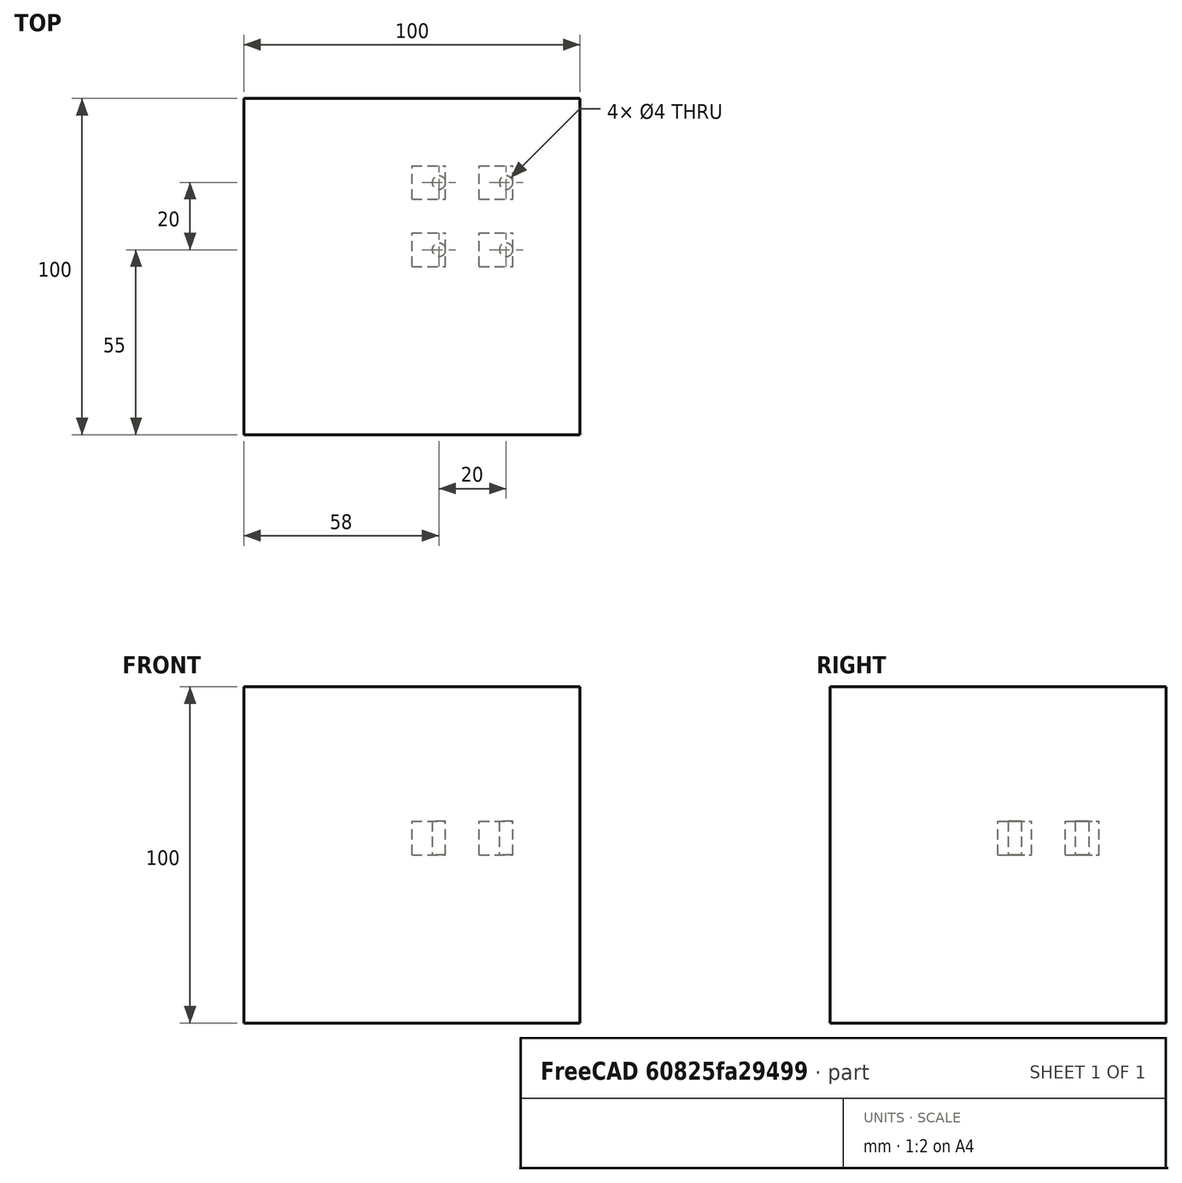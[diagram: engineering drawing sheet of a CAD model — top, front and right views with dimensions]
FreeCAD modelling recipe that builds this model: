
FCSTD DOCUMENT  (FreeCAD 1.0R39109 (Git))
Label: orthoArray_of_Cut
License: All rights reserved
objects: App::DocumentObjectGroupPython×1251, Part::FeaturePython×2, App::Part×2, Part::Box×1, Part::Cylinder×1, Part::Cut×1
note: 5 computed .brp shape members not serialized (recipe doc carries the construction recipe); baked Part::Feature solids carry a one-line shape summary decoded from their .brp

FEATURE [App::DocumentObjectGroupPython] HALFPI  # scripted group (container) (typed FeaturePython)
  name = HALFPI
  value = pi/2.
FEATURE [App::DocumentObjectGroupPython] PI  # scripted group (container) (typed FeaturePython)
  name = PI
  value = 1.*pi
FEATURE [App::DocumentObjectGroupPython] TWOPI  # scripted group (container) (typed FeaturePython)
  name = TWOPI
  value = 2.*pi
FEATURE [App::DocumentObjectGroupPython] Constants  # scripted group (container) (typed FeaturePython)
  Group = -> [HALFPI,PI,TWOPI]
FEATURE [App::DocumentObjectGroupPython] Variables  # scripted group (container) (typed FeaturePython)
FEATURE [App::DocumentObjectGroupPython] Quantities  # scripted group (container) (typed FeaturePython)
FEATURE [App::DocumentObjectGroupPython] Isotopes  # scripted group (container) (typed FeaturePython)
FEATURE [App::DocumentObjectGroupPython] Elements  # scripted group (container) (typed FeaturePython)
FEATURE [App::DocumentObjectGroupPython] Matrix  # scripted group (container) (typed FeaturePython)
FEATURE [App::DocumentObjectGroupPython] Surfaces  # scripted group (container) (typed FeaturePython)
FEATURE [App::DocumentObjectGroupPython] Opticals  # scripted group (container) (typed FeaturePython)
  Group = -> [Matrix,Surfaces]
FEATURE [App::DocumentObjectGroupPython] G4Isotopes  # scripted group (container) (typed FeaturePython)
FEATURE [App::DocumentObjectGroupPython] H_element  # scripted group (container) (typed FeaturePython)
  Z = 1
  atom_value = 1.008
  formula = H
  name = H_element
FEATURE [App::DocumentObjectGroupPython] He_element  # scripted group (container) (typed FeaturePython)
  Z = 2
  atom_value = 4.0026
  formula = He
  name = He_element
FEATURE [App::DocumentObjectGroupPython] Li_element  # scripted group (container) (typed FeaturePython)
  Z = 3
  atom_value = 6.94
  formula = Li
  name = Li_element
FEATURE [App::DocumentObjectGroupPython] Be_element  # scripted group (container) (typed FeaturePython)
  Z = 4
  atom_value = 9.01218
  formula = Be
  name = Be_element
FEATURE [App::DocumentObjectGroupPython] B_element  # scripted group (container) (typed FeaturePython)
  Z = 5
  atom_value = 10.81
  formula = B
  name = B_element
FEATURE [App::DocumentObjectGroupPython] C_element  # scripted group (container) (typed FeaturePython)
  Z = 6
  atom_value = 12.011
  formula = C
  name = C_element
FEATURE [App::DocumentObjectGroupPython] N_element  # scripted group (container) (typed FeaturePython)
  Z = 7
  atom_value = 14.007
  formula = N
  name = N_element
FEATURE [App::DocumentObjectGroupPython] O_element  # scripted group (container) (typed FeaturePython)
  Z = 8
  atom_value = 15.999
  formula = O
  name = O_element
FEATURE [App::DocumentObjectGroupPython] F_element  # scripted group (container) (typed FeaturePython)
  Z = 9
  atom_value = 18.9984
  formula = F
  name = F_element
FEATURE [App::DocumentObjectGroupPython] Ne_element  # scripted group (container) (typed FeaturePython)
  Z = 10
  atom_value = 20.1797
  formula = Ne
  name = Ne_element
FEATURE [App::DocumentObjectGroupPython] Na_element  # scripted group (container) (typed FeaturePython)
  Z = 11
  atom_value = 22.9898
  formula = Na
  name = Na_element
FEATURE [App::DocumentObjectGroupPython] Mg_element  # scripted group (container) (typed FeaturePython)
  Z = 12
  atom_value = 24.305
  formula = Mg
  name = Mg_element
FEATURE [App::DocumentObjectGroupPython] Al_element  # scripted group (container) (typed FeaturePython)
  Z = 13
  atom_value = 26.9815
  formula = Al
  name = Al_element
FEATURE [App::DocumentObjectGroupPython] Si_element  # scripted group (container) (typed FeaturePython)
  Z = 14
  atom_value = 28.085
  formula = Si
  name = Si_element
FEATURE [App::DocumentObjectGroupPython] P_element  # scripted group (container) (typed FeaturePython)
  Z = 15
  atom_value = 30.9738
  formula = P
  name = P_element
FEATURE [App::DocumentObjectGroupPython] S_element  # scripted group (container) (typed FeaturePython)
  Z = 16
  atom_value = 32.06
  formula = S
  name = S_element
FEATURE [App::DocumentObjectGroupPython] Cl_element  # scripted group (container) (typed FeaturePython)
  Z = 17
  atom_value = 35.45
  formula = Cl
  name = Cl_element
FEATURE [App::DocumentObjectGroupPython] Ar_element  # scripted group (container) (typed FeaturePython)
  Z = 18
  atom_value = 39.95
  formula = Ar
  name = Ar_element
FEATURE [App::DocumentObjectGroupPython] K_element  # scripted group (container) (typed FeaturePython)
  Z = 19
  atom_value = 39.0983
  formula = K
  name = K_element
FEATURE [App::DocumentObjectGroupPython] Ca_element  # scripted group (container) (typed FeaturePython)
  Z = 20
  atom_value = 40.078
  formula = Ca
  name = Ca_element
FEATURE [App::DocumentObjectGroupPython] Sc_element  # scripted group (container) (typed FeaturePython)
  Z = 21
  atom_value = 44.9559
  formula = Sc
  name = Sc_element
FEATURE [App::DocumentObjectGroupPython] Ti_element  # scripted group (container) (typed FeaturePython)
  Z = 22
  atom_value = 47.867
  formula = Ti
  name = Ti_element
FEATURE [App::DocumentObjectGroupPython] V_element  # scripted group (container) (typed FeaturePython)
  Z = 23
  atom_value = 50.9415
  formula = V
  name = V_element
FEATURE [App::DocumentObjectGroupPython] Cr_element  # scripted group (container) (typed FeaturePython)
  Z = 24
  atom_value = 51.9961
  formula = Cr
  name = Cr_element
FEATURE [App::DocumentObjectGroupPython] Mn_element  # scripted group (container) (typed FeaturePython)
  Z = 25
  atom_value = 54.938
  formula = Mn
  name = Mn_element
FEATURE [App::DocumentObjectGroupPython] Fe_element  # scripted group (container) (typed FeaturePython)
  Z = 26
  atom_value = 55.845
  formula = Fe
  name = Fe_element
FEATURE [App::DocumentObjectGroupPython] Co_element  # scripted group (container) (typed FeaturePython)
  Z = 27
  atom_value = 58.9332
  formula = Co
  name = Co_element
FEATURE [App::DocumentObjectGroupPython] Ni_element  # scripted group (container) (typed FeaturePython)
  Z = 28
  atom_value = 58.6934
  formula = Ni
  name = Ni_element
FEATURE [App::DocumentObjectGroupPython] Cu_element  # scripted group (container) (typed FeaturePython)
  Z = 29
  atom_value = 63.546
  formula = Cu
  name = Cu_element
FEATURE [App::DocumentObjectGroupPython] Zn_element  # scripted group (container) (typed FeaturePython)
  Z = 30
  atom_value = 65.38
  formula = Zn
  name = Zn_element
FEATURE [App::DocumentObjectGroupPython] Ga_element  # scripted group (container) (typed FeaturePython)
  Z = 31
  atom_value = 69.723
  formula = Ga
  name = Ga_element
FEATURE [App::DocumentObjectGroupPython] Ge_element  # scripted group (container) (typed FeaturePython)
  Z = 32
  atom_value = 72.63
  formula = Ge
  name = Ge_element
FEATURE [App::DocumentObjectGroupPython] As_element  # scripted group (container) (typed FeaturePython)
  Z = 33
  atom_value = 74.9216
  formula = As
  name = As_element
FEATURE [App::DocumentObjectGroupPython] Se_element  # scripted group (container) (typed FeaturePython)
  Z = 34
  atom_value = 78.971
  formula = Se
  name = Se_element
FEATURE [App::DocumentObjectGroupPython] Br_element  # scripted group (container) (typed FeaturePython)
  Z = 35
  atom_value = 79.904
  formula = Br
  name = Br_element
FEATURE [App::DocumentObjectGroupPython] Kr_element  # scripted group (container) (typed FeaturePython)
  Z = 36
  atom_value = 83.798
  formula = Kr
  name = Kr_element
FEATURE [App::DocumentObjectGroupPython] Rb_element  # scripted group (container) (typed FeaturePython)
  Z = 37
  atom_value = 85.4678
  formula = Rb
  name = Rb_element
FEATURE [App::DocumentObjectGroupPython] Sr_element  # scripted group (container) (typed FeaturePython)
  Z = 38
  atom_value = 87.62
  formula = Sr
  name = Sr_element
FEATURE [App::DocumentObjectGroupPython] Y_element  # scripted group (container) (typed FeaturePython)
  Z = 39
  atom_value = 88.9058
  formula = Y
  name = Y_element
FEATURE [App::DocumentObjectGroupPython] Zr_element  # scripted group (container) (typed FeaturePython)
  Z = 40
  atom_value = 91.224
  formula = Zr
  name = Zr_element
FEATURE [App::DocumentObjectGroupPython] Nb_element  # scripted group (container) (typed FeaturePython)
  Z = 41
  atom_value = 92.9064
  formula = Nb
  name = Nb_element
FEATURE [App::DocumentObjectGroupPython] Mo_element  # scripted group (container) (typed FeaturePython)
  Z = 42
  atom_value = 95.95
  formula = Mo
  name = Mo_element
FEATURE [App::DocumentObjectGroupPython] Tc_element  # scripted group (container) (typed FeaturePython)
  Z = 43
  atom_value = 97
  formula = Tc
  name = Tc_element
FEATURE [App::DocumentObjectGroupPython] Ru_element  # scripted group (container) (typed FeaturePython)
  Z = 44
  atom_value = 101.07
  formula = Ru
  name = Ru_element
FEATURE [App::DocumentObjectGroupPython] Rh_element  # scripted group (container) (typed FeaturePython)
  Z = 45
  atom_value = 102.905
  formula = Rh
  name = Rh_element
FEATURE [App::DocumentObjectGroupPython] Pd_element  # scripted group (container) (typed FeaturePython)
  Z = 46
  atom_value = 106.42
  formula = Pd
  name = Pd_element
FEATURE [App::DocumentObjectGroupPython] Ag_element  # scripted group (container) (typed FeaturePython)
  Z = 47
  atom_value = 107.868
  formula = Ag
  name = Ag_element
FEATURE [App::DocumentObjectGroupPython] Cd_element  # scripted group (container) (typed FeaturePython)
  Z = 48
  atom_value = 112.414
  formula = Cd
  name = Cd_element
FEATURE [App::DocumentObjectGroupPython] In_element  # scripted group (container) (typed FeaturePython)
  Z = 49
  atom_value = 114.818
  formula = In
  name = In_element
FEATURE [App::DocumentObjectGroupPython] Sn_element  # scripted group (container) (typed FeaturePython)
  Z = 50
  atom_value = 118.71
  formula = Sn
  name = Sn_element
FEATURE [App::DocumentObjectGroupPython] Sb_element  # scripted group (container) (typed FeaturePython)
  Z = 51
  atom_value = 121.76
  formula = Sb
  name = Sb_element
FEATURE [App::DocumentObjectGroupPython] Te_element  # scripted group (container) (typed FeaturePython)
  Z = 52
  atom_value = 127.6
  formula = Te
  name = Te_element
FEATURE [App::DocumentObjectGroupPython] I_element  # scripted group (container) (typed FeaturePython)
  Z = 53
  atom_value = 126.904
  formula = I
  name = I_element
FEATURE [App::DocumentObjectGroupPython] Xe_element  # scripted group (container) (typed FeaturePython)
  Z = 54
  atom_value = 131.293
  formula = Xe
  name = Xe_element
FEATURE [App::DocumentObjectGroupPython] Cs_element  # scripted group (container) (typed FeaturePython)
  Z = 55
  atom_value = 132.905
  formula = Cs
  name = Cs_element
FEATURE [App::DocumentObjectGroupPython] Ba_element  # scripted group (container) (typed FeaturePython)
  Z = 56
  atom_value = 137.327
  formula = Ba
  name = Ba_element
FEATURE [App::DocumentObjectGroupPython] La_element  # scripted group (container) (typed FeaturePython)
  Z = 57
  atom_value = 138.905
  formula = La
  name = La_element
FEATURE [App::DocumentObjectGroupPython] Ce_element  # scripted group (container) (typed FeaturePython)
  Z = 58
  atom_value = 140.116
  formula = Ce
  name = Ce_element
FEATURE [App::DocumentObjectGroupPython] Pr_element  # scripted group (container) (typed FeaturePython)
  Z = 59
  atom_value = 140.908
  formula = Pr
  name = Pr_element
FEATURE [App::DocumentObjectGroupPython] Nd_element  # scripted group (container) (typed FeaturePython)
  Z = 60
  atom_value = 144.242
  formula = Nd
  name = Nd_element
FEATURE [App::DocumentObjectGroupPython] Pm_element  # scripted group (container) (typed FeaturePython)
  Z = 61
  atom_value = 145
  formula = Pm
  name = Pm_element
FEATURE [App::DocumentObjectGroupPython] Sm_element  # scripted group (container) (typed FeaturePython)
  Z = 62
  atom_value = 150.36
  formula = Sm
  name = Sm_element
FEATURE [App::DocumentObjectGroupPython] Eu_element  # scripted group (container) (typed FeaturePython)
  Z = 63
  atom_value = 151.964
  formula = Eu
  name = Eu_element
FEATURE [App::DocumentObjectGroupPython] Gd_element  # scripted group (container) (typed FeaturePython)
  Z = 64
  atom_value = 157.25
  formula = Gd
  name = Gd_element
FEATURE [App::DocumentObjectGroupPython] Tb_element  # scripted group (container) (typed FeaturePython)
  Z = 65
  atom_value = 158.925
  formula = Tb
  name = Tb_element
FEATURE [App::DocumentObjectGroupPython] Dy_element  # scripted group (container) (typed FeaturePython)
  Z = 66
  atom_value = 162.5
  formula = Dy
  name = Dy_element
FEATURE [App::DocumentObjectGroupPython] Ho_element  # scripted group (container) (typed FeaturePython)
  Z = 67
  atom_value = 164.93
  formula = Ho
  name = Ho_element
FEATURE [App::DocumentObjectGroupPython] Er_element  # scripted group (container) (typed FeaturePython)
  Z = 68
  atom_value = 167.259
  formula = Er
  name = Er_element
FEATURE [App::DocumentObjectGroupPython] Tm_element  # scripted group (container) (typed FeaturePython)
  Z = 69
  atom_value = 168.934
  formula = Tm
  name = Tm_element
FEATURE [App::DocumentObjectGroupPython] Yb_element  # scripted group (container) (typed FeaturePython)
  Z = 70
  atom_value = 173.045
  formula = Yb
  name = Yb_element
FEATURE [App::DocumentObjectGroupPython] Lu_element  # scripted group (container) (typed FeaturePython)
  Z = 71
  atom_value = 174.967
  formula = Lu
  name = Lu_element
FEATURE [App::DocumentObjectGroupPython] Hf_element  # scripted group (container) (typed FeaturePython)
  Z = 72
  atom_value = 178.49
  formula = Hf
  name = Hf_element
FEATURE [App::DocumentObjectGroupPython] Ta_element  # scripted group (container) (typed FeaturePython)
  Z = 73
  atom_value = 180.948
  formula = Ta
  name = Ta_element
FEATURE [App::DocumentObjectGroupPython] W_element  # scripted group (container) (typed FeaturePython)
  Z = 74
  atom_value = 183.84
  formula = W
  name = W_element
FEATURE [App::DocumentObjectGroupPython] Re_element  # scripted group (container) (typed FeaturePython)
  Z = 75
  atom_value = 186.207
  formula = Re
  name = Re_element
FEATURE [App::DocumentObjectGroupPython] Os_element  # scripted group (container) (typed FeaturePython)
  Z = 76
  atom_value = 190.23
  formula = Os
  name = Os_element
FEATURE [App::DocumentObjectGroupPython] Ir_element  # scripted group (container) (typed FeaturePython)
  Z = 77
  atom_value = 192.217
  formula = Ir
  name = Ir_element
FEATURE [App::DocumentObjectGroupPython] Pt_element  # scripted group (container) (typed FeaturePython)
  Z = 78
  atom_value = 195.084
  formula = Pt
  name = Pt_element
FEATURE [App::DocumentObjectGroupPython] Au_element  # scripted group (container) (typed FeaturePython)
  Z = 79
  atom_value = 196.967
  formula = Au
  name = Au_element
FEATURE [App::DocumentObjectGroupPython] Hg_element  # scripted group (container) (typed FeaturePython)
  Z = 80
  atom_value = 200.592
  formula = Hg
  name = Hg_element
FEATURE [App::DocumentObjectGroupPython] Tl_element  # scripted group (container) (typed FeaturePython)
  Z = 81
  atom_value = 204.38
  formula = Tl
  name = Tl_element
FEATURE [App::DocumentObjectGroupPython] Pb_element  # scripted group (container) (typed FeaturePython)
  Z = 82
  atom_value = 207.2
  formula = Pb
  name = Pb_element
FEATURE [App::DocumentObjectGroupPython] Bi_element  # scripted group (container) (typed FeaturePython)
  Z = 83
  atom_value = 208.98
  formula = Bi
  name = Bi_element
FEATURE [App::DocumentObjectGroupPython] Po_element  # scripted group (container) (typed FeaturePython)
  Z = 84
  atom_value = 209
  formula = Po
  name = Po_element
FEATURE [App::DocumentObjectGroupPython] At_element  # scripted group (container) (typed FeaturePython)
  Z = 85
  atom_value = 210
  formula = At
  name = At_element
FEATURE [App::DocumentObjectGroupPython] Rn_element  # scripted group (container) (typed FeaturePython)
  Z = 86
  atom_value = 222
  formula = Rn
  name = Rn_element
FEATURE [App::DocumentObjectGroupPython] Fr_element  # scripted group (container) (typed FeaturePython)
  Z = 87
  atom_value = 223
  formula = Fr
  name = Fr_element
FEATURE [App::DocumentObjectGroupPython] Ra_element  # scripted group (container) (typed FeaturePython)
  Z = 88
  atom_value = 226
  formula = Ra
  name = Ra_element
FEATURE [App::DocumentObjectGroupPython] Ac_element  # scripted group (container) (typed FeaturePython)
  Z = 89
  atom_value = 227
  formula = Ac
  name = Ac_element
FEATURE [App::DocumentObjectGroupPython] Th_element  # scripted group (container) (typed FeaturePython)
  Z = 90
  atom_value = 232.038
  formula = Th
  name = Th_element
FEATURE [App::DocumentObjectGroupPython] Pa_element  # scripted group (container) (typed FeaturePython)
  Z = 91
  atom_value = 231.036
  formula = Pa
  name = Pa_element
FEATURE [App::DocumentObjectGroupPython] U_element  # scripted group (container) (typed FeaturePython)
  Z = 92
  atom_value = 238.029
  formula = U
  name = U_element
FEATURE [App::DocumentObjectGroupPython] Np_element  # scripted group (container) (typed FeaturePython)
  Z = 93
  atom_value = 237
  formula = Np
  name = Np_element
FEATURE [App::DocumentObjectGroupPython] Pu_element  # scripted group (container) (typed FeaturePython)
  Z = 94
  atom_value = 244
  formula = Pu
  name = Pu_element
FEATURE [App::DocumentObjectGroupPython] Am_element  # scripted group (container) (typed FeaturePython)
  Z = 95
  atom_value = 243
  formula = Am
  name = Am_element
FEATURE [App::DocumentObjectGroupPython] Cm_element  # scripted group (container) (typed FeaturePython)
  Z = 96
  atom_value = 247
  formula = Cm
  name = Cm_element
FEATURE [App::DocumentObjectGroupPython] Bk_element  # scripted group (container) (typed FeaturePython)
  Z = 97
  atom_value = 247
  formula = Bk
  name = Bk_element
FEATURE [App::DocumentObjectGroupPython] Cf_element  # scripted group (container) (typed FeaturePython)
  Z = 98
  atom_value = 251
  formula = Cf
  name = Cf_element
FEATURE [App::DocumentObjectGroupPython] G4Elements  # scripted group (container) (typed FeaturePython)
  Group = -> [H_element,He_element,Li_element,Be_element,B_element,C_element,N_element,O_element,F_element,Ne_element,Na_element,Mg_element,Al_element,Si_element,P_element,S_element,Cl_element,Ar_element,K_element,Ca_element,Sc_element,Ti_element,V_element,Cr_element,Mn_element,Fe_element,Co_element,Ni_element,Cu_element,Zn_element,Ga_element,Ge_element,As_element,Se_element,Br_element,Kr_element,Rb_element,+61 more]
FEATURE [App::DocumentObjectGroupPython] H_element001  label="H_element : 0.101"  # scripted group (container) (typed FeaturePython)
  n = 0.101327
FEATURE [App::DocumentObjectGroupPython] C_element001  label="C_element : 0.775"  # scripted group (container) (typed FeaturePython)
  n = 0.7755
FEATURE [App::DocumentObjectGroupPython] N_element001  label="N_element : 0.035"  # scripted group (container) (typed FeaturePython)
  n = 0.035057
FEATURE [App::DocumentObjectGroupPython] O_element001  label="O_element : 0.052"  # scripted group (container) (typed FeaturePython)
  n = 0.0523159
FEATURE [App::DocumentObjectGroupPython] F_element001  label="F_element : 0.017"  # scripted group (container) (typed FeaturePython)
  n = 0.017422
FEATURE [App::DocumentObjectGroupPython] Ca_element001  label="Ca_element : 0.018"  # scripted group (container) (typed FeaturePython)
  n = 0.018378
FEATURE [App::DocumentObjectGroupPython] G4_A_150_TISSUE  label="G4_A-150_TISSUE"  # scripted group (container) (typed FeaturePython)
  Dunit = g/cm3
  Dvalue = 1.127
  Group = -> [H_element001,C_element001,N_element001,O_element001,F_element001,Ca_element001]
  conduct = 2
  density = 1
  expand = 3
  formula = G4_A-150_TISSUE
  name = G4_A-150_TISSUE
  specific = 4
FEATURE [App::DocumentObjectGroupPython] C_element002  label="C_element : 3"  # scripted group (container) (typed FeaturePython)
  n = 3
  ref = C_element
FEATURE [App::DocumentObjectGroupPython] H_element002  label="H_element : 6"  # scripted group (container) (typed FeaturePython)
  n = 6
  ref = H_element
FEATURE [App::DocumentObjectGroupPython] O_element002  label="O_element : 1"  # scripted group (container) (typed FeaturePython)
  n = 1
  ref = O_element
FEATURE [App::DocumentObjectGroupPython] G4_ACETONE  # scripted group (container) (typed FeaturePython)
  Dunit = g/cm3
  Dvalue = 0.7899
  Group = -> [C_element002,H_element002,O_element002]
  conduct = 2
  density = 1
  expand = 3
  formula = G4_ACETONE
  name = G4_ACETONE
  specific = 4
FEATURE [App::DocumentObjectGroupPython] C_element003  label="C_element : 2"  # scripted group (container) (typed FeaturePython)
  n = 2
  ref = C_element
FEATURE [App::DocumentObjectGroupPython] H_element003  label="H_element : 2"  # scripted group (container) (typed FeaturePython)
  n = 2
  ref = H_element
FEATURE [App::DocumentObjectGroupPython] G4_ACETYLENE  # scripted group (container) (typed FeaturePython)
  Dunit = g/cm3
  Dvalue = 0.0010967
  Group = -> [C_element003,H_element003]
  conduct = 2
  density = 1
  expand = 3
  formula = G4_ACETYLENE
  name = G4_ACETYLENE
  specific = 4
FEATURE [App::DocumentObjectGroupPython] C_element004  label="C_element : 5"  # scripted group (container) (typed FeaturePython)
  n = 5
  ref = C_element
FEATURE [App::DocumentObjectGroupPython] H_element004  label="H_element : 5"  # scripted group (container) (typed FeaturePython)
  n = 5
  ref = H_element
FEATURE [App::DocumentObjectGroupPython] N_element002  label="N_element : 5"  # scripted group (container) (typed FeaturePython)
  n = 5
  ref = N_element
FEATURE [App::DocumentObjectGroupPython] G4_ADENINE  # scripted group (container) (typed FeaturePython)
  Dunit = g/cm3
  Dvalue = 1.6
  Group = -> [C_element004,H_element004,N_element002]
  conduct = 2
  density = 1
  expand = 3
  formula = G4_ADENINE
  name = G4_ADENINE
  specific = 4
FEATURE [App::DocumentObjectGroupPython] H_element005  label="H_element : 0.114"  # scripted group (container) (typed FeaturePython)
  n = 0.114
FEATURE [App::DocumentObjectGroupPython] C_element005  label="C_element : 0.598"  # scripted group (container) (typed FeaturePython)
  n = 0.598
FEATURE [App::DocumentObjectGroupPython] N_element003  label="N_element : 0.007"  # scripted group (container) (typed FeaturePython)
  n = 0.007
FEATURE [App::DocumentObjectGroupPython] O_element003  label="O_element : 0.278"  # scripted group (container) (typed FeaturePython)
  n = 0.278
FEATURE [App::DocumentObjectGroupPython] Na_element001  label="Na_element : 0.001"  # scripted group (container) (typed FeaturePython)
  n = 0.001
FEATURE [App::DocumentObjectGroupPython] S_element001  label="S_element : 0.001"  # scripted group (container) (typed FeaturePython)
  n = 0.001
FEATURE [App::DocumentObjectGroupPython] Cl_element001  label="Cl_element : 0.001"  # scripted group (container) (typed FeaturePython)
  n = 0.001
FEATURE [App::DocumentObjectGroupPython] G4_ADIPOSE_TISSUE_ICRP  # scripted group (container) (typed FeaturePython)
  Dunit = g/cm3
  Dvalue = 0.95
  Group = -> [H_element005,C_element005,N_element003,O_element003,Na_element001,S_element001,Cl_element001]
  conduct = 2
  density = 1
  expand = 3
  formula = G4_ADIPOSE_TISSUE_ICRP
  name = G4_ADIPOSE_TISSUE_ICRP
  specific = 4
FEATURE [App::DocumentObjectGroupPython] C_element006  label="C_element : 0.000"  # scripted group (container) (typed FeaturePython)
  n = 0.000124
FEATURE [App::DocumentObjectGroupPython] N_element004  label="N_element : 0.755"  # scripted group (container) (typed FeaturePython)
  n = 0.755268
FEATURE [App::DocumentObjectGroupPython] O_element004  label="O_element : 0.232"  # scripted group (container) (typed FeaturePython)
  n = 0.231781
FEATURE [App::DocumentObjectGroupPython] Ar_element001  label="Ar_element : 0.013"  # scripted group (container) (typed FeaturePython)
  n = 0.012827
FEATURE [App::DocumentObjectGroupPython] G4_AIR  # scripted group (container) (typed FeaturePython)
  Dunit = g/cm3
  Dvalue = 0.00120479
  Group = -> [C_element006,N_element004,O_element004,Ar_element001]
  conduct = 2
  density = 1
  expand = 3
  formula = G4_AIR
  name = G4_AIR
  specific = 4
FEATURE [App::DocumentObjectGroupPython] C_element007  label="C_element : 006"  # scripted group (container) (typed FeaturePython)
  n = 3
  ref = C_element
FEATURE [App::DocumentObjectGroupPython] H_element006  label="H_element : 7"  # scripted group (container) (typed FeaturePython)
  n = 7
  ref = H_element
FEATURE [App::DocumentObjectGroupPython] N_element005  label="N_element : 1"  # scripted group (container) (typed FeaturePython)
  n = 1
  ref = N_element
FEATURE [App::DocumentObjectGroupPython] O_element005  label="O_element : 2"  # scripted group (container) (typed FeaturePython)
  n = 2
  ref = O_element
FEATURE [App::DocumentObjectGroupPython] G4_ALANINE  # scripted group (container) (typed FeaturePython)
  Dunit = g/cm3
  Dvalue = 1.42
  Group = -> [C_element007,H_element006,N_element005,O_element005]
  conduct = 2
  density = 1
  expand = 3
  formula = G4_ALANINE
  name = G4_ALANINE
  specific = 4
FEATURE [App::DocumentObjectGroupPython] Al_element001  label="Al_element : 2"  # scripted group (container) (typed FeaturePython)
  n = 2
  ref = Al_element
FEATURE [App::DocumentObjectGroupPython] O_element006  label="O_element : 3"  # scripted group (container) (typed FeaturePython)
  n = 3
  ref = O_element
FEATURE [App::DocumentObjectGroupPython] G4_ALUMINUM_OXIDE  # scripted group (container) (typed FeaturePython)
  Dunit = g/cm3
  Dvalue = 3.97
  Group = -> [Al_element001,O_element006]
  conduct = 2
  density = 1
  expand = 3
  formula = G4_ALUMINUM_OXIDE
  name = G4_ALUMINUM_OXIDE
  specific = 4
FEATURE [App::DocumentObjectGroupPython] H_element007  label="H_element : 0.106"  # scripted group (container) (typed FeaturePython)
  n = 0.10593
FEATURE [App::DocumentObjectGroupPython] C_element008  label="C_element : 0.789"  # scripted group (container) (typed FeaturePython)
  n = 0.788974
FEATURE [App::DocumentObjectGroupPython] O_element007  label="O_element : 0.105"  # scripted group (container) (typed FeaturePython)
  n = 0.105096
FEATURE [App::DocumentObjectGroupPython] G4_AMBER  # scripted group (container) (typed FeaturePython)
  Dunit = g/cm3
  Dvalue = 1.1
  Group = -> [H_element007,C_element008,O_element007]
  conduct = 2
  density = 1
  expand = 3
  formula = G4_AMBER
  name = G4_AMBER
  specific = 4
FEATURE [App::DocumentObjectGroupPython] N_element006  label="N_element : 006"  # scripted group (container) (typed FeaturePython)
  n = 1
  ref = N_element
FEATURE [App::DocumentObjectGroupPython] H_element008  label="H_element : 3"  # scripted group (container) (typed FeaturePython)
  n = 3
  ref = H_element
FEATURE [App::DocumentObjectGroupPython] G4_AMMONIA  # scripted group (container) (typed FeaturePython)
  Dunit = g/cm3
  Dvalue = 0.000826019
  Group = -> [N_element006,H_element008]
  conduct = 2
  density = 1
  expand = 3
  formula = G4_AMMONIA
  name = G4_AMMONIA
  specific = 4
FEATURE [App::DocumentObjectGroupPython] C_element009  label="C_element : 6"  # scripted group (container) (typed FeaturePython)
  n = 6
  ref = C_element
FEATURE [App::DocumentObjectGroupPython] H_element009  label="H_element : 008"  # scripted group (container) (typed FeaturePython)
  n = 7
  ref = H_element
FEATURE [App::DocumentObjectGroupPython] N_element007  label="N_element : 007"  # scripted group (container) (typed FeaturePython)
  n = 1
  ref = N_element
FEATURE [App::DocumentObjectGroupPython] G4_ANILINE  # scripted group (container) (typed FeaturePython)
  Dunit = g/cm3
  Dvalue = 1.0235
  Group = -> [C_element009,H_element009,N_element007]
  conduct = 2
  density = 1
  expand = 3
  formula = G4_ANILINE
  name = G4_ANILINE
  specific = 4
FEATURE [App::DocumentObjectGroupPython] C_element010  label="C_element : 14"  # scripted group (container) (typed FeaturePython)
  n = 14
  ref = C_element
FEATURE [App::DocumentObjectGroupPython] H_element010  label="H_element : 10"  # scripted group (container) (typed FeaturePython)
  n = 10
  ref = H_element
FEATURE [App::DocumentObjectGroupPython] G4_ANTHRACENE  # scripted group (container) (typed FeaturePython)
  Dunit = g/cm3
  Dvalue = 1.283
  Group = -> [C_element010,H_element010]
  conduct = 2
  density = 1
  expand = 3
  formula = G4_ANTHRACENE
  name = G4_ANTHRACENE
  specific = 4
FEATURE [App::DocumentObjectGroupPython] H_element011  label="H_element : 0.065"  # scripted group (container) (typed FeaturePython)
  n = 0.0654709
FEATURE [App::DocumentObjectGroupPython] C_element011  label="C_element : 0.537"  # scripted group (container) (typed FeaturePython)
  n = 0.536944
FEATURE [App::DocumentObjectGroupPython] N_element008  label="N_element : 0.021"  # scripted group (container) (typed FeaturePython)
  n = 0.0215
FEATURE [App::DocumentObjectGroupPython] O_element008  label="O_element : 0.032"  # scripted group (container) (typed FeaturePython)
  n = 0.032085
FEATURE [App::DocumentObjectGroupPython] F_element002  label="F_element : 0.167"  # scripted group (container) (typed FeaturePython)
  n = 0.167411
FEATURE [App::DocumentObjectGroupPython] Ca_element002  label="Ca_element : 0.177"  # scripted group (container) (typed FeaturePython)
  n = 0.176589
FEATURE [App::DocumentObjectGroupPython] G4_B_100_BONE  label="G4_B-100_BONE"  # scripted group (container) (typed FeaturePython)
  Dunit = g/cm3
  Dvalue = 1.45
  Group = -> [H_element011,C_element011,N_element008,O_element008,F_element002,Ca_element002]
  conduct = 2
  density = 1
  expand = 3
  formula = G4_B-100_BONE
  name = G4_B-100_BONE
  specific = 4
FEATURE [App::DocumentObjectGroupPython] H_element012  label="H_element : 0.057"  # scripted group (container) (typed FeaturePython)
  n = 0.057441
FEATURE [App::DocumentObjectGroupPython] C_element012  label="C_element : 0.790"  # scripted group (container) (typed FeaturePython)
  n = 0.774591
FEATURE [App::DocumentObjectGroupPython] O_element009  label="O_element : 0.168"  # scripted group (container) (typed FeaturePython)
  n = 0.167968
FEATURE [App::DocumentObjectGroupPython] G4_BAKELITE  # scripted group (container) (typed FeaturePython)
  Dunit = g/cm3
  Dvalue = 1.25
  Group = -> [H_element012,C_element012,O_element009]
  conduct = 2
  density = 1
  expand = 3
  formula = G4_BAKELITE
  name = G4_BAKELITE
  specific = 4
FEATURE [App::DocumentObjectGroupPython] Ba_element001  label="Ba_element : 1"  # scripted group (container) (typed FeaturePython)
  n = 1
  ref = Ba_element
FEATURE [App::DocumentObjectGroupPython] F_element003  label="F_element : 2"  # scripted group (container) (typed FeaturePython)
  n = 2
  ref = F_element
FEATURE [App::DocumentObjectGroupPython] G4_BARIUM_FLUORIDE  # scripted group (container) (typed FeaturePython)
  Dunit = g/cm3
  Dvalue = 4.89
  Group = -> [Ba_element001,F_element003]
  conduct = 2
  density = 1
  expand = 3
  formula = G4_BARIUM_FLUORIDE
  name = G4_BARIUM_FLUORIDE
  specific = 4
FEATURE [App::DocumentObjectGroupPython] Ba_element002  label="Ba_element : 002"  # scripted group (container) (typed FeaturePython)
  n = 1
  ref = Ba_element
FEATURE [App::DocumentObjectGroupPython] S_element002  label="S_element : 1"  # scripted group (container) (typed FeaturePython)
  n = 1
  ref = S_element
FEATURE [App::DocumentObjectGroupPython] O_element010  label="O_element : 4"  # scripted group (container) (typed FeaturePython)
  n = 4
  ref = O_element
FEATURE [App::DocumentObjectGroupPython] G4_BARIUM_SULFATE  # scripted group (container) (typed FeaturePython)
  Dunit = g/cm3
  Dvalue = 4.5
  Group = -> [Ba_element002,S_element002,O_element010]
  conduct = 2
  density = 1
  expand = 3
  formula = G4_BARIUM_SULFATE
  name = G4_BARIUM_SULFATE
  specific = 4
FEATURE [App::DocumentObjectGroupPython] C_element013  label="C_element : 007"  # scripted group (container) (typed FeaturePython)
  n = 6
  ref = C_element
FEATURE [App::DocumentObjectGroupPython] H_element013  label="H_element : 009"  # scripted group (container) (typed FeaturePython)
  n = 6
  ref = H_element
FEATURE [App::DocumentObjectGroupPython] G4_BENZENE  # scripted group (container) (typed FeaturePython)
  Dunit = g/cm3
  Dvalue = 0.87865
  Group = -> [C_element013,H_element013]
  conduct = 2
  density = 1
  expand = 3
  formula = G4_BENZENE
  name = G4_BENZENE
  specific = 4
FEATURE [App::DocumentObjectGroupPython] Be_element001  label="Be_element : 1"  # scripted group (container) (typed FeaturePython)
  n = 1
  ref = Be_element
FEATURE [App::DocumentObjectGroupPython] O_element011  label="O_element : 005"  # scripted group (container) (typed FeaturePython)
  n = 1
  ref = O_element
FEATURE [App::DocumentObjectGroupPython] G4_BERYLLIUM_OXIDE  # scripted group (container) (typed FeaturePython)
  Dunit = g/cm3
  Dvalue = 3.01
  Group = -> [Be_element001,O_element011]
  conduct = 2
  density = 1
  expand = 3
  formula = G4_BERYLLIUM_OXIDE
  name = G4_BERYLLIUM_OXIDE
  specific = 4
FEATURE [App::DocumentObjectGroupPython] Bi_element001  label="Bi_element : 4"  # scripted group (container) (typed FeaturePython)
  n = 4
  ref = Bi_element
FEATURE [App::DocumentObjectGroupPython] Ge_element001  label="Ge_element : 3"  # scripted group (container) (typed FeaturePython)
  n = 3
  ref = Ge_element
FEATURE [App::DocumentObjectGroupPython] O_element012  label="O_element : 12"  # scripted group (container) (typed FeaturePython)
  n = 12
  ref = O_element
FEATURE [App::DocumentObjectGroupPython] G4_BGO  # scripted group (container) (typed FeaturePython)
  Dunit = g/cm3
  Dvalue = 7.13
  Group = -> [Bi_element001,Ge_element001,O_element012]
  conduct = 2
  density = 1
  expand = 3
  formula = G4_BGO
  name = G4_BGO
  specific = 4
FEATURE [App::DocumentObjectGroupPython] H_element014  label="H_element : 0.102"  # scripted group (container) (typed FeaturePython)
  n = 0.102
FEATURE [App::DocumentObjectGroupPython] C_element014  label="C_element : 0.110"  # scripted group (container) (typed FeaturePython)
  n = 0.11
FEATURE [App::DocumentObjectGroupPython] N_element009  label="N_element : 0.033"  # scripted group (container) (typed FeaturePython)
  n = 0.033
FEATURE [App::DocumentObjectGroupPython] O_element013  label="O_element : 0.745"  # scripted group (container) (typed FeaturePython)
  n = 0.745
FEATURE [App::DocumentObjectGroupPython] Na_element002  label="Na_element : 0.002"  # scripted group (container) (typed FeaturePython)
  n = 0.001
FEATURE [App::DocumentObjectGroupPython] P_element001  label="P_element : 0.001"  # scripted group (container) (typed FeaturePython)
  n = 0.001
FEATURE [App::DocumentObjectGroupPython] S_element003  label="S_element : 0.002"  # scripted group (container) (typed FeaturePython)
  n = 0.002
FEATURE [App::DocumentObjectGroupPython] Cl_element002  label="Cl_element : 0.003"  # scripted group (container) (typed FeaturePython)
  n = 0.003
FEATURE [App::DocumentObjectGroupPython] K_element001  label="K_element : 0.002"  # scripted group (container) (typed FeaturePython)
  n = 0.002
FEATURE [App::DocumentObjectGroupPython] Fe_element001  label="Fe_element : 0.001"  # scripted group (container) (typed FeaturePython)
  n = 0.001
FEATURE [App::DocumentObjectGroupPython] G4_BLOOD_ICRP  # scripted group (container) (typed FeaturePython)
  Dunit = g/cm3
  Dvalue = 1.06
  Group = -> [H_element014,C_element014,N_element009,O_element013,Na_element002,P_element001,S_element003,Cl_element002,K_element001,Fe_element001]
  conduct = 2
  density = 1
  expand = 3
  formula = G4_BLOOD_ICRP
  name = G4_BLOOD_ICRP
  specific = 4
FEATURE [App::DocumentObjectGroupPython] H_element015  label="H_element : 0.064"  # scripted group (container) (typed FeaturePython)
  n = 0.064
FEATURE [App::DocumentObjectGroupPython] C_element015  label="C_element : 0.278"  # scripted group (container) (typed FeaturePython)
  n = 0.278
FEATURE [App::DocumentObjectGroupPython] N_element010  label="N_element : 0.027"  # scripted group (container) (typed FeaturePython)
  n = 0.027
FEATURE [App::DocumentObjectGroupPython] O_element014  label="O_element : 0.410"  # scripted group (container) (typed FeaturePython)
  n = 0.41
FEATURE [App::DocumentObjectGroupPython] Mg_element001  label="Mg_element : 0.002"  # scripted group (container) (typed FeaturePython)
  n = 0.002
FEATURE [App::DocumentObjectGroupPython] P_element002  label="P_element : 0.070"  # scripted group (container) (typed FeaturePython)
  n = 0.07
FEATURE [App::DocumentObjectGroupPython] S_element004  label="S_element : 0.003"  # scripted group (container) (typed FeaturePython)
  n = 0.002
FEATURE [App::DocumentObjectGroupPython] Ca_element003  label="Ca_element : 0.147"  # scripted group (container) (typed FeaturePython)
  n = 0.147
FEATURE [App::DocumentObjectGroupPython] G4_BONE_COMPACT_ICRU  # scripted group (container) (typed FeaturePython)
  Dunit = g/cm3
  Dvalue = 1.85
  Group = -> [H_element015,C_element015,N_element010,O_element014,Mg_element001,P_element002,S_element004,Ca_element003]
  conduct = 2
  density = 1
  expand = 3
  formula = G4_BONE_COMPACT_ICRU
  name = G4_BONE_COMPACT_ICRU
  specific = 4
FEATURE [App::DocumentObjectGroupPython] H_element016  label="H_element : 0.034"  # scripted group (container) (typed FeaturePython)
  n = 0.034
FEATURE [App::DocumentObjectGroupPython] C_element016  label="C_element : 0.155"  # scripted group (container) (typed FeaturePython)
  n = 0.155
FEATURE [App::DocumentObjectGroupPython] N_element011  label="N_element : 0.042"  # scripted group (container) (typed FeaturePython)
  n = 0.042
FEATURE [App::DocumentObjectGroupPython] O_element015  label="O_element : 0.435"  # scripted group (container) (typed FeaturePython)
  n = 0.435
FEATURE [App::DocumentObjectGroupPython] Na_element003  label="Na_element : 0.003"  # scripted group (container) (typed FeaturePython)
  n = 0.001
FEATURE [App::DocumentObjectGroupPython] Mg_element002  label="Mg_element : 0.003"  # scripted group (container) (typed FeaturePython)
  n = 0.002
FEATURE [App::DocumentObjectGroupPython] P_element003  label="P_element : 0.103"  # scripted group (container) (typed FeaturePython)
  n = 0.103
FEATURE [App::DocumentObjectGroupPython] S_element005  label="S_element : 0.004"  # scripted group (container) (typed FeaturePython)
  n = 0.003
FEATURE [App::DocumentObjectGroupPython] Ca_element004  label="Ca_element : 0.225"  # scripted group (container) (typed FeaturePython)
  n = 0.225
FEATURE [App::DocumentObjectGroupPython] G4_BONE_CORTICAL_ICRP  # scripted group (container) (typed FeaturePython)
  Dunit = g/cm3
  Dvalue = 1.92
  Group = -> [H_element016,C_element016,N_element011,O_element015,Na_element003,Mg_element002,P_element003,S_element005,Ca_element004]
  conduct = 2
  density = 1
  expand = 3
  formula = G4_BONE_CORTICAL_ICRP
  name = G4_BONE_CORTICAL_ICRP
  specific = 4
FEATURE [App::DocumentObjectGroupPython] B_element001  label="B_element : 4"  # scripted group (container) (typed FeaturePython)
  n = 4
  ref = B_element
FEATURE [App::DocumentObjectGroupPython] C_element017  label="C_element : 1"  # scripted group (container) (typed FeaturePython)
  n = 1
  ref = C_element
FEATURE [App::DocumentObjectGroupPython] G4_BORON_CARBIDE  # scripted group (container) (typed FeaturePython)
  Dunit = g/cm3
  Dvalue = 2.52
  Group = -> [B_element001,C_element017]
  conduct = 2
  density = 1
  expand = 3
  formula = G4_BORON_CARBIDE
  name = G4_BORON_CARBIDE
  specific = 4
FEATURE [App::DocumentObjectGroupPython] B_element002  label="B_element : 2"  # scripted group (container) (typed FeaturePython)
  n = 2
  ref = B_element
FEATURE [App::DocumentObjectGroupPython] O_element016  label="O_element : 006"  # scripted group (container) (typed FeaturePython)
  n = 3
  ref = O_element
FEATURE [App::DocumentObjectGroupPython] G4_BORON_OXIDE  # scripted group (container) (typed FeaturePython)
  Dunit = g/cm3
  Dvalue = 1.812
  Group = -> [B_element002,O_element016]
  conduct = 2
  density = 1
  expand = 3
  formula = G4_BORON_OXIDE
  name = G4_BORON_OXIDE
  specific = 4
FEATURE [App::DocumentObjectGroupPython] H_element017  label="H_element : 0.107"  # scripted group (container) (typed FeaturePython)
  n = 0.107
FEATURE [App::DocumentObjectGroupPython] C_element018  label="C_element : 0.145"  # scripted group (container) (typed FeaturePython)
  n = 0.145
FEATURE [App::DocumentObjectGroupPython] N_element012  label="N_element : 0.022"  # scripted group (container) (typed FeaturePython)
  n = 0.022
FEATURE [App::DocumentObjectGroupPython] O_element017  label="O_element : 0.712"  # scripted group (container) (typed FeaturePython)
  n = 0.712
FEATURE [App::DocumentObjectGroupPython] Na_element004  label="Na_element : 0.004"  # scripted group (container) (typed FeaturePython)
  n = 0.002
FEATURE [App::DocumentObjectGroupPython] P_element004  label="P_element : 0.004"  # scripted group (container) (typed FeaturePython)
  n = 0.004
FEATURE [App::DocumentObjectGroupPython] S_element006  label="S_element : 0.005"  # scripted group (container) (typed FeaturePython)
  n = 0.002
FEATURE [App::DocumentObjectGroupPython] Cl_element003  label="Cl_element : 0.004"  # scripted group (container) (typed FeaturePython)
  n = 0.003
FEATURE [App::DocumentObjectGroupPython] K_element002  label="K_element : 0.003"  # scripted group (container) (typed FeaturePython)
  n = 0.003
FEATURE [App::DocumentObjectGroupPython] G4_BRAIN_ICRP  # scripted group (container) (typed FeaturePython)
  Dunit = g/cm3
  Dvalue = 1.04
  Group = -> [H_element017,C_element018,N_element012,O_element017,Na_element004,P_element004,S_element006,Cl_element003,K_element002]
  conduct = 2
  density = 1
  expand = 3
  formula = G4_BRAIN_ICRP
  name = G4_BRAIN_ICRP
  specific = 4
FEATURE [App::DocumentObjectGroupPython] C_element019  label="C_element : 4"  # scripted group (container) (typed FeaturePython)
  n = 4
  ref = C_element
FEATURE [App::DocumentObjectGroupPython] H_element018  label="H_element : 010"  # scripted group (container) (typed FeaturePython)
  n = 10
  ref = H_element
FEATURE [App::DocumentObjectGroupPython] G4_BUTANE  # scripted group (container) (typed FeaturePython)
  Dunit = g/cm3
  Dvalue = 0.00249343
  Group = -> [C_element019,H_element018]
  conduct = 2
  density = 1
  expand = 3
  formula = G4_BUTANE
  name = G4_BUTANE
  specific = 4
FEATURE [App::DocumentObjectGroupPython] C_element020  label="C_element : 008"  # scripted group (container) (typed FeaturePython)
  n = 4
  ref = C_element
FEATURE [App::DocumentObjectGroupPython] H_element019  label="H_element : 011"  # scripted group (container) (typed FeaturePython)
  n = 10
  ref = H_element
FEATURE [App::DocumentObjectGroupPython] O_element018  label="O_element : 007"  # scripted group (container) (typed FeaturePython)
  n = 1
  ref = O_element
FEATURE [App::DocumentObjectGroupPython] G4_N_BUTYL_ALCOHOL  label="G4_N-BUTYL_ALCOHOL"  # scripted group (container) (typed FeaturePython)
  Dunit = g/cm3
  Dvalue = 0.8098
  Group = -> [C_element020,H_element019,O_element018]
  conduct = 2
  density = 1
  expand = 3
  formula = G4_N-BUTYL_ALCOHOL
  name = G4_N-BUTYL_ALCOHOL
  specific = 4
FEATURE [App::DocumentObjectGroupPython] H_element020  label="H_element : 0.025"  # scripted group (container) (typed FeaturePython)
  n = 0.02468
FEATURE [App::DocumentObjectGroupPython] C_element021  label="C_element : 0.502"  # scripted group (container) (typed FeaturePython)
  n = 0.501611
FEATURE [App::DocumentObjectGroupPython] O_element019  label="O_element : 0.005"  # scripted group (container) (typed FeaturePython)
  n = 0.004527
FEATURE [App::DocumentObjectGroupPython] F_element004  label="F_element : 0.465"  # scripted group (container) (typed FeaturePython)
  n = 0.465209
FEATURE [App::DocumentObjectGroupPython] Si_element001  label="Si_element : 0.004"  # scripted group (container) (typed FeaturePython)
  n = 0.003973
FEATURE [App::DocumentObjectGroupPython] G4_C_552  label="G4_C-552"  # scripted group (container) (typed FeaturePython)
  Dunit = g/cm3
  Dvalue = 1.76
  Group = -> [H_element020,C_element021,O_element019,F_element004,Si_element001]
  conduct = 2
  density = 1
  expand = 3
  formula = G4_C-552
  name = G4_C-552
  specific = 4
FEATURE [App::DocumentObjectGroupPython] Cd_element001  label="Cd_element : 1"  # scripted group (container) (typed FeaturePython)
  n = 1
  ref = Cd_element
FEATURE [App::DocumentObjectGroupPython] Te_element001  label="Te_element : 1"  # scripted group (container) (typed FeaturePython)
  n = 1
  ref = Te_element
FEATURE [App::DocumentObjectGroupPython] G4_CADMIUM_TELLURIDE  # scripted group (container) (typed FeaturePython)
  Dunit = g/cm3
  Dvalue = 6.2
  Group = -> [Cd_element001,Te_element001]
  conduct = 2
  density = 1
  expand = 3
  formula = G4_CADMIUM_TELLURIDE
  name = G4_CADMIUM_TELLURIDE
  specific = 4
FEATURE [App::DocumentObjectGroupPython] Cd_element002  label="Cd_element : 002"  # scripted group (container) (typed FeaturePython)
  n = 1
  ref = Cd_element
FEATURE [App::DocumentObjectGroupPython] W_element001  label="W_element : 1"  # scripted group (container) (typed FeaturePython)
  n = 1
  ref = W_element
FEATURE [App::DocumentObjectGroupPython] O_element020  label="O_element : 008"  # scripted group (container) (typed FeaturePython)
  n = 4
  ref = O_element
FEATURE [App::DocumentObjectGroupPython] G4_CADMIUM_TUNGSTATE  # scripted group (container) (typed FeaturePython)
  Dunit = g/cm3
  Dvalue = 7.9
  Group = -> [Cd_element002,W_element001,O_element020]
  conduct = 2
  density = 1
  expand = 3
  formula = G4_CADMIUM_TUNGSTATE
  name = G4_CADMIUM_TUNGSTATE
  specific = 4
FEATURE [App::DocumentObjectGroupPython] Ca_element005  label="Ca_element : 1"  # scripted group (container) (typed FeaturePython)
  n = 1
  ref = Ca_element
FEATURE [App::DocumentObjectGroupPython] C_element022  label="C_element : 009"  # scripted group (container) (typed FeaturePython)
  n = 1
  ref = C_element
FEATURE [App::DocumentObjectGroupPython] O_element021  label="O_element : 009"  # scripted group (container) (typed FeaturePython)
  n = 3
  ref = O_element
FEATURE [App::DocumentObjectGroupPython] G4_CALCIUM_CARBONATE  # scripted group (container) (typed FeaturePython)
  Dunit = g/cm3
  Dvalue = 2.8
  Group = -> [Ca_element005,C_element022,O_element021]
  conduct = 2
  density = 1
  expand = 3
  formula = G4_CALCIUM_CARBONATE
  name = G4_CALCIUM_CARBONATE
  specific = 4
FEATURE [App::DocumentObjectGroupPython] Ca_element006  label="Ca_element : 002"  # scripted group (container) (typed FeaturePython)
  n = 1
  ref = Ca_element
FEATURE [App::DocumentObjectGroupPython] F_element005  label="F_element : 003"  # scripted group (container) (typed FeaturePython)
  n = 2
  ref = F_element
FEATURE [App::DocumentObjectGroupPython] G4_CALCIUM_FLUORIDE  # scripted group (container) (typed FeaturePython)
  Dunit = g/cm3
  Dvalue = 3.18
  Group = -> [Ca_element006,F_element005]
  conduct = 2
  density = 1
  expand = 3
  formula = G4_CALCIUM_FLUORIDE
  name = G4_CALCIUM_FLUORIDE
  specific = 4
FEATURE [App::DocumentObjectGroupPython] Ca_element007  label="Ca_element : 003"  # scripted group (container) (typed FeaturePython)
  n = 1
  ref = Ca_element
FEATURE [App::DocumentObjectGroupPython] O_element022  label="O_element : 010"  # scripted group (container) (typed FeaturePython)
  n = 1
  ref = O_element
FEATURE [App::DocumentObjectGroupPython] G4_CALCIUM_OXIDE  # scripted group (container) (typed FeaturePython)
  Dunit = g/cm3
  Dvalue = 3.3
  Group = -> [Ca_element007,O_element022]
  conduct = 2
  density = 1
  expand = 3
  formula = G4_CALCIUM_OXIDE
  name = G4_CALCIUM_OXIDE
  specific = 4
FEATURE [App::DocumentObjectGroupPython] Ca_element008  label="Ca_element : 004"  # scripted group (container) (typed FeaturePython)
  n = 1
  ref = Ca_element
FEATURE [App::DocumentObjectGroupPython] S_element007  label="S_element : 002"  # scripted group (container) (typed FeaturePython)
  n = 1
  ref = S_element
FEATURE [App::DocumentObjectGroupPython] O_element023  label="O_element : 011"  # scripted group (container) (typed FeaturePython)
  n = 4
  ref = O_element
FEATURE [App::DocumentObjectGroupPython] G4_CALCIUM_SULFATE  # scripted group (container) (typed FeaturePython)
  Dunit = g/cm3
  Dvalue = 2.96
  Group = -> [Ca_element008,S_element007,O_element023]
  conduct = 2
  density = 1
  expand = 3
  formula = G4_CALCIUM_SULFATE
  name = G4_CALCIUM_SULFATE
  specific = 4
FEATURE [App::DocumentObjectGroupPython] Ca_element009  label="Ca_element : 005"  # scripted group (container) (typed FeaturePython)
  n = 1
  ref = Ca_element
FEATURE [App::DocumentObjectGroupPython] W_element002  label="W_element : 002"  # scripted group (container) (typed FeaturePython)
  n = 1
  ref = W_element
FEATURE [App::DocumentObjectGroupPython] O_element024  label="O_element : 012"  # scripted group (container) (typed FeaturePython)
  n = 4
  ref = O_element
FEATURE [App::DocumentObjectGroupPython] G4_CALCIUM_TUNGSTATE  # scripted group (container) (typed FeaturePython)
  Dunit = g/cm3
  Dvalue = 6.062
  Group = -> [Ca_element009,W_element002,O_element024]
  conduct = 2
  density = 1
  expand = 3
  formula = G4_CALCIUM_TUNGSTATE
  name = G4_CALCIUM_TUNGSTATE
  specific = 4
FEATURE [App::DocumentObjectGroupPython] C_element023  label="C_element : 010"  # scripted group (container) (typed FeaturePython)
  n = 1
  ref = C_element
FEATURE [App::DocumentObjectGroupPython] O_element025  label="O_element : 013"  # scripted group (container) (typed FeaturePython)
  n = 2
  ref = O_element
FEATURE [App::DocumentObjectGroupPython] G4_CARBON_DIOXIDE  # scripted group (container) (typed FeaturePython)
  Dunit = g/cm3
  Dvalue = 0.00184212
  Group = -> [C_element023,O_element025]
  conduct = 2
  density = 1
  expand = 3
  formula = G4_CARBON_DIOXIDE
  name = G4_CARBON_DIOXIDE
  specific = 4
FEATURE [App::DocumentObjectGroupPython] C_element024  label="C_element : 011"  # scripted group (container) (typed FeaturePython)
  n = 1
  ref = C_element
FEATURE [App::DocumentObjectGroupPython] Cl_element004  label="Cl_element : 4"  # scripted group (container) (typed FeaturePython)
  n = 4
  ref = Cl_element
FEATURE [App::DocumentObjectGroupPython] G4_CARBON_TETRACHLORIDE  # scripted group (container) (typed FeaturePython)
  Dunit = g/cm3
  Dvalue = 1.594
  Group = -> [C_element024,Cl_element004]
  conduct = 2
  density = 1
  expand = 3
  formula = G4_CARBON_TETRACHLORIDE
  name = G4_CARBON_TETRACHLORIDE
  specific = 4
FEATURE [App::DocumentObjectGroupPython] C_element025  label="C_element : 012"  # scripted group (container) (typed FeaturePython)
  n = 6
  ref = C_element
FEATURE [App::DocumentObjectGroupPython] H_element021  label="H_element : 012"  # scripted group (container) (typed FeaturePython)
  n = 10
  ref = H_element
FEATURE [App::DocumentObjectGroupPython] O_element026  label="O_element : 5"  # scripted group (container) (typed FeaturePython)
  n = 5
  ref = O_element
FEATURE [App::DocumentObjectGroupPython] G4_CELLULOSE_CELLOPHANE  # scripted group (container) (typed FeaturePython)
  Dunit = g/cm3
  Dvalue = 1.42
  Group = -> [C_element025,H_element021,O_element026]
  conduct = 2
  density = 1
  expand = 3
  formula = G4_CELLULOSE_CELLOPHANE
  name = G4_CELLULOSE_CELLOPHANE
  specific = 4
FEATURE [App::DocumentObjectGroupPython] H_element022  label="H_element : 0.067"  # scripted group (container) (typed FeaturePython)
  n = 0.067125
FEATURE [App::DocumentObjectGroupPython] C_element026  label="C_element : 0.545"  # scripted group (container) (typed FeaturePython)
  n = 0.545403
FEATURE [App::DocumentObjectGroupPython] O_element027  label="O_element : 0.387"  # scripted group (container) (typed FeaturePython)
  n = 0.387472
FEATURE [App::DocumentObjectGroupPython] G4_CELLULOSE_BUTYRATE  # scripted group (container) (typed FeaturePython)
  Dunit = g/cm3
  Dvalue = 1.2
  Group = -> [H_element022,C_element026,O_element027]
  conduct = 2
  density = 1
  expand = 3
  formula = G4_CELLULOSE_BUTYRATE
  name = G4_CELLULOSE_BUTYRATE
  specific = 4
FEATURE [App::DocumentObjectGroupPython] H_element023  label="H_element : 0.029"  # scripted group (container) (typed FeaturePython)
  n = 0.029216
FEATURE [App::DocumentObjectGroupPython] C_element027  label="C_element : 0.271"  # scripted group (container) (typed FeaturePython)
  n = 0.271296
FEATURE [App::DocumentObjectGroupPython] N_element013  label="N_element : 0.121"  # scripted group (container) (typed FeaturePython)
  n = 0.121276
FEATURE [App::DocumentObjectGroupPython] O_element028  label="O_element : 0.578"  # scripted group (container) (typed FeaturePython)
  n = 0.578212
FEATURE [App::DocumentObjectGroupPython] G4_CELLULOSE_NITRATE  # scripted group (container) (typed FeaturePython)
  Dunit = g/cm3
  Dvalue = 1.49
  Group = -> [H_element023,C_element027,N_element013,O_element028]
  conduct = 2
  density = 1
  expand = 3
  formula = G4_CELLULOSE_NITRATE
  name = G4_CELLULOSE_NITRATE
  specific = 4
FEATURE [App::DocumentObjectGroupPython] H_element024  label="H_element : 0.108"  # scripted group (container) (typed FeaturePython)
  n = 0.107596
FEATURE [App::DocumentObjectGroupPython] N_element014  label="N_element : 0.001"  # scripted group (container) (typed FeaturePython)
  n = 0.0008
FEATURE [App::DocumentObjectGroupPython] O_element029  label="O_element : 0.875"  # scripted group (container) (typed FeaturePython)
  n = 0.874976
FEATURE [App::DocumentObjectGroupPython] S_element008  label="S_element : 0.015"  # scripted group (container) (typed FeaturePython)
  n = 0.014627
FEATURE [App::DocumentObjectGroupPython] Ce_element001  label="Ce_element : 0.002"  # scripted group (container) (typed FeaturePython)
  n = 0.002001
FEATURE [App::DocumentObjectGroupPython] G4_CERIC_SULFATE  # scripted group (container) (typed FeaturePython)
  Dunit = g/cm3
  Dvalue = 1.03
  Group = -> [H_element024,N_element014,O_element029,S_element008,Ce_element001]
  conduct = 2
  density = 1
  expand = 3
  formula = G4_CERIC_SULFATE
  name = G4_CERIC_SULFATE
  specific = 4
FEATURE [App::DocumentObjectGroupPython] Cs_element001  label="Cs_element : 1"  # scripted group (container) (typed FeaturePython)
  n = 1
  ref = Cs_element
FEATURE [App::DocumentObjectGroupPython] F_element006  label="F_element : 1"  # scripted group (container) (typed FeaturePython)
  n = 1
  ref = F_element
FEATURE [App::DocumentObjectGroupPython] G4_CESIUM_FLUORIDE  # scripted group (container) (typed FeaturePython)
  Dunit = g/cm3
  Dvalue = 4.115
  Group = -> [Cs_element001,F_element006]
  conduct = 2
  density = 1
  expand = 3
  formula = G4_CESIUM_FLUORIDE
  name = G4_CESIUM_FLUORIDE
  specific = 4
FEATURE [App::DocumentObjectGroupPython] Cs_element002  label="Cs_element : 002"  # scripted group (container) (typed FeaturePython)
  n = 1
  ref = Cs_element
FEATURE [App::DocumentObjectGroupPython] I_element001  label="I_element : 1"  # scripted group (container) (typed FeaturePython)
  n = 1
  ref = I_element
FEATURE [App::DocumentObjectGroupPython] G4_CESIUM_IODIDE  # scripted group (container) (typed FeaturePython)
  Dunit = g/cm3
  Dvalue = 4.51
  Group = -> [Cs_element002,I_element001]
  conduct = 2
  density = 1
  expand = 3
  formula = G4_CESIUM_IODIDE
  name = G4_CESIUM_IODIDE
  specific = 4
FEATURE [App::DocumentObjectGroupPython] C_element028  label="C_element : 013"  # scripted group (container) (typed FeaturePython)
  n = 6
  ref = C_element
FEATURE [App::DocumentObjectGroupPython] H_element025  label="H_element : 013"  # scripted group (container) (typed FeaturePython)
  n = 5
  ref = H_element
FEATURE [App::DocumentObjectGroupPython] Cl_element005  label="Cl_element : 1"  # scripted group (container) (typed FeaturePython)
  n = 1
  ref = Cl_element
FEATURE [App::DocumentObjectGroupPython] G4_CHLOROBENZENE  # scripted group (container) (typed FeaturePython)
  Dunit = g/cm3
  Dvalue = 1.1058
  Group = -> [C_element028,H_element025,Cl_element005]
  conduct = 2
  density = 1
  expand = 3
  formula = G4_CHLOROBENZENE
  name = G4_CHLOROBENZENE
  specific = 4
FEATURE [App::DocumentObjectGroupPython] C_element029  label="C_element : 014"  # scripted group (container) (typed FeaturePython)
  n = 1
  ref = C_element
FEATURE [App::DocumentObjectGroupPython] H_element026  label="H_element : 1"  # scripted group (container) (typed FeaturePython)
  n = 1
  ref = H_element
FEATURE [App::DocumentObjectGroupPython] Cl_element006  label="Cl_element : 3"  # scripted group (container) (typed FeaturePython)
  n = 3
  ref = Cl_element
FEATURE [App::DocumentObjectGroupPython] G4_CHLOROFORM  # scripted group (container) (typed FeaturePython)
  Dunit = g/cm3
  Dvalue = 1.4832
  Group = -> [C_element029,H_element026,Cl_element006]
  conduct = 2
  density = 1
  expand = 3
  formula = G4_CHLOROFORM
  name = G4_CHLOROFORM
  specific = 4
FEATURE [App::DocumentObjectGroupPython] H_element027  label="H_element : 0.010"  # scripted group (container) (typed FeaturePython)
  n = 0.01
FEATURE [App::DocumentObjectGroupPython] C_element030  label="C_element : 0.001"  # scripted group (container) (typed FeaturePython)
  n = 0.001
FEATURE [App::DocumentObjectGroupPython] O_element030  label="O_element : 0.529"  # scripted group (container) (typed FeaturePython)
  n = 0.529107
FEATURE [App::DocumentObjectGroupPython] Na_element005  label="Na_element : 0.016"  # scripted group (container) (typed FeaturePython)
  n = 0.016
FEATURE [App::DocumentObjectGroupPython] Mg_element003  label="Mg_element : 0.004"  # scripted group (container) (typed FeaturePython)
  n = 0.002
FEATURE [App::DocumentObjectGroupPython] Al_element002  label="Al_element : 0.034"  # scripted group (container) (typed FeaturePython)
  n = 0.033872
FEATURE [App::DocumentObjectGroupPython] Si_element002  label="Si_element : 0.337"  # scripted group (container) (typed FeaturePython)
  n = 0.337021
FEATURE [App::DocumentObjectGroupPython] K_element003  label="K_element : 0.013"  # scripted group (container) (typed FeaturePython)
  n = 0.013
FEATURE [App::DocumentObjectGroupPython] Ca_element010  label="Ca_element : 0.044"  # scripted group (container) (typed FeaturePython)
  n = 0.044
FEATURE [App::DocumentObjectGroupPython] Fe_element002  label="Fe_element : 0.014"  # scripted group (container) (typed FeaturePython)
  n = 0.014
FEATURE [App::DocumentObjectGroupPython] G4_CONCRETE  # scripted group (container) (typed FeaturePython)
  Dunit = g/cm3
  Dvalue = 2.3
  Group = -> [H_element027,C_element030,O_element030,Na_element005,Mg_element003,Al_element002,Si_element002,K_element003,Ca_element010,Fe_element002]
  conduct = 2
  density = 1
  expand = 3
  formula = G4_CONCRETE
  name = G4_CONCRETE
  specific = 4
FEATURE [App::DocumentObjectGroupPython] C_element031  label="C_element : 015"  # scripted group (container) (typed FeaturePython)
  n = 6
  ref = C_element
FEATURE [App::DocumentObjectGroupPython] H_element028  label="H_element : 12"  # scripted group (container) (typed FeaturePython)
  n = 12
  ref = H_element
FEATURE [App::DocumentObjectGroupPython] G4_CYCLOHEXANE  # scripted group (container) (typed FeaturePython)
  Dunit = g/cm3
  Dvalue = 0.779
  Group = -> [C_element031,H_element028]
  conduct = 2
  density = 1
  expand = 3
  formula = G4_CYCLOHEXANE
  name = G4_CYCLOHEXANE
  specific = 4
FEATURE [App::DocumentObjectGroupPython] C_element032  label="C_element : 016"  # scripted group (container) (typed FeaturePython)
  n = 6
  ref = C_element
FEATURE [App::DocumentObjectGroupPython] H_element029  label="H_element : 4"  # scripted group (container) (typed FeaturePython)
  n = 4
  ref = H_element
FEATURE [App::DocumentObjectGroupPython] Cl_element007  label="Cl_element : 2"  # scripted group (container) (typed FeaturePython)
  n = 2
  ref = Cl_element
FEATURE [App::DocumentObjectGroupPython] G4_1_2_DICHLOROBENZENE  label="G4_1.2-DICHLOROBENZENE"  # scripted group (container) (typed FeaturePython)
  Dunit = g/cm3
  Dvalue = 1.3048
  Group = -> [C_element032,H_element029,Cl_element007]
  conduct = 2
  density = 1
  expand = 3
  formula = G4_1.2-DICHLOROBENZENE
  name = G4_1.2-DICHLOROBENZENE
  specific = 4
FEATURE [App::DocumentObjectGroupPython] C_element033  label="C_element : 017"  # scripted group (container) (typed FeaturePython)
  n = 4
  ref = C_element
FEATURE [App::DocumentObjectGroupPython] H_element030  label="H_element : 8"  # scripted group (container) (typed FeaturePython)
  n = 8
  ref = H_element
FEATURE [App::DocumentObjectGroupPython] O_element031  label="O_element : 014"  # scripted group (container) (typed FeaturePython)
  n = 1
  ref = O_element
FEATURE [App::DocumentObjectGroupPython] Cl_element008  label="Cl_element : 005"  # scripted group (container) (typed FeaturePython)
  n = 2
  ref = Cl_element
FEATURE [App::DocumentObjectGroupPython] G4_DICHLORODIETHYL_ETHER  # scripted group (container) (typed FeaturePython)
  Dunit = g/cm3
  Dvalue = 1.2199
  Group = -> [C_element033,H_element030,O_element031,Cl_element008]
  conduct = 2
  density = 1
  expand = 3
  formula = G4_DICHLORODIETHYL_ETHER
  name = G4_DICHLORODIETHYL_ETHER
  specific = 4
FEATURE [App::DocumentObjectGroupPython] C_element034  label="C_element : 018"  # scripted group (container) (typed FeaturePython)
  n = 2
  ref = C_element
FEATURE [App::DocumentObjectGroupPython] H_element031  label="H_element : 014"  # scripted group (container) (typed FeaturePython)
  n = 4
  ref = H_element
FEATURE [App::DocumentObjectGroupPython] Cl_element009  label="Cl_element : 006"  # scripted group (container) (typed FeaturePython)
  n = 2
  ref = Cl_element
FEATURE [App::DocumentObjectGroupPython] G4_1_2_DICHLOROETHANE  label="G4_1.2-DICHLOROETHANE"  # scripted group (container) (typed FeaturePython)
  Dunit = g/cm3
  Dvalue = 1.2351
  Group = -> [C_element034,H_element031,Cl_element009]
  conduct = 2
  density = 1
  expand = 3
  formula = G4_1.2-DICHLOROETHANE
  name = G4_1.2-DICHLOROETHANE
  specific = 4
FEATURE [App::DocumentObjectGroupPython] C_element035  label="C_element : 019"  # scripted group (container) (typed FeaturePython)
  n = 4
  ref = C_element
FEATURE [App::DocumentObjectGroupPython] H_element032  label="H_element : 015"  # scripted group (container) (typed FeaturePython)
  n = 10
  ref = H_element
FEATURE [App::DocumentObjectGroupPython] O_element032  label="O_element : 015"  # scripted group (container) (typed FeaturePython)
  n = 1
  ref = O_element
FEATURE [App::DocumentObjectGroupPython] G4_DIETHYL_ETHER  # scripted group (container) (typed FeaturePython)
  Dunit = g/cm3
  Dvalue = 0.71378
  Group = -> [C_element035,H_element032,O_element032]
  conduct = 2
  density = 1
  expand = 3
  formula = G4_DIETHYL_ETHER
  name = G4_DIETHYL_ETHER
  specific = 4
FEATURE [App::DocumentObjectGroupPython] C_element036  label="C_element : 020"  # scripted group (container) (typed FeaturePython)
  n = 3
  ref = C_element
FEATURE [App::DocumentObjectGroupPython] H_element033  label="H_element : 016"  # scripted group (container) (typed FeaturePython)
  n = 7
  ref = H_element
FEATURE [App::DocumentObjectGroupPython] N_element015  label="N_element : 008"  # scripted group (container) (typed FeaturePython)
  n = 1
  ref = N_element
FEATURE [App::DocumentObjectGroupPython] O_element033  label="O_element : 016"  # scripted group (container) (typed FeaturePython)
  n = 1
  ref = O_element
FEATURE [App::DocumentObjectGroupPython] G4_N_N_DIMETHYL_FORMAMIDE  label="G4_N.N-DIMETHYL_FORMAMIDE"  # scripted group (container) (typed FeaturePython)
  Dunit = g/cm3
  Dvalue = 0.9487
  Group = -> [C_element036,H_element033,N_element015,O_element033]
  conduct = 2
  density = 1
  expand = 3
  formula = G4_N.N-DIMETHYL_FORMAMIDE
  name = G4_N.N-DIMETHYL_FORMAMIDE
  specific = 4
FEATURE [App::DocumentObjectGroupPython] C_element037  label="C_element : 021"  # scripted group (container) (typed FeaturePython)
  n = 2
  ref = C_element
FEATURE [App::DocumentObjectGroupPython] H_element034  label="H_element : 017"  # scripted group (container) (typed FeaturePython)
  n = 6
  ref = H_element
FEATURE [App::DocumentObjectGroupPython] O_element034  label="O_element : 017"  # scripted group (container) (typed FeaturePython)
  n = 1
  ref = O_element
FEATURE [App::DocumentObjectGroupPython] S_element009  label="S_element : 003"  # scripted group (container) (typed FeaturePython)
  n = 1
  ref = S_element
FEATURE [App::DocumentObjectGroupPython] G4_DIMETHYL_SULFOXIDE  # scripted group (container) (typed FeaturePython)
  Dunit = g/cm3
  Dvalue = 1.1014
  Group = -> [C_element037,H_element034,O_element034,S_element009]
  conduct = 2
  density = 1
  expand = 3
  formula = G4_DIMETHYL_SULFOXIDE
  name = G4_DIMETHYL_SULFOXIDE
  specific = 4
FEATURE [App::DocumentObjectGroupPython] C_element038  label="C_element : 022"  # scripted group (container) (typed FeaturePython)
  n = 2
  ref = C_element
FEATURE [App::DocumentObjectGroupPython] H_element035  label="H_element : 018"  # scripted group (container) (typed FeaturePython)
  n = 6
  ref = H_element
FEATURE [App::DocumentObjectGroupPython] G4_ETHANE  # scripted group (container) (typed FeaturePython)
  Dunit = g/cm3
  Dvalue = 0.00125324
  Group = -> [C_element038,H_element035]
  conduct = 2
  density = 1
  expand = 3
  formula = G4_ETHANE
  name = G4_ETHANE
  specific = 4
FEATURE [App::DocumentObjectGroupPython] C_element039  label="C_element : 023"  # scripted group (container) (typed FeaturePython)
  n = 2
  ref = C_element
FEATURE [App::DocumentObjectGroupPython] H_element036  label="H_element : 019"  # scripted group (container) (typed FeaturePython)
  n = 6
  ref = H_element
FEATURE [App::DocumentObjectGroupPython] O_element035  label="O_element : 018"  # scripted group (container) (typed FeaturePython)
  n = 1
  ref = O_element
FEATURE [App::DocumentObjectGroupPython] G4_ETHYL_ALCOHOL  # scripted group (container) (typed FeaturePython)
  Dunit = g/cm3
  Dvalue = 0.7893
  Group = -> [C_element039,H_element036,O_element035]
  conduct = 2
  density = 1
  expand = 3
  formula = G4_ETHYL_ALCOHOL
  name = G4_ETHYL_ALCOHOL
  specific = 4
FEATURE [App::DocumentObjectGroupPython] H_element037  label="H_element : 0.090"  # scripted group (container) (typed FeaturePython)
  n = 0.090027
FEATURE [App::DocumentObjectGroupPython] C_element040  label="C_element : 0.585"  # scripted group (container) (typed FeaturePython)
  n = 0.585182
FEATURE [App::DocumentObjectGroupPython] O_element036  label="O_element : 0.325"  # scripted group (container) (typed FeaturePython)
  n = 0.324791
FEATURE [App::DocumentObjectGroupPython] G4_ETHYL_CELLULOSE  # scripted group (container) (typed FeaturePython)
  Dunit = g/cm3
  Dvalue = 1.13
  Group = -> [H_element037,C_element040,O_element036]
  conduct = 2
  density = 1
  expand = 3
  formula = G4_ETHYL_CELLULOSE
  name = G4_ETHYL_CELLULOSE
  specific = 4
FEATURE [App::DocumentObjectGroupPython] C_element041  label="C_element : 024"  # scripted group (container) (typed FeaturePython)
  n = 2
  ref = C_element
FEATURE [App::DocumentObjectGroupPython] H_element038  label="H_element : 020"  # scripted group (container) (typed FeaturePython)
  n = 4
  ref = H_element
FEATURE [App::DocumentObjectGroupPython] G4_ETHYLENE  # scripted group (container) (typed FeaturePython)
  Dunit = g/cm3
  Dvalue = 0.00117497
  Group = -> [C_element041,H_element038]
  conduct = 2
  density = 1
  expand = 3
  formula = G4_ETHYLENE
  name = G4_ETHYLENE
  specific = 4
FEATURE [App::DocumentObjectGroupPython] H_element039  label="H_element : 0.096"  # scripted group (container) (typed FeaturePython)
  n = 0.096
FEATURE [App::DocumentObjectGroupPython] C_element042  label="C_element : 0.195"  # scripted group (container) (typed FeaturePython)
  n = 0.195
FEATURE [App::DocumentObjectGroupPython] N_element016  label="N_element : 0.057"  # scripted group (container) (typed FeaturePython)
  n = 0.057
FEATURE [App::DocumentObjectGroupPython] O_element037  label="O_element : 0.646"  # scripted group (container) (typed FeaturePython)
  n = 0.646
FEATURE [App::DocumentObjectGroupPython] Na_element006  label="Na_element : 0.017"  # scripted group (container) (typed FeaturePython)
  n = 0.001
FEATURE [App::DocumentObjectGroupPython] P_element005  label="P_element : 0.104"  # scripted group (container) (typed FeaturePython)
  n = 0.001
FEATURE [App::DocumentObjectGroupPython] S_element010  label="S_element : 0.016"  # scripted group (container) (typed FeaturePython)
  n = 0.003
FEATURE [App::DocumentObjectGroupPython] Cl_element010  label="Cl_element : 0.005"  # scripted group (container) (typed FeaturePython)
  n = 0.001
FEATURE [App::DocumentObjectGroupPython] G4_EYE_LENS_ICRP  # scripted group (container) (typed FeaturePython)
  Dunit = g/cm3
  Dvalue = 1.07
  Group = -> [H_element039,C_element042,N_element016,O_element037,Na_element006,P_element005,S_element010,Cl_element010]
  conduct = 2
  density = 1
  expand = 3
  formula = G4_EYE_LENS_ICRP
  name = G4_EYE_LENS_ICRP
  specific = 4
FEATURE [App::DocumentObjectGroupPython] Fe_element003  label="Fe_element : 2"  # scripted group (container) (typed FeaturePython)
  n = 2
  ref = Fe_element
FEATURE [App::DocumentObjectGroupPython] O_element038  label="O_element : 019"  # scripted group (container) (typed FeaturePython)
  n = 3
  ref = O_element
FEATURE [App::DocumentObjectGroupPython] G4_FERRIC_OXIDE  # scripted group (container) (typed FeaturePython)
  Dunit = g/cm3
  Dvalue = 5.2
  Group = -> [Fe_element003,O_element038]
  conduct = 2
  density = 1
  expand = 3
  formula = G4_FERRIC_OXIDE
  name = G4_FERRIC_OXIDE
  specific = 4
FEATURE [App::DocumentObjectGroupPython] Fe_element004  label="Fe_element : 1"  # scripted group (container) (typed FeaturePython)
  n = 1
  ref = Fe_element
FEATURE [App::DocumentObjectGroupPython] B_element003  label="B_element : 1"  # scripted group (container) (typed FeaturePython)
  n = 1
  ref = B_element
FEATURE [App::DocumentObjectGroupPython] G4_FERROBORIDE  # scripted group (container) (typed FeaturePython)
  Dunit = g/cm3
  Dvalue = 7.15
  Group = -> [Fe_element004,B_element003]
  conduct = 2
  density = 1
  expand = 3
  formula = G4_FERROBORIDE
  name = G4_FERROBORIDE
  specific = 4
FEATURE [App::DocumentObjectGroupPython] Fe_element005  label="Fe_element : 003"  # scripted group (container) (typed FeaturePython)
  n = 1
  ref = Fe_element
FEATURE [App::DocumentObjectGroupPython] O_element039  label="O_element : 020"  # scripted group (container) (typed FeaturePython)
  n = 1
  ref = O_element
FEATURE [App::DocumentObjectGroupPython] G4_FERROUS_OXIDE  # scripted group (container) (typed FeaturePython)
  Dunit = g/cm3
  Dvalue = 5.7
  Group = -> [Fe_element005,O_element039]
  conduct = 2
  density = 1
  expand = 3
  formula = G4_FERROUS_OXIDE
  name = G4_FERROUS_OXIDE
  specific = 4
FEATURE [App::DocumentObjectGroupPython] H_element040  label="H_element : 0.115"  # scripted group (container) (typed FeaturePython)
  n = 0.108259
FEATURE [App::DocumentObjectGroupPython] N_element017  label="N_element : 0.000"  # scripted group (container) (typed FeaturePython)
  n = 2.7e-05
FEATURE [App::DocumentObjectGroupPython] O_element040  label="O_element : 0.879"  # scripted group (container) (typed FeaturePython)
  n = 0.878636
FEATURE [App::DocumentObjectGroupPython] Na_element007  label="Na_element : 0.000"  # scripted group (container) (typed FeaturePython)
  n = 2.2e-05
FEATURE [App::DocumentObjectGroupPython] S_element011  label="S_element : 0.013"  # scripted group (container) (typed FeaturePython)
  n = 0.012968
FEATURE [App::DocumentObjectGroupPython] Cl_element011  label="Cl_element : 0.000"  # scripted group (container) (typed FeaturePython)
  n = 3.4e-05
FEATURE [App::DocumentObjectGroupPython] Fe_element006  label="Fe_element : 0.000"  # scripted group (container) (typed FeaturePython)
  n = 5.4e-05
FEATURE [App::DocumentObjectGroupPython] G4_FERROUS_SULFATE  # scripted group (container) (typed FeaturePython)
  Dunit = g/cm3
  Dvalue = 1.024
  Group = -> [H_element040,N_element017,O_element040,Na_element007,S_element011,Cl_element011,Fe_element006]
  conduct = 2
  density = 1
  expand = 3
  formula = G4_FERROUS_SULFATE
  name = G4_FERROUS_SULFATE
  specific = 4
FEATURE [App::DocumentObjectGroupPython] C_element043  label="C_element : 0.099"  # scripted group (container) (typed FeaturePython)
  n = 0.099335
FEATURE [App::DocumentObjectGroupPython] F_element007  label="F_element : 0.314"  # scripted group (container) (typed FeaturePython)
  n = 0.314247
FEATURE [App::DocumentObjectGroupPython] Cl_element012  label="Cl_element : 0.586"  # scripted group (container) (typed FeaturePython)
  n = 0.586418
FEATURE [App::DocumentObjectGroupPython] G4_FREON_12  label="G4_FREON-12"  # scripted group (container) (typed FeaturePython)
  Dunit = g/cm3
  Dvalue = 1.12
  Group = -> [C_element043,F_element007,Cl_element012]
  conduct = 2
  density = 1
  expand = 3
  formula = G4_FREON-12
  name = G4_FREON-12
  specific = 4
FEATURE [App::DocumentObjectGroupPython] C_element044  label="C_element : 0.057"  # scripted group (container) (typed FeaturePython)
  n = 0.057245
FEATURE [App::DocumentObjectGroupPython] F_element008  label="F_element : 0.181"  # scripted group (container) (typed FeaturePython)
  n = 0.181096
FEATURE [App::DocumentObjectGroupPython] Br_element001  label="Br_element : 0.762"  # scripted group (container) (typed FeaturePython)
  n = 0.761659
FEATURE [App::DocumentObjectGroupPython] G4_FREON_12B2  label="G4_FREON-12B2"  # scripted group (container) (typed FeaturePython)
  Dunit = g/cm3
  Dvalue = 1.8
  Group = -> [C_element044,F_element008,Br_element001]
  conduct = 2
  density = 1
  expand = 3
  formula = G4_FREON-12B2
  name = G4_FREON-12B2
  specific = 4
FEATURE [App::DocumentObjectGroupPython] C_element045  label="C_element : 0.115"  # scripted group (container) (typed FeaturePython)
  n = 0.114983
FEATURE [App::DocumentObjectGroupPython] F_element009  label="F_element : 0.546"  # scripted group (container) (typed FeaturePython)
  n = 0.545621
FEATURE [App::DocumentObjectGroupPython] Cl_element013  label="Cl_element : 0.339"  # scripted group (container) (typed FeaturePython)
  n = 0.339396
FEATURE [App::DocumentObjectGroupPython] G4_FREON_13  label="G4_FREON-13"  # scripted group (container) (typed FeaturePython)
  Dunit = g/cm3
  Dvalue = 0.95
  Group = -> [C_element045,F_element009,Cl_element013]
  conduct = 2
  density = 1
  expand = 3
  formula = G4_FREON-13
  name = G4_FREON-13
  specific = 4
FEATURE [App::DocumentObjectGroupPython] C_element046  label="C_element : 025"  # scripted group (container) (typed FeaturePython)
  n = 1
  ref = C_element
FEATURE [App::DocumentObjectGroupPython] F_element010  label="F_element : 3"  # scripted group (container) (typed FeaturePython)
  n = 3
  ref = F_element
FEATURE [App::DocumentObjectGroupPython] Br_element002  label="Br_element : 1"  # scripted group (container) (typed FeaturePython)
  n = 1
  ref = Br_element
FEATURE [App::DocumentObjectGroupPython] G4_FREON_13B1  label="G4_FREON-13B1"  # scripted group (container) (typed FeaturePython)
  Dunit = g/cm3
  Dvalue = 1.5
  Group = -> [C_element046,F_element010,Br_element002]
  conduct = 2
  density = 1
  expand = 3
  formula = G4_FREON-13B1
  name = G4_FREON-13B1
  specific = 4
FEATURE [App::DocumentObjectGroupPython] C_element047  label="C_element : 0.061"  # scripted group (container) (typed FeaturePython)
  n = 0.061309
FEATURE [App::DocumentObjectGroupPython] F_element011  label="F_element : 0.291"  # scripted group (container) (typed FeaturePython)
  n = 0.290924
FEATURE [App::DocumentObjectGroupPython] I_element002  label="I_element : 0.648"  # scripted group (container) (typed FeaturePython)
  n = 0.647767
FEATURE [App::DocumentObjectGroupPython] G4_FREON_13I1  label="G4_FREON-13I1"  # scripted group (container) (typed FeaturePython)
  Dunit = g/cm3
  Dvalue = 1.8
  Group = -> [C_element047,F_element011,I_element002]
  conduct = 2
  density = 1
  expand = 3
  formula = G4_FREON-13I1
  name = G4_FREON-13I1
  specific = 4
FEATURE [App::DocumentObjectGroupPython] Gd_element001  label="Gd_element : 2"  # scripted group (container) (typed FeaturePython)
  n = 2
  ref = Gd_element
FEATURE [App::DocumentObjectGroupPython] O_element041  label="O_element : 021"  # scripted group (container) (typed FeaturePython)
  n = 2
  ref = O_element
FEATURE [App::DocumentObjectGroupPython] S_element012  label="S_element : 004"  # scripted group (container) (typed FeaturePython)
  n = 1
  ref = S_element
FEATURE [App::DocumentObjectGroupPython] G4_GADOLINIUM_OXYSULFIDE  # scripted group (container) (typed FeaturePython)
  Dunit = g/cm3
  Dvalue = 7.44
  Group = -> [Gd_element001,O_element041,S_element012]
  conduct = 2
  density = 1
  expand = 3
  formula = G4_GADOLINIUM_OXYSULFIDE
  name = G4_GADOLINIUM_OXYSULFIDE
  specific = 4
FEATURE [App::DocumentObjectGroupPython] Ga_element001  label="Ga_element : 1"  # scripted group (container) (typed FeaturePython)
  n = 1
  ref = Ga_element
FEATURE [App::DocumentObjectGroupPython] As_element001  label="As_element : 1"  # scripted group (container) (typed FeaturePython)
  n = 1
  ref = As_element
FEATURE [App::DocumentObjectGroupPython] G4_GALLIUM_ARSENIDE  # scripted group (container) (typed FeaturePython)
  Dunit = g/cm3
  Dvalue = 5.31
  Group = -> [Ga_element001,As_element001]
  conduct = 2
  density = 1
  expand = 3
  formula = G4_GALLIUM_ARSENIDE
  name = G4_GALLIUM_ARSENIDE
  specific = 4
FEATURE [App::DocumentObjectGroupPython] H_element041  label="H_element : 0.081"  # scripted group (container) (typed FeaturePython)
  n = 0.08118
FEATURE [App::DocumentObjectGroupPython] C_element048  label="C_element : 0.416"  # scripted group (container) (typed FeaturePython)
  n = 0.41606
FEATURE [App::DocumentObjectGroupPython] N_element018  label="N_element : 0.111"  # scripted group (container) (typed FeaturePython)
  n = 0.11124
FEATURE [App::DocumentObjectGroupPython] O_element042  label="O_element : 0.381"  # scripted group (container) (typed FeaturePython)
  n = 0.38064
FEATURE [App::DocumentObjectGroupPython] S_element013  label="S_element : 0.011"  # scripted group (container) (typed FeaturePython)
  n = 0.01088
FEATURE [App::DocumentObjectGroupPython] G4_GEL_PHOTO_EMULSION  # scripted group (container) (typed FeaturePython)
  Dunit = g/cm3
  Dvalue = 1.2914
  Group = -> [H_element041,C_element048,N_element018,O_element042,S_element013]
  conduct = 2
  density = 1
  expand = 3
  formula = G4_GEL_PHOTO_EMULSION
  name = G4_GEL_PHOTO_EMULSION
  specific = 4
FEATURE [App::DocumentObjectGroupPython] B_element004  label="B_element : 0.040"  # scripted group (container) (typed FeaturePython)
  n = 0.0400639
FEATURE [App::DocumentObjectGroupPython] O_element043  label="O_element : 0.540"  # scripted group (container) (typed FeaturePython)
  n = 0.539561
FEATURE [App::DocumentObjectGroupPython] Na_element008  label="Na_element : 0.028"  # scripted group (container) (typed FeaturePython)
  n = 0.0281909
FEATURE [App::DocumentObjectGroupPython] Al_element003  label="Al_element : 0.012"  # scripted group (container) (typed FeaturePython)
  n = 0.011644
FEATURE [App::DocumentObjectGroupPython] Si_element003  label="Si_element : 0.377"  # scripted group (container) (typed FeaturePython)
  n = 0.377219
FEATURE [App::DocumentObjectGroupPython] K_element004  label="K_element : 0.014"  # scripted group (container) (typed FeaturePython)
  n = 0.00332099
FEATURE [App::DocumentObjectGroupPython] G4_Pyrex_Glass  # scripted group (container) (typed FeaturePython)
  Dunit = g/cm3
  Dvalue = 2.23
  Group = -> [B_element004,O_element043,Na_element008,Al_element003,Si_element003,K_element004]
  conduct = 2
  density = 1
  expand = 3
  formula = G4_Pyrex_Glass
  name = G4_Pyrex_Glass
  specific = 4
FEATURE [App::DocumentObjectGroupPython] O_element044  label="O_element : 0.156"  # scripted group (container) (typed FeaturePython)
  n = 0.156453
FEATURE [App::DocumentObjectGroupPython] Si_element004  label="Si_element : 0.081"  # scripted group (container) (typed FeaturePython)
  n = 0.080866
FEATURE [App::DocumentObjectGroupPython] Ti_element001  label="Ti_element : 0.008"  # scripted group (container) (typed FeaturePython)
  n = 0.008092
FEATURE [App::DocumentObjectGroupPython] As_element002  label="As_element : 0.003"  # scripted group (container) (typed FeaturePython)
  n = 0.002651
FEATURE [App::DocumentObjectGroupPython] Pb_element001  label="Pb_element : 0.752"  # scripted group (container) (typed FeaturePython)
  n = 0.751938
FEATURE [App::DocumentObjectGroupPython] G4_GLASS_LEAD  # scripted group (container) (typed FeaturePython)
  Dunit = g/cm3
  Dvalue = 6.22
  Group = -> [O_element044,Si_element004,Ti_element001,As_element002,Pb_element001]
  conduct = 2
  density = 1
  expand = 3
  formula = G4_GLASS_LEAD
  name = G4_GLASS_LEAD
  specific = 4
FEATURE [App::DocumentObjectGroupPython] O_element045  label="O_element : 0.460"  # scripted group (container) (typed FeaturePython)
  n = 0.4598
FEATURE [App::DocumentObjectGroupPython] Na_element009  label="Na_element : 0.096"  # scripted group (container) (typed FeaturePython)
  n = 0.0964411
FEATURE [App::DocumentObjectGroupPython] Si_element005  label="Si_element : 0.378"  # scripted group (container) (typed FeaturePython)
  n = 0.336553
FEATURE [App::DocumentObjectGroupPython] Ca_element011  label="Ca_element : 0.107"  # scripted group (container) (typed FeaturePython)
  n = 0.107205
FEATURE [App::DocumentObjectGroupPython] G4_GLASS_PLATE  # scripted group (container) (typed FeaturePython)
  Dunit = g/cm3
  Dvalue = 2.4
  Group = -> [O_element045,Na_element009,Si_element005,Ca_element011]
  conduct = 2
  density = 1
  expand = 3
  formula = G4_GLASS_PLATE
  name = G4_GLASS_PLATE
  specific = 4
FEATURE [App::DocumentObjectGroupPython] C_element049  label="C_element : 026"  # scripted group (container) (typed FeaturePython)
  n = 5
  ref = C_element
FEATURE [App::DocumentObjectGroupPython] H_element042  label="H_element : 021"  # scripted group (container) (typed FeaturePython)
  n = 10
  ref = H_element
FEATURE [App::DocumentObjectGroupPython] N_element019  label="N_element : 2"  # scripted group (container) (typed FeaturePython)
  n = 2
  ref = N_element
FEATURE [App::DocumentObjectGroupPython] O_element046  label="O_element : 022"  # scripted group (container) (typed FeaturePython)
  n = 3
  ref = O_element
FEATURE [App::DocumentObjectGroupPython] G4_GLUTAMINE  # scripted group (container) (typed FeaturePython)
  Dunit = g/cm3
  Dvalue = 1.46
  Group = -> [C_element049,H_element042,N_element019,O_element046]
  conduct = 2
  density = 1
  expand = 3
  formula = G4_GLUTAMINE
  name = G4_GLUTAMINE
  specific = 4
FEATURE [App::DocumentObjectGroupPython] C_element050  label="C_element : 027"  # scripted group (container) (typed FeaturePython)
  n = 3
  ref = C_element
FEATURE [App::DocumentObjectGroupPython] H_element043  label="H_element : 022"  # scripted group (container) (typed FeaturePython)
  n = 8
  ref = H_element
FEATURE [App::DocumentObjectGroupPython] O_element047  label="O_element : 023"  # scripted group (container) (typed FeaturePython)
  n = 3
  ref = O_element
FEATURE [App::DocumentObjectGroupPython] G4_GLYCEROL  # scripted group (container) (typed FeaturePython)
  Dunit = g/cm3
  Dvalue = 1.2613
  Group = -> [C_element050,H_element043,O_element047]
  conduct = 2
  density = 1
  expand = 3
  formula = G4_GLYCEROL
  name = G4_GLYCEROL
  specific = 4
FEATURE [App::DocumentObjectGroupPython] C_element051  label="C_element : 028"  # scripted group (container) (typed FeaturePython)
  n = 5
  ref = C_element
FEATURE [App::DocumentObjectGroupPython] H_element044  label="H_element : 023"  # scripted group (container) (typed FeaturePython)
  n = 5
  ref = H_element
FEATURE [App::DocumentObjectGroupPython] N_element020  label="N_element : 009"  # scripted group (container) (typed FeaturePython)
  n = 5
  ref = N_element
FEATURE [App::DocumentObjectGroupPython] O_element048  label="O_element : 024"  # scripted group (container) (typed FeaturePython)
  n = 1
  ref = O_element
FEATURE [App::DocumentObjectGroupPython] G4_GUANINE  # scripted group (container) (typed FeaturePython)
  Dunit = g/cm3
  Dvalue = 2.2
  Group = -> [C_element051,H_element044,N_element020,O_element048]
  conduct = 2
  density = 1
  expand = 3
  formula = G4_GUANINE
  name = G4_GUANINE
  specific = 4
FEATURE [App::DocumentObjectGroupPython] Ca_element012  label="Ca_element : 006"  # scripted group (container) (typed FeaturePython)
  n = 1
  ref = Ca_element
FEATURE [App::DocumentObjectGroupPython] S_element014  label="S_element : 005"  # scripted group (container) (typed FeaturePython)
  n = 1
  ref = S_element
FEATURE [App::DocumentObjectGroupPython] O_element049  label="O_element : 6"  # scripted group (container) (typed FeaturePython)
  n = 6
  ref = O_element
FEATURE [App::DocumentObjectGroupPython] H_element045  label="H_element : 024"  # scripted group (container) (typed FeaturePython)
  n = 4
  ref = H_element
FEATURE [App::DocumentObjectGroupPython] G4_GYPSUM  # scripted group (container) (typed FeaturePython)
  Dunit = g/cm3
  Dvalue = 2.32
  Group = -> [Ca_element012,S_element014,O_element049,H_element045]
  conduct = 2
  density = 1
  expand = 3
  formula = G4_GYPSUM
  name = G4_GYPSUM
  specific = 4
FEATURE [App::DocumentObjectGroupPython] C_element052  label="C_element : 7"  # scripted group (container) (typed FeaturePython)
  n = 7
  ref = C_element
FEATURE [App::DocumentObjectGroupPython] H_element046  label="H_element : 16"  # scripted group (container) (typed FeaturePython)
  n = 16
  ref = H_element
FEATURE [App::DocumentObjectGroupPython] G4_N_HEPTANE  label="G4_N-HEPTANE"  # scripted group (container) (typed FeaturePython)
  Dunit = g/cm3
  Dvalue = 0.68376
  Group = -> [C_element052,H_element046]
  conduct = 2
  density = 1
  expand = 3
  formula = G4_N-HEPTANE
  name = G4_N-HEPTANE
  specific = 4
FEATURE [App::DocumentObjectGroupPython] C_element053  label="C_element : 029"  # scripted group (container) (typed FeaturePython)
  n = 6
  ref = C_element
FEATURE [App::DocumentObjectGroupPython] H_element047  label="H_element : 14"  # scripted group (container) (typed FeaturePython)
  n = 14
  ref = H_element
FEATURE [App::DocumentObjectGroupPython] G4_N_HEXANE  label="G4_N-HEXANE"  # scripted group (container) (typed FeaturePython)
  Dunit = g/cm3
  Dvalue = 0.6603
  Group = -> [C_element053,H_element047]
  conduct = 2
  density = 1
  expand = 3
  formula = G4_N-HEXANE
  name = G4_N-HEXANE
  specific = 4
FEATURE [App::DocumentObjectGroupPython] C_element054  label="C_element : 22"  # scripted group (container) (typed FeaturePython)
  n = 22
  ref = C_element
FEATURE [App::DocumentObjectGroupPython] H_element048  label="H_element : 025"  # scripted group (container) (typed FeaturePython)
  n = 10
  ref = H_element
FEATURE [App::DocumentObjectGroupPython] N_element021  label="N_element : 010"  # scripted group (container) (typed FeaturePython)
  n = 2
  ref = N_element
FEATURE [App::DocumentObjectGroupPython] O_element050  label="O_element : 025"  # scripted group (container) (typed FeaturePython)
  n = 5
  ref = O_element
FEATURE [App::DocumentObjectGroupPython] G4_KAPTON  # scripted group (container) (typed FeaturePython)
  Dunit = g/cm3
  Dvalue = 1.42
  Group = -> [C_element054,H_element048,N_element021,O_element050]
  conduct = 2
  density = 1
  expand = 3
  formula = G4_KAPTON
  name = G4_KAPTON
  specific = 4
FEATURE [App::DocumentObjectGroupPython] La_element001  label="La_element : 1"  # scripted group (container) (typed FeaturePython)
  n = 1
  ref = La_element
FEATURE [App::DocumentObjectGroupPython] Br_element003  label="Br_element : 002"  # scripted group (container) (typed FeaturePython)
  n = 1
  ref = Br_element
FEATURE [App::DocumentObjectGroupPython] O_element051  label="O_element : 026"  # scripted group (container) (typed FeaturePython)
  n = 1
  ref = O_element
FEATURE [App::DocumentObjectGroupPython] G4_LANTHANUM_OXYBROMIDE  # scripted group (container) (typed FeaturePython)
  Dunit = g/cm3
  Dvalue = 6.28
  Group = -> [La_element001,Br_element003,O_element051]
  conduct = 2
  density = 1
  expand = 3
  formula = G4_LANTHANUM_OXYBROMIDE
  name = G4_LANTHANUM_OXYBROMIDE
  specific = 4
FEATURE [App::DocumentObjectGroupPython] La_element002  label="La_element : 2"  # scripted group (container) (typed FeaturePython)
  n = 2
  ref = La_element
FEATURE [App::DocumentObjectGroupPython] O_element052  label="O_element : 027"  # scripted group (container) (typed FeaturePython)
  n = 2
  ref = O_element
FEATURE [App::DocumentObjectGroupPython] S_element015  label="S_element : 006"  # scripted group (container) (typed FeaturePython)
  n = 1
  ref = S_element
FEATURE [App::DocumentObjectGroupPython] G4_LANTHANUM_OXYSULFIDE  # scripted group (container) (typed FeaturePython)
  Dunit = g/cm3
  Dvalue = 5.86
  Group = -> [La_element002,O_element052,S_element015]
  conduct = 2
  density = 1
  expand = 3
  formula = G4_LANTHANUM_OXYSULFIDE
  name = G4_LANTHANUM_OXYSULFIDE
  specific = 4
FEATURE [App::DocumentObjectGroupPython] O_element053  label="O_element : 0.072"  # scripted group (container) (typed FeaturePython)
  n = 0.071682
FEATURE [App::DocumentObjectGroupPython] Pb_element002  label="Pb_element : 0.928"  # scripted group (container) (typed FeaturePython)
  n = 0.928318
FEATURE [App::DocumentObjectGroupPython] G4_LEAD_OXIDE  # scripted group (container) (typed FeaturePython)
  Dunit = g/cm3
  Dvalue = 9.53
  Group = -> [O_element053,Pb_element002]
  conduct = 2
  density = 1
  expand = 3
  formula = G4_LEAD_OXIDE
  name = G4_LEAD_OXIDE
  specific = 4
FEATURE [App::DocumentObjectGroupPython] Li_element001  label="Li_element : 1"  # scripted group (container) (typed FeaturePython)
  n = 1
  ref = Li_element
FEATURE [App::DocumentObjectGroupPython] N_element022  label="N_element : 011"  # scripted group (container) (typed FeaturePython)
  n = 1
  ref = N_element
FEATURE [App::DocumentObjectGroupPython] H_element049  label="H_element : 026"  # scripted group (container) (typed FeaturePython)
  n = 2
  ref = H_element
FEATURE [App::DocumentObjectGroupPython] G4_LITHIUM_AMIDE  # scripted group (container) (typed FeaturePython)
  Dunit = g/cm3
  Dvalue = 1.178
  Group = -> [Li_element001,N_element022,H_element049]
  conduct = 2
  density = 1
  expand = 3
  formula = G4_LITHIUM_AMIDE
  name = G4_LITHIUM_AMIDE
  specific = 4
FEATURE [App::DocumentObjectGroupPython] Li_element002  label="Li_element : 2"  # scripted group (container) (typed FeaturePython)
  n = 2
  ref = Li_element
FEATURE [App::DocumentObjectGroupPython] C_element055  label="C_element : 030"  # scripted group (container) (typed FeaturePython)
  n = 1
  ref = C_element
FEATURE [App::DocumentObjectGroupPython] O_element054  label="O_element : 028"  # scripted group (container) (typed FeaturePython)
  n = 3
  ref = O_element
FEATURE [App::DocumentObjectGroupPython] G4_LITHIUM_CARBONATE  # scripted group (container) (typed FeaturePython)
  Dunit = g/cm3
  Dvalue = 2.11
  Group = -> [Li_element002,C_element055,O_element054]
  conduct = 2
  density = 1
  expand = 3
  formula = G4_LITHIUM_CARBONATE
  name = G4_LITHIUM_CARBONATE
  specific = 4
FEATURE [App::DocumentObjectGroupPython] Li_element003  label="Li_element : 003"  # scripted group (container) (typed FeaturePython)
  n = 1
  ref = Li_element
FEATURE [App::DocumentObjectGroupPython] F_element012  label="F_element : 004"  # scripted group (container) (typed FeaturePython)
  n = 1
  ref = F_element
FEATURE [App::DocumentObjectGroupPython] G4_LITHIUM_FLUORIDE  # scripted group (container) (typed FeaturePython)
  Dunit = g/cm3
  Dvalue = 2.635
  Group = -> [Li_element003,F_element012]
  conduct = 2
  density = 1
  expand = 3
  formula = G4_LITHIUM_FLUORIDE
  name = G4_LITHIUM_FLUORIDE
  specific = 4
FEATURE [App::DocumentObjectGroupPython] Li_element004  label="Li_element : 004"  # scripted group (container) (typed FeaturePython)
  n = 1
  ref = Li_element
FEATURE [App::DocumentObjectGroupPython] H_element050  label="H_element : 027"  # scripted group (container) (typed FeaturePython)
  n = 1
  ref = H_element
FEATURE [App::DocumentObjectGroupPython] G4_LITHIUM_HYDRIDE  # scripted group (container) (typed FeaturePython)
  Dunit = g/cm3
  Dvalue = 0.82
  Group = -> [Li_element004,H_element050]
  conduct = 2
  density = 1
  expand = 3
  formula = G4_LITHIUM_HYDRIDE
  name = G4_LITHIUM_HYDRIDE
  specific = 4
FEATURE [App::DocumentObjectGroupPython] Li_element005  label="Li_element : 005"  # scripted group (container) (typed FeaturePython)
  n = 1
  ref = Li_element
FEATURE [App::DocumentObjectGroupPython] I_element003  label="I_element : 002"  # scripted group (container) (typed FeaturePython)
  n = 1
  ref = I_element
FEATURE [App::DocumentObjectGroupPython] G4_LITHIUM_IODIDE  # scripted group (container) (typed FeaturePython)
  Dunit = g/cm3
  Dvalue = 3.494
  Group = -> [Li_element005,I_element003]
  conduct = 2
  density = 1
  expand = 3
  formula = G4_LITHIUM_IODIDE
  name = G4_LITHIUM_IODIDE
  specific = 4
FEATURE [App::DocumentObjectGroupPython] Li_element006  label="Li_element : 006"  # scripted group (container) (typed FeaturePython)
  n = 2
  ref = Li_element
FEATURE [App::DocumentObjectGroupPython] O_element055  label="O_element : 029"  # scripted group (container) (typed FeaturePython)
  n = 1
  ref = O_element
FEATURE [App::DocumentObjectGroupPython] G4_LITHIUM_OXIDE  # scripted group (container) (typed FeaturePython)
  Dunit = g/cm3
  Dvalue = 2.013
  Group = -> [Li_element006,O_element055]
  conduct = 2
  density = 1
  expand = 3
  formula = G4_LITHIUM_OXIDE
  name = G4_LITHIUM_OXIDE
  specific = 4
FEATURE [App::DocumentObjectGroupPython] Li_element007  label="Li_element : 007"  # scripted group (container) (typed FeaturePython)
  n = 2
  ref = Li_element
FEATURE [App::DocumentObjectGroupPython] B_element005  label="B_element : 005"  # scripted group (container) (typed FeaturePython)
  n = 4
  ref = B_element
FEATURE [App::DocumentObjectGroupPython] O_element056  label="O_element : 7"  # scripted group (container) (typed FeaturePython)
  n = 7
  ref = O_element
FEATURE [App::DocumentObjectGroupPython] G4_LITHIUM_TETRABORATE  # scripted group (container) (typed FeaturePython)
  Dunit = g/cm3
  Dvalue = 2.44
  Group = -> [Li_element007,B_element005,O_element056]
  conduct = 2
  density = 1
  expand = 3
  formula = G4_LITHIUM_TETRABORATE
  name = G4_LITHIUM_TETRABORATE
  specific = 4
FEATURE [App::DocumentObjectGroupPython] H_element051  label="H_element : 0.105"  # scripted group (container) (typed FeaturePython)
  n = 0.105
FEATURE [App::DocumentObjectGroupPython] C_element056  label="C_element : 0.083"  # scripted group (container) (typed FeaturePython)
  n = 0.083
FEATURE [App::DocumentObjectGroupPython] N_element023  label="N_element : 0.023"  # scripted group (container) (typed FeaturePython)
  n = 0.023
FEATURE [App::DocumentObjectGroupPython] O_element057  label="O_element : 0.779"  # scripted group (container) (typed FeaturePython)
  n = 0.779
FEATURE [App::DocumentObjectGroupPython] Na_element010  label="Na_element : 0.097"  # scripted group (container) (typed FeaturePython)
  n = 0.002
FEATURE [App::DocumentObjectGroupPython] P_element006  label="P_element : 0.105"  # scripted group (container) (typed FeaturePython)
  n = 0.001
FEATURE [App::DocumentObjectGroupPython] S_element016  label="S_element : 0.017"  # scripted group (container) (typed FeaturePython)
  n = 0.002
FEATURE [App::DocumentObjectGroupPython] Cl_element014  label="Cl_element : 0.587"  # scripted group (container) (typed FeaturePython)
  n = 0.003
FEATURE [App::DocumentObjectGroupPython] K_element005  label="K_element : 0.015"  # scripted group (container) (typed FeaturePython)
  n = 0.002
FEATURE [App::DocumentObjectGroupPython] G4_LUNG_ICRP  # scripted group (container) (typed FeaturePython)
  Dunit = g/cm3
  Dvalue = 1.04
  Group = -> [H_element051,C_element056,N_element023,O_element057,Na_element010,P_element006,S_element016,Cl_element014,K_element005]
  conduct = 2
  density = 1
  expand = 3
  formula = G4_LUNG_ICRP
  name = G4_LUNG_ICRP
  specific = 4
FEATURE [App::DocumentObjectGroupPython] H_element052  label="H_element : 0.116"  # scripted group (container) (typed FeaturePython)
  n = 0.114318
FEATURE [App::DocumentObjectGroupPython] C_element057  label="C_element : 0.656"  # scripted group (container) (typed FeaturePython)
  n = 0.655824
FEATURE [App::DocumentObjectGroupPython] O_element058  label="O_element : 0.092"  # scripted group (container) (typed FeaturePython)
  n = 0.0921831
FEATURE [App::DocumentObjectGroupPython] Mg_element004  label="Mg_element : 0.135"  # scripted group (container) (typed FeaturePython)
  n = 0.134792
FEATURE [App::DocumentObjectGroupPython] Ca_element013  label="Ca_element : 0.003"  # scripted group (container) (typed FeaturePython)
  n = 0.002883
FEATURE [App::DocumentObjectGroupPython] G4_M3_WAX  # scripted group (container) (typed FeaturePython)
  Dunit = g/cm3
  Dvalue = 1.05
  Group = -> [H_element052,C_element057,O_element058,Mg_element004,Ca_element013]
  conduct = 2
  density = 1
  expand = 3
  formula = G4_M3_WAX
  name = G4_M3_WAX
  specific = 4
FEATURE [App::DocumentObjectGroupPython] Mg_element005  label="Mg_element : 1"  # scripted group (container) (typed FeaturePython)
  n = 1
  ref = Mg_element
FEATURE [App::DocumentObjectGroupPython] C_element058  label="C_element : 031"  # scripted group (container) (typed FeaturePython)
  n = 1
  ref = C_element
FEATURE [App::DocumentObjectGroupPython] O_element059  label="O_element : 030"  # scripted group (container) (typed FeaturePython)
  n = 3
  ref = O_element
FEATURE [App::DocumentObjectGroupPython] G4_MAGNESIUM_CARBONATE  # scripted group (container) (typed FeaturePython)
  Dunit = g/cm3
  Dvalue = 2.958
  Group = -> [Mg_element005,C_element058,O_element059]
  conduct = 2
  density = 1
  expand = 3
  formula = G4_MAGNESIUM_CARBONATE
  name = G4_MAGNESIUM_CARBONATE
  specific = 4
FEATURE [App::DocumentObjectGroupPython] Mg_element006  label="Mg_element : 002"  # scripted group (container) (typed FeaturePython)
  n = 1
  ref = Mg_element
FEATURE [App::DocumentObjectGroupPython] F_element013  label="F_element : 005"  # scripted group (container) (typed FeaturePython)
  n = 2
  ref = F_element
FEATURE [App::DocumentObjectGroupPython] G4_MAGNESIUM_FLUORIDE  # scripted group (container) (typed FeaturePython)
  Dunit = g/cm3
  Dvalue = 3
  Group = -> [Mg_element006,F_element013]
  conduct = 2
  density = 1
  expand = 3
  formula = G4_MAGNESIUM_FLUORIDE
  name = G4_MAGNESIUM_FLUORIDE
  specific = 4
FEATURE [App::DocumentObjectGroupPython] Mg_element007  label="Mg_element : 003"  # scripted group (container) (typed FeaturePython)
  n = 1
  ref = Mg_element
FEATURE [App::DocumentObjectGroupPython] O_element060  label="O_element : 031"  # scripted group (container) (typed FeaturePython)
  n = 1
  ref = O_element
FEATURE [App::DocumentObjectGroupPython] G4_MAGNESIUM_OXIDE  # scripted group (container) (typed FeaturePython)
  Dunit = g/cm3
  Dvalue = 3.58
  Group = -> [Mg_element007,O_element060]
  conduct = 2
  density = 1
  expand = 3
  formula = G4_MAGNESIUM_OXIDE
  name = G4_MAGNESIUM_OXIDE
  specific = 4
FEATURE [App::DocumentObjectGroupPython] Mg_element008  label="Mg_element : 004"  # scripted group (container) (typed FeaturePython)
  n = 1
  ref = Mg_element
FEATURE [App::DocumentObjectGroupPython] B_element006  label="B_element : 006"  # scripted group (container) (typed FeaturePython)
  n = 4
  ref = B_element
FEATURE [App::DocumentObjectGroupPython] O_element061  label="O_element : 032"  # scripted group (container) (typed FeaturePython)
  n = 7
  ref = O_element
FEATURE [App::DocumentObjectGroupPython] G4_MAGNESIUM_TETRABORATE  # scripted group (container) (typed FeaturePython)
  Dunit = g/cm3
  Dvalue = 2.53
  Group = -> [Mg_element008,B_element006,O_element061]
  conduct = 2
  density = 1
  expand = 3
  formula = G4_MAGNESIUM_TETRABORATE
  name = G4_MAGNESIUM_TETRABORATE
  specific = 4
FEATURE [App::DocumentObjectGroupPython] Hg_element001  label="Hg_element : 1"  # scripted group (container) (typed FeaturePython)
  n = 1
  ref = Hg_element
FEATURE [App::DocumentObjectGroupPython] I_element004  label="I_element : 2"  # scripted group (container) (typed FeaturePython)
  n = 2
  ref = I_element
FEATURE [App::DocumentObjectGroupPython] G4_MERCURIC_IODIDE  # scripted group (container) (typed FeaturePython)
  Dunit = g/cm3
  Dvalue = 6.36
  Group = -> [Hg_element001,I_element004]
  conduct = 2
  density = 1
  expand = 3
  formula = G4_MERCURIC_IODIDE
  name = G4_MERCURIC_IODIDE
  specific = 4
FEATURE [App::DocumentObjectGroupPython] C_element059  label="C_element : 032"  # scripted group (container) (typed FeaturePython)
  n = 1
  ref = C_element
FEATURE [App::DocumentObjectGroupPython] H_element053  label="H_element : 028"  # scripted group (container) (typed FeaturePython)
  n = 4
  ref = H_element
FEATURE [App::DocumentObjectGroupPython] G4_METHANE  # scripted group (container) (typed FeaturePython)
  Dunit = g/cm3
  Dvalue = 0.000667151
  Group = -> [C_element059,H_element053]
  conduct = 2
  density = 1
  expand = 3
  formula = G4_METHANE
  name = G4_METHANE
  specific = 4
FEATURE [App::DocumentObjectGroupPython] C_element060  label="C_element : 033"  # scripted group (container) (typed FeaturePython)
  n = 1
  ref = C_element
FEATURE [App::DocumentObjectGroupPython] H_element054  label="H_element : 029"  # scripted group (container) (typed FeaturePython)
  n = 4
  ref = H_element
FEATURE [App::DocumentObjectGroupPython] O_element062  label="O_element : 033"  # scripted group (container) (typed FeaturePython)
  n = 1
  ref = O_element
FEATURE [App::DocumentObjectGroupPython] G4_METHANOL  # scripted group (container) (typed FeaturePython)
  Dunit = g/cm3
  Dvalue = 0.7914
  Group = -> [C_element060,H_element054,O_element062]
  conduct = 2
  density = 1
  expand = 3
  formula = G4_METHANOL
  name = G4_METHANOL
  specific = 4
FEATURE [App::DocumentObjectGroupPython] H_element055  label="H_element : 0.134"  # scripted group (container) (typed FeaturePython)
  n = 0.13404
FEATURE [App::DocumentObjectGroupPython] C_element061  label="C_element : 0.778"  # scripted group (container) (typed FeaturePython)
  n = 0.77796
FEATURE [App::DocumentObjectGroupPython] O_element063  label="O_element : 0.035"  # scripted group (container) (typed FeaturePython)
  n = 0.03502
FEATURE [App::DocumentObjectGroupPython] Mg_element009  label="Mg_element : 0.039"  # scripted group (container) (typed FeaturePython)
  n = 0.038594
FEATURE [App::DocumentObjectGroupPython] Ti_element002  label="Ti_element : 0.014"  # scripted group (container) (typed FeaturePython)
  n = 0.014386
FEATURE [App::DocumentObjectGroupPython] G4_MIX_D_WAX  # scripted group (container) (typed FeaturePython)
  Dunit = g/cm3
  Dvalue = 0.99
  Group = -> [H_element055,C_element061,O_element063,Mg_element009,Ti_element002]
  conduct = 2
  density = 1
  expand = 3
  formula = G4_MIX_D_WAX
  name = G4_MIX_D_WAX
  specific = 4
FEATURE [App::DocumentObjectGroupPython] H_element056  label="H_element : 0.135"  # scripted group (container) (typed FeaturePython)
  n = 0.081192
FEATURE [App::DocumentObjectGroupPython] C_element062  label="C_element : 0.583"  # scripted group (container) (typed FeaturePython)
  n = 0.583442
FEATURE [App::DocumentObjectGroupPython] N_element024  label="N_element : 0.018"  # scripted group (container) (typed FeaturePython)
  n = 0.017798
FEATURE [App::DocumentObjectGroupPython] O_element064  label="O_element : 0.186"  # scripted group (container) (typed FeaturePython)
  n = 0.186381
FEATURE [App::DocumentObjectGroupPython] Mg_element010  label="Mg_element : 0.130"  # scripted group (container) (typed FeaturePython)
  n = 0.130287
FEATURE [App::DocumentObjectGroupPython] Cl_element015  label="Cl_element : 0.588"  # scripted group (container) (typed FeaturePython)
  n = 0.0009
FEATURE [App::DocumentObjectGroupPython] G4_MS20_TISSUE  # scripted group (container) (typed FeaturePython)
  Dunit = g/cm3
  Dvalue = 1
  Group = -> [H_element056,C_element062,N_element024,O_element064,Mg_element010,Cl_element015]
  conduct = 2
  density = 1
  expand = 3
  formula = G4_MS20_TISSUE
  name = G4_MS20_TISSUE
  specific = 4
FEATURE [App::DocumentObjectGroupPython] H_element057  label="H_element : 0.136"  # scripted group (container) (typed FeaturePython)
  n = 0.102
FEATURE [App::DocumentObjectGroupPython] C_element063  label="C_element : 0.143"  # scripted group (container) (typed FeaturePython)
  n = 0.143
FEATURE [App::DocumentObjectGroupPython] N_element025  label="N_element : 0.034"  # scripted group (container) (typed FeaturePython)
  n = 0.034
FEATURE [App::DocumentObjectGroupPython] O_element065  label="O_element : 0.710"  # scripted group (container) (typed FeaturePython)
  n = 0.71
FEATURE [App::DocumentObjectGroupPython] Na_element011  label="Na_element : 0.098"  # scripted group (container) (typed FeaturePython)
  n = 0.001
FEATURE [App::DocumentObjectGroupPython] P_element007  label="P_element : 0.002"  # scripted group (container) (typed FeaturePython)
  n = 0.002
FEATURE [App::DocumentObjectGroupPython] S_element017  label="S_element : 0.018"  # scripted group (container) (typed FeaturePython)
  n = 0.003
FEATURE [App::DocumentObjectGroupPython] Cl_element016  label="Cl_element : 0.589"  # scripted group (container) (typed FeaturePython)
  n = 0.001
FEATURE [App::DocumentObjectGroupPython] K_element006  label="K_element : 0.004"  # scripted group (container) (typed FeaturePython)
  n = 0.004
FEATURE [App::DocumentObjectGroupPython] G4_MUSCLE_SKELETAL_ICRP  # scripted group (container) (typed FeaturePython)
  Dunit = g/cm3
  Dvalue = 1.05
  Group = -> [H_element057,C_element063,N_element025,O_element065,Na_element011,P_element007,S_element017,Cl_element016,K_element006]
  conduct = 2
  density = 1
  expand = 3
  formula = G4_MUSCLE_SKELETAL_ICRP
  name = G4_MUSCLE_SKELETAL_ICRP
  specific = 4
FEATURE [App::DocumentObjectGroupPython] H_element058  label="H_element : 0.137"  # scripted group (container) (typed FeaturePython)
  n = 0.102102
FEATURE [App::DocumentObjectGroupPython] C_element064  label="C_element : 0.123"  # scripted group (container) (typed FeaturePython)
  n = 0.123123
FEATURE [App::DocumentObjectGroupPython] N_element026  label="N_element : 0.756"  # scripted group (container) (typed FeaturePython)
  n = 0.035035
FEATURE [App::DocumentObjectGroupPython] O_element066  label="O_element : 0.730"  # scripted group (container) (typed FeaturePython)
  n = 0.72973
FEATURE [App::DocumentObjectGroupPython] Na_element012  label="Na_element : 0.099"  # scripted group (container) (typed FeaturePython)
  n = 0.001001
FEATURE [App::DocumentObjectGroupPython] P_element008  label="P_element : 0.106"  # scripted group (container) (typed FeaturePython)
  n = 0.002002
FEATURE [App::DocumentObjectGroupPython] S_element018  label="S_element : 0.019"  # scripted group (container) (typed FeaturePython)
  n = 0.004004
FEATURE [App::DocumentObjectGroupPython] K_element007  label="K_element : 0.016"  # scripted group (container) (typed FeaturePython)
  n = 0.003003
FEATURE [App::DocumentObjectGroupPython] G4_MUSCLE_STRIATED_ICRU  # scripted group (container) (typed FeaturePython)
  Dunit = g/cm3
  Dvalue = 1.04
  Group = -> [H_element058,C_element064,N_element026,O_element066,Na_element012,P_element008,S_element018,K_element007]
  conduct = 2
  density = 1
  expand = 3
  formula = G4_MUSCLE_STRIATED_ICRU
  name = G4_MUSCLE_STRIATED_ICRU
  specific = 4
FEATURE [App::DocumentObjectGroupPython] H_element059  label="H_element : 0.098"  # scripted group (container) (typed FeaturePython)
  n = 0.0982341
FEATURE [App::DocumentObjectGroupPython] C_element065  label="C_element : 0.156"  # scripted group (container) (typed FeaturePython)
  n = 0.156214
FEATURE [App::DocumentObjectGroupPython] N_element027  label="N_element : 0.757"  # scripted group (container) (typed FeaturePython)
  n = 0.035451
FEATURE [App::DocumentObjectGroupPython] O_element067  label="O_element : 0.880"  # scripted group (container) (typed FeaturePython)
  n = 0.710101
FEATURE [App::DocumentObjectGroupPython] G4_MUSCLE_WITH_SUCROSE  # scripted group (container) (typed FeaturePython)
  Dunit = g/cm3
  Dvalue = 1.11
  Group = -> [H_element059,C_element065,N_element027,O_element067]
  conduct = 2
  density = 1
  expand = 3
  formula = G4_MUSCLE_WITH_SUCROSE
  name = G4_MUSCLE_WITH_SUCROSE
  specific = 4
FEATURE [App::DocumentObjectGroupPython] H_element060  label="H_element : 0.138"  # scripted group (container) (typed FeaturePython)
  n = 0.101969
FEATURE [App::DocumentObjectGroupPython] C_element066  label="C_element : 0.120"  # scripted group (container) (typed FeaturePython)
  n = 0.120058
FEATURE [App::DocumentObjectGroupPython] N_element028  label="N_element : 0.758"  # scripted group (container) (typed FeaturePython)
  n = 0.035451
FEATURE [App::DocumentObjectGroupPython] O_element068  label="O_element : 0.743"  # scripted group (container) (typed FeaturePython)
  n = 0.742522
FEATURE [App::DocumentObjectGroupPython] G4_MUSCLE_WITHOUT_SUCROSE  # scripted group (container) (typed FeaturePython)
  Dunit = g/cm3
  Dvalue = 1.07
  Group = -> [H_element060,C_element066,N_element028,O_element068]
  conduct = 2
  density = 1
  expand = 3
  formula = G4_MUSCLE_WITHOUT_SUCROSE
  name = G4_MUSCLE_WITHOUT_SUCROSE
  specific = 4
FEATURE [App::DocumentObjectGroupPython] C_element067  label="C_element : 10"  # scripted group (container) (typed FeaturePython)
  n = 10
  ref = C_element
FEATURE [App::DocumentObjectGroupPython] H_element061  label="H_element : 030"  # scripted group (container) (typed FeaturePython)
  n = 8
  ref = H_element
FEATURE [App::DocumentObjectGroupPython] G4_NAPHTHALENE  # scripted group (container) (typed FeaturePython)
  Dunit = g/cm3
  Dvalue = 1.145
  Group = -> [C_element067,H_element061]
  conduct = 2
  density = 1
  expand = 3
  formula = G4_NAPHTHALENE
  name = G4_NAPHTHALENE
  specific = 4
FEATURE [App::DocumentObjectGroupPython] C_element068  label="C_element : 034"  # scripted group (container) (typed FeaturePython)
  n = 6
  ref = C_element
FEATURE [App::DocumentObjectGroupPython] H_element062  label="H_element : 031"  # scripted group (container) (typed FeaturePython)
  n = 5
  ref = H_element
FEATURE [App::DocumentObjectGroupPython] N_element029  label="N_element : 012"  # scripted group (container) (typed FeaturePython)
  n = 1
  ref = N_element
FEATURE [App::DocumentObjectGroupPython] O_element069  label="O_element : 034"  # scripted group (container) (typed FeaturePython)
  n = 2
  ref = O_element
FEATURE [App::DocumentObjectGroupPython] G4_NITROBENZENE  # scripted group (container) (typed FeaturePython)
  Dunit = g/cm3
  Dvalue = 1.19867
  Group = -> [C_element068,H_element062,N_element029,O_element069]
  conduct = 2
  density = 1
  expand = 3
  formula = G4_NITROBENZENE
  name = G4_NITROBENZENE
  specific = 4
FEATURE [App::DocumentObjectGroupPython] N_element030  label="N_element : 013"  # scripted group (container) (typed FeaturePython)
  n = 2
  ref = N_element
FEATURE [App::DocumentObjectGroupPython] O_element070  label="O_element : 035"  # scripted group (container) (typed FeaturePython)
  n = 1
  ref = O_element
FEATURE [App::DocumentObjectGroupPython] G4_NITROUS_OXIDE  # scripted group (container) (typed FeaturePython)
  Dunit = g/cm3
  Dvalue = 0.00183094
  Group = -> [N_element030,O_element070]
  conduct = 2
  density = 1
  expand = 3
  formula = G4_NITROUS_OXIDE
  name = G4_NITROUS_OXIDE
  specific = 4
FEATURE [App::DocumentObjectGroupPython] H_element063  label="H_element : 0.104"  # scripted group (container) (typed FeaturePython)
  n = 0.103509
FEATURE [App::DocumentObjectGroupPython] C_element069  label="C_element : 0.648"  # scripted group (container) (typed FeaturePython)
  n = 0.648416
FEATURE [App::DocumentObjectGroupPython] N_element031  label="N_element : 0.100"  # scripted group (container) (typed FeaturePython)
  n = 0.0995361
FEATURE [App::DocumentObjectGroupPython] O_element071  label="O_element : 0.149"  # scripted group (container) (typed FeaturePython)
  n = 0.148539
FEATURE [App::DocumentObjectGroupPython] G4_NYLON_8062  label="G4_NYLON-8062"  # scripted group (container) (typed FeaturePython)
  Dunit = g/cm3
  Dvalue = 1.08
  Group = -> [H_element063,C_element069,N_element031,O_element071]
  conduct = 2
  density = 1
  expand = 3
  formula = G4_NYLON-8062
  name = G4_NYLON-8062
  specific = 4
FEATURE [App::DocumentObjectGroupPython] C_element070  label="C_element : 035"  # scripted group (container) (typed FeaturePython)
  n = 6
  ref = C_element
FEATURE [App::DocumentObjectGroupPython] H_element064  label="H_element : 11"  # scripted group (container) (typed FeaturePython)
  n = 11
  ref = H_element
FEATURE [App::DocumentObjectGroupPython] N_element032  label="N_element : 014"  # scripted group (container) (typed FeaturePython)
  n = 1
  ref = N_element
FEATURE [App::DocumentObjectGroupPython] O_element072  label="O_element : 036"  # scripted group (container) (typed FeaturePython)
  n = 1
  ref = O_element
FEATURE [App::DocumentObjectGroupPython] G4_NYLON_6_6  label="G4_NYLON-6-6"  # scripted group (container) (typed FeaturePython)
  Dunit = g/cm3
  Dvalue = 1.14
  Group = -> [C_element070,H_element064,N_element032,O_element072]
  conduct = 2
  density = 1
  expand = 3
  formula = G4_NYLON-6-6
  name = G4_NYLON-6-6
  specific = 4
FEATURE [App::DocumentObjectGroupPython] H_element065  label="H_element : 0.139"  # scripted group (container) (typed FeaturePython)
  n = 0.107062
FEATURE [App::DocumentObjectGroupPython] C_element071  label="C_element : 0.680"  # scripted group (container) (typed FeaturePython)
  n = 0.680449
FEATURE [App::DocumentObjectGroupPython] N_element033  label="N_element : 0.099"  # scripted group (container) (typed FeaturePython)
  n = 0.099189
FEATURE [App::DocumentObjectGroupPython] O_element073  label="O_element : 0.113"  # scripted group (container) (typed FeaturePython)
  n = 0.1133
FEATURE [App::DocumentObjectGroupPython] G4_NYLON_6_10  label="G4_NYLON-6-10"  # scripted group (container) (typed FeaturePython)
  Dunit = g/cm3
  Dvalue = 1.14
  Group = -> [H_element065,C_element071,N_element033,O_element073]
  conduct = 2
  density = 1
  expand = 3
  formula = G4_NYLON-6-10
  name = G4_NYLON-6-10
  specific = 4
FEATURE [App::DocumentObjectGroupPython] H_element066  label="H_element : 0.140"  # scripted group (container) (typed FeaturePython)
  n = 0.115476
FEATURE [App::DocumentObjectGroupPython] C_element072  label="C_element : 0.721"  # scripted group (container) (typed FeaturePython)
  n = 0.720818
FEATURE [App::DocumentObjectGroupPython] N_element034  label="N_element : 0.076"  # scripted group (container) (typed FeaturePython)
  n = 0.0764169
FEATURE [App::DocumentObjectGroupPython] O_element074  label="O_element : 0.087"  # scripted group (container) (typed FeaturePython)
  n = 0.0872889
FEATURE [App::DocumentObjectGroupPython] G4_NYLON_11_RILSAN  label="G4_NYLON-11_RILSAN"  # scripted group (container) (typed FeaturePython)
  Dunit = g/cm3
  Dvalue = 1.425
  Group = -> [H_element066,C_element072,N_element034,O_element074]
  conduct = 2
  density = 1
  expand = 3
  formula = G4_NYLON-11_RILSAN
  name = G4_NYLON-11_RILSAN
  specific = 4
FEATURE [App::DocumentObjectGroupPython] C_element073  label="C_element : 8"  # scripted group (container) (typed FeaturePython)
  n = 8
  ref = C_element
FEATURE [App::DocumentObjectGroupPython] H_element067  label="H_element : 18"  # scripted group (container) (typed FeaturePython)
  n = 18
  ref = H_element
FEATURE [App::DocumentObjectGroupPython] G4_OCTANE  # scripted group (container) (typed FeaturePython)
  Dunit = g/cm3
  Dvalue = 0.7026
  Group = -> [C_element073,H_element067]
  conduct = 2
  density = 1
  expand = 3
  formula = G4_OCTANE
  name = G4_OCTANE
  specific = 4
FEATURE [App::DocumentObjectGroupPython] C_element074  label="C_element : 25"  # scripted group (container) (typed FeaturePython)
  n = 25
  ref = C_element
FEATURE [App::DocumentObjectGroupPython] H_element068  label="H_element : 52"  # scripted group (container) (typed FeaturePython)
  n = 52
  ref = H_element
FEATURE [App::DocumentObjectGroupPython] G4_PARAFFIN  # scripted group (container) (typed FeaturePython)
  Dunit = g/cm3
  Dvalue = 0.93
  Group = -> [C_element074,H_element068]
  conduct = 2
  density = 1
  expand = 3
  formula = G4_PARAFFIN
  name = G4_PARAFFIN
  specific = 4
FEATURE [App::DocumentObjectGroupPython] C_element075  label="C_element : 036"  # scripted group (container) (typed FeaturePython)
  n = 5
  ref = C_element
FEATURE [App::DocumentObjectGroupPython] H_element069  label="H_element : 032"  # scripted group (container) (typed FeaturePython)
  n = 12
  ref = H_element
FEATURE [App::DocumentObjectGroupPython] G4_N_PENTANE  label="G4_N-PENTANE"  # scripted group (container) (typed FeaturePython)
  Dunit = g/cm3
  Dvalue = 0.6262
  Group = -> [C_element075,H_element069]
  conduct = 2
  density = 1
  expand = 3
  formula = G4_N-PENTANE
  name = G4_N-PENTANE
  specific = 4
FEATURE [App::DocumentObjectGroupPython] H_element070  label="H_element : 0.014"  # scripted group (container) (typed FeaturePython)
  n = 0.0141
FEATURE [App::DocumentObjectGroupPython] C_element076  label="C_element : 0.072"  # scripted group (container) (typed FeaturePython)
  n = 0.072261
FEATURE [App::DocumentObjectGroupPython] N_element035  label="N_element : 0.019"  # scripted group (container) (typed FeaturePython)
  n = 0.01932
FEATURE [App::DocumentObjectGroupPython] O_element075  label="O_element : 0.066"  # scripted group (container) (typed FeaturePython)
  n = 0.066101
FEATURE [App::DocumentObjectGroupPython] S_element019  label="S_element : 0.020"  # scripted group (container) (typed FeaturePython)
  n = 0.00189
FEATURE [App::DocumentObjectGroupPython] Br_element004  label="Br_element : 0.349"  # scripted group (container) (typed FeaturePython)
  n = 0.349103
FEATURE [App::DocumentObjectGroupPython] Ag_element001  label="Ag_element : 0.474"  # scripted group (container) (typed FeaturePython)
  n = 0.474105
FEATURE [App::DocumentObjectGroupPython] I_element005  label="I_element : 0.003"  # scripted group (container) (typed FeaturePython)
  n = 0.00312
FEATURE [App::DocumentObjectGroupPython] G4_PHOTO_EMULSION  # scripted group (container) (typed FeaturePython)
  Dunit = g/cm3
  Dvalue = 3.815
  Group = -> [H_element070,C_element076,N_element035,O_element075,S_element019,Br_element004,Ag_element001,I_element005]
  conduct = 2
  density = 1
  expand = 3
  formula = G4_PHOTO_EMULSION
  name = G4_PHOTO_EMULSION
  specific = 4
FEATURE [App::DocumentObjectGroupPython] C_element077  label="C_element : 9"  # scripted group (container) (typed FeaturePython)
  n = 9
  ref = C_element
FEATURE [App::DocumentObjectGroupPython] H_element071  label="H_element : 033"  # scripted group (container) (typed FeaturePython)
  n = 10
  ref = H_element
FEATURE [App::DocumentObjectGroupPython] G4_PLASTIC_SC_VINYLTOLUENE  # scripted group (container) (typed FeaturePython)
  Dunit = g/cm3
  Dvalue = 1.032
  Group = -> [C_element077,H_element071]
  conduct = 2
  density = 1
  expand = 3
  formula = G4_PLASTIC_SC_VINYLTOLUENE
  name = G4_PLASTIC_SC_VINYLTOLUENE
  specific = 4
FEATURE [App::DocumentObjectGroupPython] Pu_element001  label="Pu_element : 1"  # scripted group (container) (typed FeaturePython)
  n = 1
  ref = Pu_element
FEATURE [App::DocumentObjectGroupPython] O_element076  label="O_element : 037"  # scripted group (container) (typed FeaturePython)
  n = 2
  ref = O_element
FEATURE [App::DocumentObjectGroupPython] G4_PLUTONIUM_DIOXIDE  # scripted group (container) (typed FeaturePython)
  Dunit = g/cm3
  Dvalue = 11.46
  Group = -> [Pu_element001,O_element076]
  conduct = 2
  density = 1
  expand = 3
  formula = G4_PLUTONIUM_DIOXIDE
  name = G4_PLUTONIUM_DIOXIDE
  specific = 4
FEATURE [App::DocumentObjectGroupPython] C_element078  label="C_element : 037"  # scripted group (container) (typed FeaturePython)
  n = 3
  ref = C_element
FEATURE [App::DocumentObjectGroupPython] H_element072  label="H_element : 034"  # scripted group (container) (typed FeaturePython)
  n = 3
  ref = H_element
FEATURE [App::DocumentObjectGroupPython] N_element036  label="N_element : 015"  # scripted group (container) (typed FeaturePython)
  n = 1
  ref = N_element
FEATURE [App::DocumentObjectGroupPython] G4_POLYACRYLONITRILE  # scripted group (container) (typed FeaturePython)
  Dunit = g/cm3
  Dvalue = 1.17
  Group = -> [C_element078,H_element072,N_element036]
  conduct = 2
  density = 1
  expand = 3
  formula = G4_POLYACRYLONITRILE
  name = G4_POLYACRYLONITRILE
  specific = 4
FEATURE [App::DocumentObjectGroupPython] C_element079  label="C_element : 16"  # scripted group (container) (typed FeaturePython)
  n = 16
  ref = C_element
FEATURE [App::DocumentObjectGroupPython] H_element073  label="H_element : 035"  # scripted group (container) (typed FeaturePython)
  n = 14
  ref = H_element
FEATURE [App::DocumentObjectGroupPython] O_element077  label="O_element : 038"  # scripted group (container) (typed FeaturePython)
  n = 3
  ref = O_element
FEATURE [App::DocumentObjectGroupPython] G4_POLYCARBONATE  # scripted group (container) (typed FeaturePython)
  Dunit = g/cm3
  Dvalue = 1.2
  Group = -> [C_element079,H_element073,O_element077]
  conduct = 2
  density = 1
  expand = 3
  formula = G4_POLYCARBONATE
  name = G4_POLYCARBONATE
  specific = 4
FEATURE [App::DocumentObjectGroupPython] C_element080  label="C_element : 038"  # scripted group (container) (typed FeaturePython)
  n = 8
  ref = C_element
FEATURE [App::DocumentObjectGroupPython] H_element074  label="H_element : 036"  # scripted group (container) (typed FeaturePython)
  n = 7
  ref = H_element
FEATURE [App::DocumentObjectGroupPython] Cl_element017  label="Cl_element : 007"  # scripted group (container) (typed FeaturePython)
  n = 1
  ref = Cl_element
FEATURE [App::DocumentObjectGroupPython] G4_POLYCHLOROSTYRENE  # scripted group (container) (typed FeaturePython)
  Dunit = g/cm3
  Dvalue = 1.3
  Group = -> [C_element080,H_element074,Cl_element017]
  conduct = 2
  density = 1
  expand = 3
  formula = G4_POLYCHLOROSTYRENE
  name = G4_POLYCHLOROSTYRENE
  specific = 4
FEATURE [App::DocumentObjectGroupPython] C_element081  label="C_element : 039"  # scripted group (container) (typed FeaturePython)
  n = 1
  ref = C_element
FEATURE [App::DocumentObjectGroupPython] H_element075  label="H_element : 037"  # scripted group (container) (typed FeaturePython)
  n = 2
  ref = H_element
FEATURE [App::DocumentObjectGroupPython] G4_POLYETHYLENE  # scripted group (container) (typed FeaturePython)
  Dunit = g/cm3
  Dvalue = 0.94
  Group = -> [C_element081,H_element075]
  conduct = 2
  density = 1
  expand = 3
  formula = G4_POLYETHYLENE
  name = G4_POLYETHYLENE
  specific = 4
FEATURE [App::DocumentObjectGroupPython] C_element082  label="C_element : 040"  # scripted group (container) (typed FeaturePython)
  n = 10
  ref = C_element
FEATURE [App::DocumentObjectGroupPython] H_element076  label="H_element : 038"  # scripted group (container) (typed FeaturePython)
  n = 8
  ref = H_element
FEATURE [App::DocumentObjectGroupPython] O_element078  label="O_element : 039"  # scripted group (container) (typed FeaturePython)
  n = 4
  ref = O_element
FEATURE [App::DocumentObjectGroupPython] G4_MYLAR  # scripted group (container) (typed FeaturePython)
  Dunit = g/cm3
  Dvalue = 1.4
  Group = -> [C_element082,H_element076,O_element078]
  conduct = 2
  density = 1
  expand = 3
  formula = G4_MYLAR
  name = G4_MYLAR
  specific = 4
FEATURE [App::DocumentObjectGroupPython] C_element083  label="C_element : 041"  # scripted group (container) (typed FeaturePython)
  n = 5
  ref = C_element
FEATURE [App::DocumentObjectGroupPython] H_element077  label="H_element : 039"  # scripted group (container) (typed FeaturePython)
  n = 8
  ref = H_element
FEATURE [App::DocumentObjectGroupPython] O_element079  label="O_element : 040"  # scripted group (container) (typed FeaturePython)
  n = 2
  ref = O_element
FEATURE [App::DocumentObjectGroupPython] G4_PLEXIGLASS  # scripted group (container) (typed FeaturePython)
  Dunit = g/cm3
  Dvalue = 1.19
  Group = -> [C_element083,H_element077,O_element079]
  conduct = 2
  density = 1
  expand = 3
  formula = G4_PLEXIGLASS
  name = G4_PLEXIGLASS
  specific = 4
FEATURE [App::DocumentObjectGroupPython] C_element084  label="C_element : 042"  # scripted group (container) (typed FeaturePython)
  n = 1
  ref = C_element
FEATURE [App::DocumentObjectGroupPython] H_element078  label="H_element : 040"  # scripted group (container) (typed FeaturePython)
  n = 2
  ref = H_element
FEATURE [App::DocumentObjectGroupPython] O_element080  label="O_element : 041"  # scripted group (container) (typed FeaturePython)
  n = 1
  ref = O_element
FEATURE [App::DocumentObjectGroupPython] G4_POLYOXYMETHYLENE  # scripted group (container) (typed FeaturePython)
  Dunit = g/cm3
  Dvalue = 1.425
  Group = -> [C_element084,H_element078,O_element080]
  conduct = 2
  density = 1
  expand = 3
  formula = G4_POLYOXYMETHYLENE
  name = G4_POLYOXYMETHYLENE
  specific = 4
FEATURE [App::DocumentObjectGroupPython] C_element085  label="C_element : 043"  # scripted group (container) (typed FeaturePython)
  n = 2
  ref = C_element
FEATURE [App::DocumentObjectGroupPython] H_element079  label="H_element : 041"  # scripted group (container) (typed FeaturePython)
  n = 4
  ref = H_element
FEATURE [App::DocumentObjectGroupPython] G4_POLYPROPYLENE  # scripted group (container) (typed FeaturePython)
  Dunit = g/cm3
  Dvalue = 0.9
  Group = -> [C_element085,H_element079]
  conduct = 2
  density = 1
  expand = 3
  formula = G4_POLYPROPYLENE
  name = G4_POLYPROPYLENE
  specific = 4
FEATURE [App::DocumentObjectGroupPython] C_element086  label="C_element : 044"  # scripted group (container) (typed FeaturePython)
  n = 8
  ref = C_element
FEATURE [App::DocumentObjectGroupPython] H_element080  label="H_element : 042"  # scripted group (container) (typed FeaturePython)
  n = 8
  ref = H_element
FEATURE [App::DocumentObjectGroupPython] G4_POLYSTYRENE  # scripted group (container) (typed FeaturePython)
  Dunit = g/cm3
  Dvalue = 1.06
  Group = -> [C_element086,H_element080]
  conduct = 2
  density = 1
  expand = 3
  formula = G4_POLYSTYRENE
  name = G4_POLYSTYRENE
  specific = 4
FEATURE [App::DocumentObjectGroupPython] C_element087  label="C_element : 045"  # scripted group (container) (typed FeaturePython)
  n = 2
  ref = C_element
FEATURE [App::DocumentObjectGroupPython] F_element014  label="F_element : 4"  # scripted group (container) (typed FeaturePython)
  n = 4
  ref = F_element
FEATURE [App::DocumentObjectGroupPython] G4_TEFLON  # scripted group (container) (typed FeaturePython)
  Dunit = g/cm3
  Dvalue = 2.2
  Group = -> [C_element087,F_element014]
  conduct = 2
  density = 1
  expand = 3
  formula = G4_TEFLON
  name = G4_TEFLON
  specific = 4
FEATURE [App::DocumentObjectGroupPython] C_element088  label="C_element : 046"  # scripted group (container) (typed FeaturePython)
  n = 2
  ref = C_element
FEATURE [App::DocumentObjectGroupPython] F_element015  label="F_element : 006"  # scripted group (container) (typed FeaturePython)
  n = 3
  ref = F_element
FEATURE [App::DocumentObjectGroupPython] Cl_element018  label="Cl_element : 008"  # scripted group (container) (typed FeaturePython)
  n = 1
  ref = Cl_element
FEATURE [App::DocumentObjectGroupPython] G4_POLYTRIFLUOROCHLOROETHYLENE  # scripted group (container) (typed FeaturePython)
  Dunit = g/cm3
  Dvalue = 2.1
  Group = -> [C_element088,F_element015,Cl_element018]
  conduct = 2
  density = 1
  expand = 3
  formula = G4_POLYTRIFLUOROCHLOROETHYLENE
  name = G4_POLYTRIFLUOROCHLOROETHYLENE
  specific = 4
FEATURE [App::DocumentObjectGroupPython] C_element089  label="C_element : 047"  # scripted group (container) (typed FeaturePython)
  n = 4
  ref = C_element
FEATURE [App::DocumentObjectGroupPython] H_element081  label="H_element : 043"  # scripted group (container) (typed FeaturePython)
  n = 6
  ref = H_element
FEATURE [App::DocumentObjectGroupPython] O_element081  label="O_element : 042"  # scripted group (container) (typed FeaturePython)
  n = 2
  ref = O_element
FEATURE [App::DocumentObjectGroupPython] G4_POLYVINYL_ACETATE  # scripted group (container) (typed FeaturePython)
  Dunit = g/cm3
  Dvalue = 1.19
  Group = -> [C_element089,H_element081,O_element081]
  conduct = 2
  density = 1
  expand = 3
  formula = G4_POLYVINYL_ACETATE
  name = G4_POLYVINYL_ACETATE
  specific = 4
FEATURE [App::DocumentObjectGroupPython] C_element090  label="C_element : 048"  # scripted group (container) (typed FeaturePython)
  n = 2
  ref = C_element
FEATURE [App::DocumentObjectGroupPython] H_element082  label="H_element : 044"  # scripted group (container) (typed FeaturePython)
  n = 4
  ref = H_element
FEATURE [App::DocumentObjectGroupPython] O_element082  label="O_element : 043"  # scripted group (container) (typed FeaturePython)
  n = 1
  ref = O_element
FEATURE [App::DocumentObjectGroupPython] G4_POLYVINYL_ALCOHOL  # scripted group (container) (typed FeaturePython)
  Dunit = g/cm3
  Dvalue = 1.3
  Group = -> [C_element090,H_element082,O_element082]
  conduct = 2
  density = 1
  expand = 3
  formula = G4_POLYVINYL_ALCOHOL
  name = G4_POLYVINYL_ALCOHOL
  specific = 4
FEATURE [App::DocumentObjectGroupPython] C_element091  label="C_element : 049"  # scripted group (container) (typed FeaturePython)
  n = 8
  ref = C_element
FEATURE [App::DocumentObjectGroupPython] H_element083  label="H_element : 045"  # scripted group (container) (typed FeaturePython)
  n = 14
  ref = H_element
FEATURE [App::DocumentObjectGroupPython] O_element083  label="O_element : 044"  # scripted group (container) (typed FeaturePython)
  n = 2
  ref = O_element
FEATURE [App::DocumentObjectGroupPython] G4_POLYVINYL_BUTYRAL  # scripted group (container) (typed FeaturePython)
  Dunit = g/cm3
  Dvalue = 1.12
  Group = -> [C_element091,H_element083,O_element083]
  conduct = 2
  density = 1
  expand = 3
  formula = G4_POLYVINYL_BUTYRAL
  name = G4_POLYVINYL_BUTYRAL
  specific = 4
FEATURE [App::DocumentObjectGroupPython] C_element092  label="C_element : 050"  # scripted group (container) (typed FeaturePython)
  n = 2
  ref = C_element
FEATURE [App::DocumentObjectGroupPython] H_element084  label="H_element : 046"  # scripted group (container) (typed FeaturePython)
  n = 3
  ref = H_element
FEATURE [App::DocumentObjectGroupPython] Cl_element019  label="Cl_element : 009"  # scripted group (container) (typed FeaturePython)
  n = 1
  ref = Cl_element
FEATURE [App::DocumentObjectGroupPython] G4_POLYVINYL_CHLORIDE  # scripted group (container) (typed FeaturePython)
  Dunit = g/cm3
  Dvalue = 1.3
  Group = -> [C_element092,H_element084,Cl_element019]
  conduct = 2
  density = 1
  expand = 3
  formula = G4_POLYVINYL_CHLORIDE
  name = G4_POLYVINYL_CHLORIDE
  specific = 4
FEATURE [App::DocumentObjectGroupPython] C_element093  label="C_element : 051"  # scripted group (container) (typed FeaturePython)
  n = 2
  ref = C_element
FEATURE [App::DocumentObjectGroupPython] H_element085  label="H_element : 047"  # scripted group (container) (typed FeaturePython)
  n = 2
  ref = H_element
FEATURE [App::DocumentObjectGroupPython] Cl_element020  label="Cl_element : 010"  # scripted group (container) (typed FeaturePython)
  n = 2
  ref = Cl_element
FEATURE [App::DocumentObjectGroupPython] G4_POLYVINYLIDENE_CHLORIDE  # scripted group (container) (typed FeaturePython)
  Dunit = g/cm3
  Dvalue = 1.7
  Group = -> [C_element093,H_element085,Cl_element020]
  conduct = 2
  density = 1
  expand = 3
  formula = G4_POLYVINYLIDENE_CHLORIDE
  name = G4_POLYVINYLIDENE_CHLORIDE
  specific = 4
FEATURE [App::DocumentObjectGroupPython] C_element094  label="C_element : 052"  # scripted group (container) (typed FeaturePython)
  n = 2
  ref = C_element
FEATURE [App::DocumentObjectGroupPython] H_element086  label="H_element : 048"  # scripted group (container) (typed FeaturePython)
  n = 2
  ref = H_element
FEATURE [App::DocumentObjectGroupPython] F_element016  label="F_element : 007"  # scripted group (container) (typed FeaturePython)
  n = 2
  ref = F_element
FEATURE [App::DocumentObjectGroupPython] G4_POLYVINYLIDENE_FLUORIDE  # scripted group (container) (typed FeaturePython)
  Dunit = g/cm3
  Dvalue = 1.76
  Group = -> [C_element094,H_element086,F_element016]
  conduct = 2
  density = 1
  expand = 3
  formula = G4_POLYVINYLIDENE_FLUORIDE
  name = G4_POLYVINYLIDENE_FLUORIDE
  specific = 4
FEATURE [App::DocumentObjectGroupPython] C_element095  label="C_element : 053"  # scripted group (container) (typed FeaturePython)
  n = 6
  ref = C_element
FEATURE [App::DocumentObjectGroupPython] H_element087  label="H_element : 9"  # scripted group (container) (typed FeaturePython)
  n = 9
  ref = H_element
FEATURE [App::DocumentObjectGroupPython] N_element037  label="N_element : 016"  # scripted group (container) (typed FeaturePython)
  n = 1
  ref = N_element
FEATURE [App::DocumentObjectGroupPython] O_element084  label="O_element : 045"  # scripted group (container) (typed FeaturePython)
  n = 1
  ref = O_element
FEATURE [App::DocumentObjectGroupPython] G4_POLYVINYL_PYRROLIDONE  # scripted group (container) (typed FeaturePython)
  Dunit = g/cm3
  Dvalue = 1.25
  Group = -> [C_element095,H_element087,N_element037,O_element084]
  conduct = 2
  density = 1
  expand = 3
  formula = G4_POLYVINYL_PYRROLIDONE
  name = G4_POLYVINYL_PYRROLIDONE
  specific = 4
FEATURE [App::DocumentObjectGroupPython] K_element008  label="K_element : 1"  # scripted group (container) (typed FeaturePython)
  n = 1
  ref = K_element
FEATURE [App::DocumentObjectGroupPython] I_element006  label="I_element : 003"  # scripted group (container) (typed FeaturePython)
  n = 1
  ref = I_element
FEATURE [App::DocumentObjectGroupPython] G4_POTASSIUM_IODIDE  # scripted group (container) (typed FeaturePython)
  Dunit = g/cm3
  Dvalue = 3.13
  Group = -> [K_element008,I_element006]
  conduct = 2
  density = 1
  expand = 3
  formula = G4_POTASSIUM_IODIDE
  name = G4_POTASSIUM_IODIDE
  specific = 4
FEATURE [App::DocumentObjectGroupPython] K_element009  label="K_element : 2"  # scripted group (container) (typed FeaturePython)
  n = 2
  ref = K_element
FEATURE [App::DocumentObjectGroupPython] O_element085  label="O_element : 046"  # scripted group (container) (typed FeaturePython)
  n = 1
  ref = O_element
FEATURE [App::DocumentObjectGroupPython] G4_POTASSIUM_OXIDE  # scripted group (container) (typed FeaturePython)
  Dunit = g/cm3
  Dvalue = 2.32
  Group = -> [K_element009,O_element085]
  conduct = 2
  density = 1
  expand = 3
  formula = G4_POTASSIUM_OXIDE
  name = G4_POTASSIUM_OXIDE
  specific = 4
FEATURE [App::DocumentObjectGroupPython] C_element096  label="C_element : 054"  # scripted group (container) (typed FeaturePython)
  n = 3
  ref = C_element
FEATURE [App::DocumentObjectGroupPython] H_element088  label="H_element : 049"  # scripted group (container) (typed FeaturePython)
  n = 8
  ref = H_element
FEATURE [App::DocumentObjectGroupPython] G4_PROPANE  # scripted group (container) (typed FeaturePython)
  Dunit = g/cm3
  Dvalue = 0.00187939
  Group = -> [C_element096,H_element088]
  conduct = 2
  density = 1
  expand = 3
  formula = G4_PROPANE
  name = G4_PROPANE
  specific = 4
FEATURE [App::DocumentObjectGroupPython] C_element097  label="C_element : 055"  # scripted group (container) (typed FeaturePython)
  n = 3
  ref = C_element
FEATURE [App::DocumentObjectGroupPython] H_element089  label="H_element : 050"  # scripted group (container) (typed FeaturePython)
  n = 8
  ref = H_element
FEATURE [App::DocumentObjectGroupPython] G4_lPROPANE  # scripted group (container) (typed FeaturePython)
  Dunit = g/cm3
  Dvalue = 0.43
  Group = -> [C_element097,H_element089]
  conduct = 2
  density = 1
  expand = 3
  formula = G4_lPROPANE
  name = G4_lPROPANE
  specific = 4
FEATURE [App::DocumentObjectGroupPython] C_element098  label="C_element : 056"  # scripted group (container) (typed FeaturePython)
  n = 3
  ref = C_element
FEATURE [App::DocumentObjectGroupPython] H_element090  label="H_element : 051"  # scripted group (container) (typed FeaturePython)
  n = 8
  ref = H_element
FEATURE [App::DocumentObjectGroupPython] O_element086  label="O_element : 047"  # scripted group (container) (typed FeaturePython)
  n = 1
  ref = O_element
FEATURE [App::DocumentObjectGroupPython] G4_N_PROPYL_ALCOHOL  label="G4_N-PROPYL_ALCOHOL"  # scripted group (container) (typed FeaturePython)
  Dunit = g/cm3
  Dvalue = 0.8035
  Group = -> [C_element098,H_element090,O_element086]
  conduct = 2
  density = 1
  expand = 3
  formula = G4_N-PROPYL_ALCOHOL
  name = G4_N-PROPYL_ALCOHOL
  specific = 4
FEATURE [App::DocumentObjectGroupPython] C_element099  label="C_element : 057"  # scripted group (container) (typed FeaturePython)
  n = 5
  ref = C_element
FEATURE [App::DocumentObjectGroupPython] H_element091  label="H_element : 052"  # scripted group (container) (typed FeaturePython)
  n = 5
  ref = H_element
FEATURE [App::DocumentObjectGroupPython] N_element038  label="N_element : 017"  # scripted group (container) (typed FeaturePython)
  n = 1
  ref = N_element
FEATURE [App::DocumentObjectGroupPython] G4_PYRIDINE  # scripted group (container) (typed FeaturePython)
  Dunit = g/cm3
  Dvalue = 0.9819
  Group = -> [C_element099,H_element091,N_element038]
  conduct = 2
  density = 1
  expand = 3
  formula = G4_PYRIDINE
  name = G4_PYRIDINE
  specific = 4
FEATURE [App::DocumentObjectGroupPython] H_element092  label="H_element : 0.144"  # scripted group (container) (typed FeaturePython)
  n = 0.143711
FEATURE [App::DocumentObjectGroupPython] C_element100  label="C_element : 0.856"  # scripted group (container) (typed FeaturePython)
  n = 0.856289
FEATURE [App::DocumentObjectGroupPython] G4_RUBBER_BUTYL  # scripted group (container) (typed FeaturePython)
  Dunit = g/cm3
  Dvalue = 0.92
  Group = -> [H_element092,C_element100]
  conduct = 2
  density = 1
  expand = 3
  formula = G4_RUBBER_BUTYL
  name = G4_RUBBER_BUTYL
  specific = 4
FEATURE [App::DocumentObjectGroupPython] H_element093  label="H_element : 0.118"  # scripted group (container) (typed FeaturePython)
  n = 0.118371
FEATURE [App::DocumentObjectGroupPython] C_element101  label="C_element : 0.882"  # scripted group (container) (typed FeaturePython)
  n = 0.881629
FEATURE [App::DocumentObjectGroupPython] G4_RUBBER_NATURAL  # scripted group (container) (typed FeaturePython)
  Dunit = g/cm3
  Dvalue = 0.92
  Group = -> [H_element093,C_element101]
  conduct = 2
  density = 1
  expand = 3
  formula = G4_RUBBER_NATURAL
  name = G4_RUBBER_NATURAL
  specific = 4
FEATURE [App::DocumentObjectGroupPython] H_element094  label="H_element : 0.145"  # scripted group (container) (typed FeaturePython)
  n = 0.05692
FEATURE [App::DocumentObjectGroupPython] C_element102  label="C_element : 0.543"  # scripted group (container) (typed FeaturePython)
  n = 0.542646
FEATURE [App::DocumentObjectGroupPython] Cl_element021  label="Cl_element : 0.400"  # scripted group (container) (typed FeaturePython)
  n = 0.400434
FEATURE [App::DocumentObjectGroupPython] G4_RUBBER_NEOPRENE  # scripted group (container) (typed FeaturePython)
  Dunit = g/cm3
  Dvalue = 1.23
  Group = -> [H_element094,C_element102,Cl_element021]
  conduct = 2
  density = 1
  expand = 3
  formula = G4_RUBBER_NEOPRENE
  name = G4_RUBBER_NEOPRENE
  specific = 4
FEATURE [App::DocumentObjectGroupPython] Si_element006  label="Si_element : 1"  # scripted group (container) (typed FeaturePython)
  n = 1
  ref = Si_element
FEATURE [App::DocumentObjectGroupPython] O_element087  label="O_element : 048"  # scripted group (container) (typed FeaturePython)
  n = 2
  ref = O_element
FEATURE [App::DocumentObjectGroupPython] G4_SILICON_DIOXIDE  # scripted group (container) (typed FeaturePython)
  Dunit = g/cm3
  Dvalue = 2.32
  Group = -> [Si_element006,O_element087]
  conduct = 2
  density = 1
  expand = 3
  formula = G4_SILICON_DIOXIDE
  name = G4_SILICON_DIOXIDE
  specific = 4
FEATURE [App::DocumentObjectGroupPython] Ag_element002  label="Ag_element : 1"  # scripted group (container) (typed FeaturePython)
  n = 1
  ref = Ag_element
FEATURE [App::DocumentObjectGroupPython] Br_element005  label="Br_element : 003"  # scripted group (container) (typed FeaturePython)
  n = 1
  ref = Br_element
FEATURE [App::DocumentObjectGroupPython] G4_SILVER_BROMIDE  # scripted group (container) (typed FeaturePython)
  Dunit = g/cm3
  Dvalue = 6.473
  Group = -> [Ag_element002,Br_element005]
  conduct = 2
  density = 1
  expand = 3
  formula = G4_SILVER_BROMIDE
  name = G4_SILVER_BROMIDE
  specific = 4
FEATURE [App::DocumentObjectGroupPython] Ag_element003  label="Ag_element : 002"  # scripted group (container) (typed FeaturePython)
  n = 1
  ref = Ag_element
FEATURE [App::DocumentObjectGroupPython] Cl_element022  label="Cl_element : 011"  # scripted group (container) (typed FeaturePython)
  n = 1
  ref = Cl_element
FEATURE [App::DocumentObjectGroupPython] G4_SILVER_CHLORIDE  # scripted group (container) (typed FeaturePython)
  Dunit = g/cm3
  Dvalue = 5.56
  Group = -> [Ag_element003,Cl_element022]
  conduct = 2
  density = 1
  expand = 3
  formula = G4_SILVER_CHLORIDE
  name = G4_SILVER_CHLORIDE
  specific = 4
FEATURE [App::DocumentObjectGroupPython] Br_element006  label="Br_element : 0.423"  # scripted group (container) (typed FeaturePython)
  n = 0.422895
FEATURE [App::DocumentObjectGroupPython] Ag_element004  label="Ag_element : 0.574"  # scripted group (container) (typed FeaturePython)
  n = 0.573748
FEATURE [App::DocumentObjectGroupPython] I_element007  label="I_element : 0.649"  # scripted group (container) (typed FeaturePython)
  n = 0.003357
FEATURE [App::DocumentObjectGroupPython] G4_SILVER_HALIDES  # scripted group (container) (typed FeaturePython)
  Dunit = g/cm3
  Dvalue = 6.47
  Group = -> [Br_element006,Ag_element004,I_element007]
  conduct = 2
  density = 1
  expand = 3
  formula = G4_SILVER_HALIDES
  name = G4_SILVER_HALIDES
  specific = 4
FEATURE [App::DocumentObjectGroupPython] Ag_element005  label="Ag_element : 003"  # scripted group (container) (typed FeaturePython)
  n = 1
  ref = Ag_element
FEATURE [App::DocumentObjectGroupPython] I_element008  label="I_element : 004"  # scripted group (container) (typed FeaturePython)
  n = 1
  ref = I_element
FEATURE [App::DocumentObjectGroupPython] G4_SILVER_IODIDE  # scripted group (container) (typed FeaturePython)
  Dunit = g/cm3
  Dvalue = 6.01
  Group = -> [Ag_element005,I_element008]
  conduct = 2
  density = 1
  expand = 3
  formula = G4_SILVER_IODIDE
  name = G4_SILVER_IODIDE
  specific = 4
FEATURE [App::DocumentObjectGroupPython] H_element095  label="H_element : 0.100"  # scripted group (container) (typed FeaturePython)
  n = 0.1
FEATURE [App::DocumentObjectGroupPython] C_element103  label="C_element : 0.204"  # scripted group (container) (typed FeaturePython)
  n = 0.204
FEATURE [App::DocumentObjectGroupPython] N_element039  label="N_element : 0.759"  # scripted group (container) (typed FeaturePython)
  n = 0.042
FEATURE [App::DocumentObjectGroupPython] O_element088  label="O_element : 0.645"  # scripted group (container) (typed FeaturePython)
  n = 0.645
FEATURE [App::DocumentObjectGroupPython] Na_element013  label="Na_element : 0.100"  # scripted group (container) (typed FeaturePython)
  n = 0.002
FEATURE [App::DocumentObjectGroupPython] P_element009  label="P_element : 0.107"  # scripted group (container) (typed FeaturePython)
  n = 0.001
FEATURE [App::DocumentObjectGroupPython] S_element020  label="S_element : 0.021"  # scripted group (container) (typed FeaturePython)
  n = 0.002
FEATURE [App::DocumentObjectGroupPython] Cl_element023  label="Cl_element : 0.590"  # scripted group (container) (typed FeaturePython)
  n = 0.003
FEATURE [App::DocumentObjectGroupPython] K_element010  label="K_element : 0.001"  # scripted group (container) (typed FeaturePython)
  n = 0.001
FEATURE [App::DocumentObjectGroupPython] G4_SKIN_ICRP  # scripted group (container) (typed FeaturePython)
  Dunit = g/cm3
  Dvalue = 1.09
  Group = -> [H_element095,C_element103,N_element039,O_element088,Na_element013,P_element009,S_element020,Cl_element023,K_element010]
  conduct = 2
  density = 1
  expand = 3
  formula = G4_SKIN_ICRP
  name = G4_SKIN_ICRP
  specific = 4
FEATURE [App::DocumentObjectGroupPython] Na_element014  label="Na_element : 2"  # scripted group (container) (typed FeaturePython)
  n = 2
  ref = Na_element
FEATURE [App::DocumentObjectGroupPython] C_element104  label="C_element : 058"  # scripted group (container) (typed FeaturePython)
  n = 1
  ref = C_element
FEATURE [App::DocumentObjectGroupPython] O_element089  label="O_element : 049"  # scripted group (container) (typed FeaturePython)
  n = 3
  ref = O_element
FEATURE [App::DocumentObjectGroupPython] G4_SODIUM_CARBONATE  # scripted group (container) (typed FeaturePython)
  Dunit = g/cm3
  Dvalue = 2.532
  Group = -> [Na_element014,C_element104,O_element089]
  conduct = 2
  density = 1
  expand = 3
  formula = G4_SODIUM_CARBONATE
  name = G4_SODIUM_CARBONATE
  specific = 4
FEATURE [App::DocumentObjectGroupPython] Na_element015  label="Na_element : 1"  # scripted group (container) (typed FeaturePython)
  n = 1
  ref = Na_element
FEATURE [App::DocumentObjectGroupPython] I_element009  label="I_element : 005"  # scripted group (container) (typed FeaturePython)
  n = 1
  ref = I_element
FEATURE [App::DocumentObjectGroupPython] G4_SODIUM_IODIDE  # scripted group (container) (typed FeaturePython)
  Dunit = g/cm3
  Dvalue = 3.667
  Group = -> [Na_element015,I_element009]
  conduct = 2
  density = 1
  expand = 3
  formula = G4_SODIUM_IODIDE
  name = G4_SODIUM_IODIDE
  specific = 4
FEATURE [App::DocumentObjectGroupPython] Na_element016  label="Na_element : 003"  # scripted group (container) (typed FeaturePython)
  n = 2
  ref = Na_element
FEATURE [App::DocumentObjectGroupPython] O_element090  label="O_element : 050"  # scripted group (container) (typed FeaturePython)
  n = 1
  ref = O_element
FEATURE [App::DocumentObjectGroupPython] G4_SODIUM_MONOXIDE  # scripted group (container) (typed FeaturePython)
  Dunit = g/cm3
  Dvalue = 2.27
  Group = -> [Na_element016,O_element090]
  conduct = 2
  density = 1
  expand = 3
  formula = G4_SODIUM_MONOXIDE
  name = G4_SODIUM_MONOXIDE
  specific = 4
FEATURE [App::DocumentObjectGroupPython] Na_element017  label="Na_element : 004"  # scripted group (container) (typed FeaturePython)
  n = 1
  ref = Na_element
FEATURE [App::DocumentObjectGroupPython] N_element040  label="N_element : 018"  # scripted group (container) (typed FeaturePython)
  n = 1
  ref = N_element
FEATURE [App::DocumentObjectGroupPython] O_element091  label="O_element : 051"  # scripted group (container) (typed FeaturePython)
  n = 3
  ref = O_element
FEATURE [App::DocumentObjectGroupPython] G4_SODIUM_NITRATE  # scripted group (container) (typed FeaturePython)
  Dunit = g/cm3
  Dvalue = 2.261
  Group = -> [Na_element017,N_element040,O_element091]
  conduct = 2
  density = 1
  expand = 3
  formula = G4_SODIUM_NITRATE
  name = G4_SODIUM_NITRATE
  specific = 4
FEATURE [App::DocumentObjectGroupPython] C_element105  label="C_element : 059"  # scripted group (container) (typed FeaturePython)
  n = 14
  ref = C_element
FEATURE [App::DocumentObjectGroupPython] H_element096  label="H_element : 053"  # scripted group (container) (typed FeaturePython)
  n = 12
  ref = H_element
FEATURE [App::DocumentObjectGroupPython] G4_STILBENE  # scripted group (container) (typed FeaturePython)
  Dunit = g/cm3
  Dvalue = 0.9707
  Group = -> [C_element105,H_element096]
  conduct = 2
  density = 1
  expand = 3
  formula = G4_STILBENE
  name = G4_STILBENE
  specific = 4
FEATURE [App::DocumentObjectGroupPython] C_element106  label="C_element : 12"  # scripted group (container) (typed FeaturePython)
  n = 12
  ref = C_element
FEATURE [App::DocumentObjectGroupPython] H_element097  label="H_element : 22"  # scripted group (container) (typed FeaturePython)
  n = 22
  ref = H_element
FEATURE [App::DocumentObjectGroupPython] O_element092  label="O_element : 11"  # scripted group (container) (typed FeaturePython)
  n = 11
  ref = O_element
FEATURE [App::DocumentObjectGroupPython] G4_SUCROSE  # scripted group (container) (typed FeaturePython)
  Dunit = g/cm3
  Dvalue = 1.5805
  Group = -> [C_element106,H_element097,O_element092]
  conduct = 2
  density = 1
  expand = 3
  formula = G4_SUCROSE
  name = G4_SUCROSE
  specific = 4
FEATURE [App::DocumentObjectGroupPython] C_element107  label="C_element : 18"  # scripted group (container) (typed FeaturePython)
  n = 18
  ref = C_element
FEATURE [App::DocumentObjectGroupPython] H_element098  label="H_element : 054"  # scripted group (container) (typed FeaturePython)
  n = 14
  ref = H_element
FEATURE [App::DocumentObjectGroupPython] G4_TERPHENYL  # scripted group (container) (typed FeaturePython)
  Dunit = g/cm3
  Dvalue = 1.24
  Group = -> [C_element107,H_element098]
  conduct = 2
  density = 1
  expand = 3
  formula = G4_TERPHENYL
  name = G4_TERPHENYL
  specific = 4
FEATURE [App::DocumentObjectGroupPython] H_element099  label="H_element : 0.146"  # scripted group (container) (typed FeaturePython)
  n = 0.106
FEATURE [App::DocumentObjectGroupPython] C_element108  label="C_element : 0.883"  # scripted group (container) (typed FeaturePython)
  n = 0.099
FEATURE [App::DocumentObjectGroupPython] N_element041  label="N_element : 0.020"  # scripted group (container) (typed FeaturePython)
  n = 0.02
FEATURE [App::DocumentObjectGroupPython] O_element093  label="O_element : 0.766"  # scripted group (container) (typed FeaturePython)
  n = 0.766
FEATURE [App::DocumentObjectGroupPython] Na_element018  label="Na_element : 0.101"  # scripted group (container) (typed FeaturePython)
  n = 0.002
FEATURE [App::DocumentObjectGroupPython] P_element010  label="P_element : 0.108"  # scripted group (container) (typed FeaturePython)
  n = 0.001
FEATURE [App::DocumentObjectGroupPython] S_element021  label="S_element : 0.022"  # scripted group (container) (typed FeaturePython)
  n = 0.002
FEATURE [App::DocumentObjectGroupPython] Cl_element024  label="Cl_element : 0.002"  # scripted group (container) (typed FeaturePython)
  n = 0.002
FEATURE [App::DocumentObjectGroupPython] K_element011  label="K_element : 0.017"  # scripted group (container) (typed FeaturePython)
  n = 0.002
FEATURE [App::DocumentObjectGroupPython] G4_TESTIS_ICRP  # scripted group (container) (typed FeaturePython)
  Dunit = g/cm3
  Dvalue = 1.04
  Group = -> [H_element099,C_element108,N_element041,O_element093,Na_element018,P_element010,S_element021,Cl_element024,K_element011]
  conduct = 2
  density = 1
  expand = 3
  formula = G4_TESTIS_ICRP
  name = G4_TESTIS_ICRP
  specific = 4
FEATURE [App::DocumentObjectGroupPython] C_element109  label="C_element : 060"  # scripted group (container) (typed FeaturePython)
  n = 2
  ref = C_element
FEATURE [App::DocumentObjectGroupPython] Cl_element025  label="Cl_element : 012"  # scripted group (container) (typed FeaturePython)
  n = 4
  ref = Cl_element
FEATURE [App::DocumentObjectGroupPython] G4_TETRACHLOROETHYLENE  # scripted group (container) (typed FeaturePython)
  Dunit = g/cm3
  Dvalue = 1.625
  Group = -> [C_element109,Cl_element025]
  conduct = 2
  density = 1
  expand = 3
  formula = G4_TETRACHLOROETHYLENE
  name = G4_TETRACHLOROETHYLENE
  specific = 4
FEATURE [App::DocumentObjectGroupPython] Tl_element001  label="Tl_element : 1"  # scripted group (container) (typed FeaturePython)
  n = 1
  ref = Tl_element
FEATURE [App::DocumentObjectGroupPython] Cl_element026  label="Cl_element : 013"  # scripted group (container) (typed FeaturePython)
  n = 1
  ref = Cl_element
FEATURE [App::DocumentObjectGroupPython] G4_THALLIUM_CHLORIDE  # scripted group (container) (typed FeaturePython)
  Dunit = g/cm3
  Dvalue = 7.004
  Group = -> [Tl_element001,Cl_element026]
  conduct = 2
  density = 1
  expand = 3
  formula = G4_THALLIUM_CHLORIDE
  name = G4_THALLIUM_CHLORIDE
  specific = 4
FEATURE [App::DocumentObjectGroupPython] H_element100  label="H_element : 0.147"  # scripted group (container) (typed FeaturePython)
  n = 0.105
FEATURE [App::DocumentObjectGroupPython] C_element110  label="C_element : 0.256"  # scripted group (container) (typed FeaturePython)
  n = 0.256
FEATURE [App::DocumentObjectGroupPython] N_element042  label="N_element : 0.760"  # scripted group (container) (typed FeaturePython)
  n = 0.027
FEATURE [App::DocumentObjectGroupPython] O_element094  label="O_element : 0.602"  # scripted group (container) (typed FeaturePython)
  n = 0.602
FEATURE [App::DocumentObjectGroupPython] Na_element019  label="Na_element : 0.102"  # scripted group (container) (typed FeaturePython)
  n = 0.001
FEATURE [App::DocumentObjectGroupPython] P_element011  label="P_element : 0.109"  # scripted group (container) (typed FeaturePython)
  n = 0.002
FEATURE [App::DocumentObjectGroupPython] S_element022  label="S_element : 0.023"  # scripted group (container) (typed FeaturePython)
  n = 0.003
FEATURE [App::DocumentObjectGroupPython] Cl_element027  label="Cl_element : 0.591"  # scripted group (container) (typed FeaturePython)
  n = 0.002
FEATURE [App::DocumentObjectGroupPython] K_element012  label="K_element : 0.018"  # scripted group (container) (typed FeaturePython)
  n = 0.002
FEATURE [App::DocumentObjectGroupPython] G4_TISSUE_SOFT_ICRP  # scripted group (container) (typed FeaturePython)
  Dunit = g/cm3
  Dvalue = 1.03
  Group = -> [H_element100,C_element110,N_element042,O_element094,Na_element019,P_element011,S_element022,Cl_element027,K_element012]
  conduct = 2
  density = 1
  expand = 3
  formula = G4_TISSUE_SOFT_ICRP
  name = G4_TISSUE_SOFT_ICRP
  specific = 4
FEATURE [App::DocumentObjectGroupPython] H_element101  label="H_element : 0.148"  # scripted group (container) (typed FeaturePython)
  n = 0.101
FEATURE [App::DocumentObjectGroupPython] C_element111  label="C_element : 0.111"  # scripted group (container) (typed FeaturePython)
  n = 0.111
FEATURE [App::DocumentObjectGroupPython] N_element043  label="N_element : 0.026"  # scripted group (container) (typed FeaturePython)
  n = 0.026
FEATURE [App::DocumentObjectGroupPython] O_element095  label="O_element : 0.762"  # scripted group (container) (typed FeaturePython)
  n = 0.762
FEATURE [App::DocumentObjectGroupPython] G4_TISSUE_SOFT_ICRU_4  label="G4_TISSUE_SOFT_ICRU-4"  # scripted group (container) (typed FeaturePython)
  Dunit = g/cm3
  Dvalue = 1
  Group = -> [H_element101,C_element111,N_element043,O_element095]
  conduct = 2
  density = 1
  expand = 3
  formula = G4_TISSUE_SOFT_ICRU-4
  name = G4_TISSUE_SOFT_ICRU-4
  specific = 4
FEATURE [App::DocumentObjectGroupPython] H_element102  label="H_element : 0.149"  # scripted group (container) (typed FeaturePython)
  n = 0.101869
FEATURE [App::DocumentObjectGroupPython] C_element112  label="C_element : 0.456"  # scripted group (container) (typed FeaturePython)
  n = 0.456179
FEATURE [App::DocumentObjectGroupPython] N_element044  label="N_element : 0.761"  # scripted group (container) (typed FeaturePython)
  n = 0.035172
FEATURE [App::DocumentObjectGroupPython] O_element096  label="O_element : 0.407"  # scripted group (container) (typed FeaturePython)
  n = 0.40678
FEATURE [App::DocumentObjectGroupPython] G4_TISSUE_METHANE  label="G4_TISSUE-METHANE"  # scripted group (container) (typed FeaturePython)
  Dunit = g/cm3
  Dvalue = 0.00106409
  Group = -> [H_element102,C_element112,N_element044,O_element096]
  conduct = 2
  density = 1
  expand = 3
  formula = G4_TISSUE-METHANE
  name = G4_TISSUE-METHANE
  specific = 4
FEATURE [App::DocumentObjectGroupPython] H_element103  label="H_element : 0.103"  # scripted group (container) (typed FeaturePython)
  n = 0.102672
FEATURE [App::DocumentObjectGroupPython] C_element113  label="C_element : 0.569"  # scripted group (container) (typed FeaturePython)
  n = 0.56894
FEATURE [App::DocumentObjectGroupPython] N_element045  label="N_element : 0.762"  # scripted group (container) (typed FeaturePython)
  n = 0.035022
FEATURE [App::DocumentObjectGroupPython] O_element097  label="O_element : 0.293"  # scripted group (container) (typed FeaturePython)
  n = 0.293366
FEATURE [App::DocumentObjectGroupPython] G4_TISSUE_PROPANE  label="G4_TISSUE-PROPANE"  # scripted group (container) (typed FeaturePython)
  Dunit = g/cm3
  Dvalue = 0.00182628
  Group = -> [H_element103,C_element113,N_element045,O_element097]
  conduct = 2
  density = 1
  expand = 3
  formula = G4_TISSUE-PROPANE
  name = G4_TISSUE-PROPANE
  specific = 4
FEATURE [App::DocumentObjectGroupPython] Ti_element003  label="Ti_element : 1"  # scripted group (container) (typed FeaturePython)
  n = 1
  ref = Ti_element
FEATURE [App::DocumentObjectGroupPython] O_element098  label="O_element : 052"  # scripted group (container) (typed FeaturePython)
  n = 2
  ref = O_element
FEATURE [App::DocumentObjectGroupPython] G4_TITANIUM_DIOXIDE  # scripted group (container) (typed FeaturePython)
  Dunit = g/cm3
  Dvalue = 4.26
  Group = -> [Ti_element003,O_element098]
  conduct = 2
  density = 1
  expand = 3
  formula = G4_TITANIUM_DIOXIDE
  name = G4_TITANIUM_DIOXIDE
  specific = 4
FEATURE [App::DocumentObjectGroupPython] C_element114  label="C_element : 061"  # scripted group (container) (typed FeaturePython)
  n = 7
  ref = C_element
FEATURE [App::DocumentObjectGroupPython] H_element104  label="H_element : 055"  # scripted group (container) (typed FeaturePython)
  n = 8
  ref = H_element
FEATURE [App::DocumentObjectGroupPython] G4_TOLUENE  # scripted group (container) (typed FeaturePython)
  Dunit = g/cm3
  Dvalue = 0.8669
  Group = -> [C_element114,H_element104]
  conduct = 2
  density = 1
  expand = 3
  formula = G4_TOLUENE
  name = G4_TOLUENE
  specific = 4
FEATURE [App::DocumentObjectGroupPython] C_element115  label="C_element : 062"  # scripted group (container) (typed FeaturePython)
  n = 2
  ref = C_element
FEATURE [App::DocumentObjectGroupPython] H_element105  label="H_element : 056"  # scripted group (container) (typed FeaturePython)
  n = 1
  ref = H_element
FEATURE [App::DocumentObjectGroupPython] Cl_element028  label="Cl_element : 014"  # scripted group (container) (typed FeaturePython)
  n = 3
  ref = Cl_element
FEATURE [App::DocumentObjectGroupPython] G4_TRICHLOROETHYLENE  # scripted group (container) (typed FeaturePython)
  Dunit = g/cm3
  Dvalue = 1.46
  Group = -> [C_element115,H_element105,Cl_element028]
  conduct = 2
  density = 1
  expand = 3
  formula = G4_TRICHLOROETHYLENE
  name = G4_TRICHLOROETHYLENE
  specific = 4
FEATURE [App::DocumentObjectGroupPython] C_element116  label="C_element : 063"  # scripted group (container) (typed FeaturePython)
  n = 6
  ref = C_element
FEATURE [App::DocumentObjectGroupPython] H_element106  label="H_element : 15"  # scripted group (container) (typed FeaturePython)
  n = 15
  ref = H_element
FEATURE [App::DocumentObjectGroupPython] O_element099  label="O_element : 053"  # scripted group (container) (typed FeaturePython)
  n = 4
  ref = O_element
FEATURE [App::DocumentObjectGroupPython] P_element012  label="P_element : 1"  # scripted group (container) (typed FeaturePython)
  n = 1
  ref = P_element
FEATURE [App::DocumentObjectGroupPython] G4_TRIETHYL_PHOSPHATE  # scripted group (container) (typed FeaturePython)
  Dunit = g/cm3
  Dvalue = 1.07
  Group = -> [C_element116,H_element106,O_element099,P_element012]
  conduct = 2
  density = 1
  expand = 3
  formula = G4_TRIETHYL_PHOSPHATE
  name = G4_TRIETHYL_PHOSPHATE
  specific = 4
FEATURE [App::DocumentObjectGroupPython] W_element003  label="W_element : 003"  # scripted group (container) (typed FeaturePython)
  n = 1
  ref = W_element
FEATURE [App::DocumentObjectGroupPython] F_element017  label="F_element : 6"  # scripted group (container) (typed FeaturePython)
  n = 6
  ref = F_element
FEATURE [App::DocumentObjectGroupPython] G4_TUNGSTEN_HEXAFLUORIDE  # scripted group (container) (typed FeaturePython)
  Dunit = g/cm3
  Dvalue = 2.4
  Group = -> [W_element003,F_element017]
  conduct = 2
  density = 1
  expand = 3
  formula = G4_TUNGSTEN_HEXAFLUORIDE
  name = G4_TUNGSTEN_HEXAFLUORIDE
  specific = 4
FEATURE [App::DocumentObjectGroupPython] U_element001  label="U_element : 1"  # scripted group (container) (typed FeaturePython)
  n = 1
  ref = U_element
FEATURE [App::DocumentObjectGroupPython] C_element117  label="C_element : 064"  # scripted group (container) (typed FeaturePython)
  n = 2
  ref = C_element
FEATURE [App::DocumentObjectGroupPython] G4_URANIUM_DICARBIDE  # scripted group (container) (typed FeaturePython)
  Dunit = g/cm3
  Dvalue = 11.28
  Group = -> [U_element001,C_element117]
  conduct = 2
  density = 1
  expand = 3
  formula = G4_URANIUM_DICARBIDE
  name = G4_URANIUM_DICARBIDE
  specific = 4
FEATURE [App::DocumentObjectGroupPython] U_element002  label="U_element : 002"  # scripted group (container) (typed FeaturePython)
  n = 1
  ref = U_element
FEATURE [App::DocumentObjectGroupPython] C_element118  label="C_element : 065"  # scripted group (container) (typed FeaturePython)
  n = 1
  ref = C_element
FEATURE [App::DocumentObjectGroupPython] G4_URANIUM_MONOCARBIDE  # scripted group (container) (typed FeaturePython)
  Dunit = g/cm3
  Dvalue = 13.63
  Group = -> [U_element002,C_element118]
  conduct = 2
  density = 1
  expand = 3
  formula = G4_URANIUM_MONOCARBIDE
  name = G4_URANIUM_MONOCARBIDE
  specific = 4
FEATURE [App::DocumentObjectGroupPython] U_element003  label="U_element : 003"  # scripted group (container) (typed FeaturePython)
  n = 1
  ref = U_element
FEATURE [App::DocumentObjectGroupPython] O_element100  label="O_element : 054"  # scripted group (container) (typed FeaturePython)
  n = 2
  ref = O_element
FEATURE [App::DocumentObjectGroupPython] G4_URANIUM_OXIDE  # scripted group (container) (typed FeaturePython)
  Dunit = g/cm3
  Dvalue = 10.96
  Group = -> [U_element003,O_element100]
  conduct = 2
  density = 1
  expand = 3
  formula = G4_URANIUM_OXIDE
  name = G4_URANIUM_OXIDE
  specific = 4
FEATURE [App::DocumentObjectGroupPython] C_element119  label="C_element : 066"  # scripted group (container) (typed FeaturePython)
  n = 1
  ref = C_element
FEATURE [App::DocumentObjectGroupPython] H_element107  label="H_element : 057"  # scripted group (container) (typed FeaturePython)
  n = 4
  ref = H_element
FEATURE [App::DocumentObjectGroupPython] N_element046  label="N_element : 019"  # scripted group (container) (typed FeaturePython)
  n = 2
  ref = N_element
FEATURE [App::DocumentObjectGroupPython] O_element101  label="O_element : 055"  # scripted group (container) (typed FeaturePython)
  n = 1
  ref = O_element
FEATURE [App::DocumentObjectGroupPython] G4_UREA  # scripted group (container) (typed FeaturePython)
  Dunit = g/cm3
  Dvalue = 1.323
  Group = -> [C_element119,H_element107,N_element046,O_element101]
  conduct = 2
  density = 1
  expand = 3
  formula = G4_UREA
  name = G4_UREA
  specific = 4
FEATURE [App::DocumentObjectGroupPython] C_element120  label="C_element : 067"  # scripted group (container) (typed FeaturePython)
  n = 5
  ref = C_element
FEATURE [App::DocumentObjectGroupPython] H_element108  label="H_element : 058"  # scripted group (container) (typed FeaturePython)
  n = 11
  ref = H_element
FEATURE [App::DocumentObjectGroupPython] N_element047  label="N_element : 020"  # scripted group (container) (typed FeaturePython)
  n = 1
  ref = N_element
FEATURE [App::DocumentObjectGroupPython] O_element102  label="O_element : 056"  # scripted group (container) (typed FeaturePython)
  n = 2
  ref = O_element
FEATURE [App::DocumentObjectGroupPython] G4_VALINE  # scripted group (container) (typed FeaturePython)
  Dunit = g/cm3
  Dvalue = 1.23
  Group = -> [C_element120,H_element108,N_element047,O_element102]
  conduct = 2
  density = 1
  expand = 3
  formula = G4_VALINE
  name = G4_VALINE
  specific = 4
FEATURE [App::DocumentObjectGroupPython] H_element109  label="H_element : 0.009"  # scripted group (container) (typed FeaturePython)
  n = 0.009417
FEATURE [App::DocumentObjectGroupPython] C_element121  label="C_element : 0.281"  # scripted group (container) (typed FeaturePython)
  n = 0.280555
FEATURE [App::DocumentObjectGroupPython] F_element018  label="F_element : 0.710"  # scripted group (container) (typed FeaturePython)
  n = 0.710028
FEATURE [App::DocumentObjectGroupPython] G4_VITON  # scripted group (container) (typed FeaturePython)
  Dunit = g/cm3
  Dvalue = 1.8
  Group = -> [H_element109,C_element121,F_element018]
  conduct = 2
  density = 1
  expand = 3
  formula = G4_VITON
  name = G4_VITON
  specific = 4
FEATURE [App::DocumentObjectGroupPython] H_element110  label="H_element : 059"  # scripted group (container) (typed FeaturePython)
  n = 2
  ref = H_element
FEATURE [App::DocumentObjectGroupPython] O_element103  label="O_element : 057"  # scripted group (container) (typed FeaturePython)
  n = 1
  ref = O_element
FEATURE [App::DocumentObjectGroupPython] G4_WATER  # scripted group (container) (typed FeaturePython)
  Dunit = g/cm3
  Dvalue = 1
  Group = -> [H_element110,O_element103]
  conduct = 2
  density = 1
  expand = 3
  formula = G4_WATER
  name = G4_WATER
  specific = 4
FEATURE [App::DocumentObjectGroupPython] H_element111  label="H_element : 060"  # scripted group (container) (typed FeaturePython)
  n = 2
  ref = H_element
FEATURE [App::DocumentObjectGroupPython] O_element104  label="O_element : 058"  # scripted group (container) (typed FeaturePython)
  n = 1
  ref = O_element
FEATURE [App::DocumentObjectGroupPython] G4_WATER_VAPOR  # scripted group (container) (typed FeaturePython)
  Dunit = g/cm3
  Dvalue = 0.000756182
  Group = -> [H_element111,O_element104]
  conduct = 2
  density = 1
  expand = 3
  formula = G4_WATER_VAPOR
  name = G4_WATER_VAPOR
  specific = 4
FEATURE [App::DocumentObjectGroupPython] C_element122  label="C_element : 068"  # scripted group (container) (typed FeaturePython)
  n = 8
  ref = C_element
FEATURE [App::DocumentObjectGroupPython] H_element112  label="H_element : 061"  # scripted group (container) (typed FeaturePython)
  n = 10
  ref = H_element
FEATURE [App::DocumentObjectGroupPython] G4_XYLENE  # scripted group (container) (typed FeaturePython)
  Dunit = g/cm3
  Dvalue = 0.87
  Group = -> [C_element122,H_element112]
  conduct = 2
  density = 1
  expand = 3
  formula = G4_XYLENE
  name = G4_XYLENE
  specific = 4
FEATURE [App::DocumentObjectGroupPython] C_element123  label="C_element : 069"  # scripted group (container) (typed FeaturePython)
  n = 1
  ref = C_element
FEATURE [App::DocumentObjectGroupPython] G4_GRAPHITE  # scripted group (container) (typed FeaturePython)
  Dunit = g/cm3
  Dvalue = 2.21
  Group = -> [C_element123]
  conduct = 2
  density = 1
  expand = 3
  formula = G4_GRAPHITE
  name = G4_GRAPHITE
  specific = 4
FEATURE [App::DocumentObjectGroupPython] NIST  # scripted group (container) (typed FeaturePython)
  Group = -> [G4_A_150_TISSUE,G4_ACETONE,G4_ACETYLENE,G4_ADENINE,G4_ADIPOSE_TISSUE_ICRP,G4_AIR,G4_ALANINE,G4_ALUMINUM_OXIDE,G4_AMBER,G4_AMMONIA,G4_ANILINE,G4_ANTHRACENE,G4_B_100_BONE,G4_BAKELITE,G4_BARIUM_FLUORIDE,G4_BARIUM_SULFATE,G4_BENZENE,G4_BERYLLIUM_OXIDE,G4_BGO,G4_BLOOD_ICRP,G4_BONE_COMPACT_ICRU,G4_BONE_CORTICAL_ICRP,G4_BORON_CARBIDE,G4_BORON_OXIDE,G4_BRAIN_ICRP,G4_BUTANE,G4_N_BUTYL_ALCOHOL,G4_C_552,+152 more]
FEATURE [App::DocumentObjectGroupPython] H_element113  label="H_element : 062"  # scripted group (container) (typed FeaturePython)
  n = 1
  ref = H_element
FEATURE [App::DocumentObjectGroupPython] G4_H  # scripted group (container) (typed FeaturePython)
  Dunit = g/cm3
  Dvalue = 8.3748e-05
  Group = -> [H_element113]
  conduct = 2
  density = 1
  expand = 3
  formula = H
  name = G4_H
  specific = 4
FEATURE [App::DocumentObjectGroupPython] He_element001  label="He_element : 1"  # scripted group (container) (typed FeaturePython)
  n = 1
  ref = He_element
FEATURE [App::DocumentObjectGroupPython] G4_He  # scripted group (container) (typed FeaturePython)
  Dunit = g/cm3
  Dvalue = 0.000166322
  Group = -> [He_element001]
  conduct = 2
  density = 1
  expand = 3
  formula = He
  name = G4_He
  specific = 4
FEATURE [App::DocumentObjectGroupPython] Li_element008  label="Li_element : 008"  # scripted group (container) (typed FeaturePython)
  n = 1
  ref = Li_element
FEATURE [App::DocumentObjectGroupPython] G4_Li  # scripted group (container) (typed FeaturePython)
  Dunit = g/cm3
  Dvalue = 0.534
  Group = -> [Li_element008]
  conduct = 2
  density = 1
  expand = 3
  formula = Li
  name = G4_Li
  specific = 4
FEATURE [App::DocumentObjectGroupPython] Be_element002  label="Be_element : 002"  # scripted group (container) (typed FeaturePython)
  n = 1
  ref = Be_element
FEATURE [App::DocumentObjectGroupPython] G4_Be  # scripted group (container) (typed FeaturePython)
  Dunit = g/cm3
  Dvalue = 1.848
  Group = -> [Be_element002]
  conduct = 2
  density = 1
  expand = 3
  formula = Be
  name = G4_Be
  specific = 4
FEATURE [App::DocumentObjectGroupPython] B_element007  label="B_element : 007"  # scripted group (container) (typed FeaturePython)
  n = 1
  ref = B_element
FEATURE [App::DocumentObjectGroupPython] G4_B  # scripted group (container) (typed FeaturePython)
  Dunit = g/cm3
  Dvalue = 2.37
  Group = -> [B_element007]
  conduct = 2
  density = 1
  expand = 3
  formula = B
  name = G4_B
  specific = 4
FEATURE [App::DocumentObjectGroupPython] C_element124  label="C_element : 070"  # scripted group (container) (typed FeaturePython)
  n = 1
  ref = C_element
FEATURE [App::DocumentObjectGroupPython] G4_C  # scripted group (container) (typed FeaturePython)
  Dunit = g/cm3
  Dvalue = 2
  Group = -> [C_element124]
  conduct = 2
  density = 1
  expand = 3
  formula = C
  name = G4_C
  specific = 4
FEATURE [App::DocumentObjectGroupPython] N_element048  label="N_element : 021"  # scripted group (container) (typed FeaturePython)
  n = 1
  ref = N_element
FEATURE [App::DocumentObjectGroupPython] G4_N  # scripted group (container) (typed FeaturePython)
  Dunit = g/cm3
  Dvalue = 0.0011652
  Group = -> [N_element048]
  conduct = 2
  density = 1
  expand = 3
  formula = N
  name = G4_N
  specific = 4
FEATURE [App::DocumentObjectGroupPython] O_element105  label="O_element : 059"  # scripted group (container) (typed FeaturePython)
  n = 1
  ref = O_element
FEATURE [App::DocumentObjectGroupPython] G4_O  # scripted group (container) (typed FeaturePython)
  Dunit = g/cm3
  Dvalue = 0.00133151
  Group = -> [O_element105]
  conduct = 2
  density = 1
  expand = 3
  formula = O
  name = G4_O
  specific = 4
FEATURE [App::DocumentObjectGroupPython] F_element019  label="F_element : 008"  # scripted group (container) (typed FeaturePython)
  n = 1
  ref = F_element
FEATURE [App::DocumentObjectGroupPython] G4_F  # scripted group (container) (typed FeaturePython)
  Dunit = g/cm3
  Dvalue = 0.00158029
  Group = -> [F_element019]
  conduct = 2
  density = 1
  expand = 3
  formula = F
  name = G4_F
  specific = 4
FEATURE [App::DocumentObjectGroupPython] Ne_element001  label="Ne_element : 1"  # scripted group (container) (typed FeaturePython)
  n = 1
  ref = Ne_element
FEATURE [App::DocumentObjectGroupPython] G4_Ne  # scripted group (container) (typed FeaturePython)
  Dunit = g/cm3
  Dvalue = 0.000838505
  Group = -> [Ne_element001]
  conduct = 2
  density = 1
  expand = 3
  formula = Ne
  name = G4_Ne
  specific = 4
FEATURE [App::DocumentObjectGroupPython] Na_element020  label="Na_element : 005"  # scripted group (container) (typed FeaturePython)
  n = 1
  ref = Na_element
FEATURE [App::DocumentObjectGroupPython] G4_Na  # scripted group (container) (typed FeaturePython)
  Dunit = g/cm3
  Dvalue = 0.971
  Group = -> [Na_element020]
  conduct = 2
  density = 1
  expand = 3
  formula = Na
  name = G4_Na
  specific = 4
FEATURE [App::DocumentObjectGroupPython] Mg_element011  label="Mg_element : 005"  # scripted group (container) (typed FeaturePython)
  n = 1
  ref = Mg_element
FEATURE [App::DocumentObjectGroupPython] G4_Mg  # scripted group (container) (typed FeaturePython)
  Dunit = g/cm3
  Dvalue = 1.74
  Group = -> [Mg_element011]
  conduct = 2
  density = 1
  expand = 3
  formula = Mg
  name = G4_Mg
  specific = 4
FEATURE [App::DocumentObjectGroupPython] Al_element004  label="Al_element : 1"  # scripted group (container) (typed FeaturePython)
  n = 1
  ref = Al_element
FEATURE [App::DocumentObjectGroupPython] G4_Al  # scripted group (container) (typed FeaturePython)
  Dunit = g/cm3
  Dvalue = 2.699
  Group = -> [Al_element004]
  conduct = 2
  density = 1
  expand = 3
  formula = Al
  name = G4_Al
  specific = 4
FEATURE [App::DocumentObjectGroupPython] Si_element007  label="Si_element : 002"  # scripted group (container) (typed FeaturePython)
  n = 1
  ref = Si_element
FEATURE [App::DocumentObjectGroupPython] G4_Si  # scripted group (container) (typed FeaturePython)
  Dunit = g/cm3
  Dvalue = 2.33
  Group = -> [Si_element007]
  conduct = 2
  density = 1
  expand = 3
  formula = Si
  name = G4_Si
  specific = 4
FEATURE [App::DocumentObjectGroupPython] P_element013  label="P_element : 002"  # scripted group (container) (typed FeaturePython)
  n = 1
  ref = P_element
FEATURE [App::DocumentObjectGroupPython] G4_P  # scripted group (container) (typed FeaturePython)
  Dunit = g/cm3
  Dvalue = 2.2
  Group = -> [P_element013]
  conduct = 2
  density = 1
  expand = 3
  formula = P
  name = G4_P
  specific = 4
FEATURE [App::DocumentObjectGroupPython] S_element023  label="S_element : 007"  # scripted group (container) (typed FeaturePython)
  n = 1
  ref = S_element
FEATURE [App::DocumentObjectGroupPython] G4_S  # scripted group (container) (typed FeaturePython)
  Dunit = g/cm3
  Dvalue = 2
  Group = -> [S_element023]
  conduct = 2
  density = 1
  expand = 3
  formula = S
  name = G4_S
  specific = 4
FEATURE [App::DocumentObjectGroupPython] Cl_element029  label="Cl_element : 015"  # scripted group (container) (typed FeaturePython)
  n = 1
  ref = Cl_element
FEATURE [App::DocumentObjectGroupPython] G4_Cl  # scripted group (container) (typed FeaturePython)
  Dunit = g/cm3
  Dvalue = 0.00299473
  Group = -> [Cl_element029]
  conduct = 2
  density = 1
  expand = 3
  formula = Cl
  name = G4_Cl
  specific = 4
FEATURE [App::DocumentObjectGroupPython] Ar_element002  label="Ar_element : 1"  # scripted group (container) (typed FeaturePython)
  n = 1
  ref = Ar_element
FEATURE [App::DocumentObjectGroupPython] G4_Ar  # scripted group (container) (typed FeaturePython)
  Dunit = g/cm3
  Dvalue = 0.00166201
  Group = -> [Ar_element002]
  conduct = 2
  density = 1
  expand = 3
  formula = Ar
  name = G4_Ar
  specific = 4
FEATURE [App::DocumentObjectGroupPython] K_element013  label="K_element : 003"  # scripted group (container) (typed FeaturePython)
  n = 1
  ref = K_element
FEATURE [App::DocumentObjectGroupPython] G4_K  # scripted group (container) (typed FeaturePython)
  Dunit = g/cm3
  Dvalue = 0.862
  Group = -> [K_element013]
  conduct = 2
  density = 1
  expand = 3
  formula = K
  name = G4_K
  specific = 4
FEATURE [App::DocumentObjectGroupPython] Ca_element014  label="Ca_element : 007"  # scripted group (container) (typed FeaturePython)
  n = 1
  ref = Ca_element
FEATURE [App::DocumentObjectGroupPython] G4_Ca  # scripted group (container) (typed FeaturePython)
  Dunit = g/cm3
  Dvalue = 1.55
  Group = -> [Ca_element014]
  conduct = 2
  density = 1
  expand = 3
  formula = Ca
  name = G4_Ca
  specific = 4
FEATURE [App::DocumentObjectGroupPython] Sc_element001  label="Sc_element : 1"  # scripted group (container) (typed FeaturePython)
  n = 1
  ref = Sc_element
FEATURE [App::DocumentObjectGroupPython] G4_Sc  # scripted group (container) (typed FeaturePython)
  Dunit = g/cm3
  Dvalue = 2.989
  Group = -> [Sc_element001]
  conduct = 2
  density = 1
  expand = 3
  formula = Sc
  name = G4_Sc
  specific = 4
FEATURE [App::DocumentObjectGroupPython] Ti_element004  label="Ti_element : 002"  # scripted group (container) (typed FeaturePython)
  n = 1
  ref = Ti_element
FEATURE [App::DocumentObjectGroupPython] G4_Ti  # scripted group (container) (typed FeaturePython)
  Dunit = g/cm3
  Dvalue = 4.54
  Group = -> [Ti_element004]
  conduct = 2
  density = 1
  expand = 3
  formula = Ti
  name = G4_Ti
  specific = 4
FEATURE [App::DocumentObjectGroupPython] V_element001  label="V_element : 1"  # scripted group (container) (typed FeaturePython)
  n = 1
  ref = V_element
FEATURE [App::DocumentObjectGroupPython] G4_V  # scripted group (container) (typed FeaturePython)
  Dunit = g/cm3
  Dvalue = 6.11
  Group = -> [V_element001]
  conduct = 2
  density = 1
  expand = 3
  formula = V
  name = G4_V
  specific = 4
FEATURE [App::DocumentObjectGroupPython] Cr_element001  label="Cr_element : 1"  # scripted group (container) (typed FeaturePython)
  n = 1
  ref = Cr_element
FEATURE [App::DocumentObjectGroupPython] G4_Cr  # scripted group (container) (typed FeaturePython)
  Dunit = g/cm3
  Dvalue = 7.18
  Group = -> [Cr_element001]
  conduct = 2
  density = 1
  expand = 3
  formula = Cr
  name = G4_Cr
  specific = 4
FEATURE [App::DocumentObjectGroupPython] Mn_element001  label="Mn_element : 1"  # scripted group (container) (typed FeaturePython)
  n = 1
  ref = Mn_element
FEATURE [App::DocumentObjectGroupPython] G4_Mn  # scripted group (container) (typed FeaturePython)
  Dunit = g/cm3
  Dvalue = 7.44
  Group = -> [Mn_element001]
  conduct = 2
  density = 1
  expand = 3
  formula = Mn
  name = G4_Mn
  specific = 4
FEATURE [App::DocumentObjectGroupPython] Fe_element007  label="Fe_element : 004"  # scripted group (container) (typed FeaturePython)
  n = 1
  ref = Fe_element
FEATURE [App::DocumentObjectGroupPython] G4_Fe  # scripted group (container) (typed FeaturePython)
  Dunit = g/cm3
  Dvalue = 7.874
  Group = -> [Fe_element007]
  conduct = 2
  density = 1
  expand = 3
  formula = Fe
  name = G4_Fe
  specific = 4
FEATURE [App::DocumentObjectGroupPython] Co_element001  label="Co_element : 1"  # scripted group (container) (typed FeaturePython)
  n = 1
  ref = Co_element
FEATURE [App::DocumentObjectGroupPython] G4_Co  # scripted group (container) (typed FeaturePython)
  Dunit = g/cm3
  Dvalue = 8.9
  Group = -> [Co_element001]
  conduct = 2
  density = 1
  expand = 3
  formula = Co
  name = G4_Co
  specific = 4
FEATURE [App::DocumentObjectGroupPython] Ni_element001  label="Ni_element : 1"  # scripted group (container) (typed FeaturePython)
  n = 1
  ref = Ni_element
FEATURE [App::DocumentObjectGroupPython] G4_Ni  # scripted group (container) (typed FeaturePython)
  Dunit = g/cm3
  Dvalue = 8.902
  Group = -> [Ni_element001]
  conduct = 2
  density = 1
  expand = 3
  formula = Ni
  name = G4_Ni
  specific = 4
FEATURE [App::DocumentObjectGroupPython] Cu_element001  label="Cu_element : 1"  # scripted group (container) (typed FeaturePython)
  n = 1
  ref = Cu_element
FEATURE [App::DocumentObjectGroupPython] G4_Cu  # scripted group (container) (typed FeaturePython)
  Dunit = g/cm3
  Dvalue = 8.96
  Group = -> [Cu_element001]
  conduct = 2
  density = 1
  expand = 3
  formula = Cu
  name = G4_Cu
  specific = 4
FEATURE [App::DocumentObjectGroupPython] Zn_element001  label="Zn_element : 1"  # scripted group (container) (typed FeaturePython)
  n = 1
  ref = Zn_element
FEATURE [App::DocumentObjectGroupPython] G4_Zn  # scripted group (container) (typed FeaturePython)
  Dunit = g/cm3
  Dvalue = 7.133
  Group = -> [Zn_element001]
  conduct = 2
  density = 1
  expand = 3
  formula = Zn
  name = G4_Zn
  specific = 4
FEATURE [App::DocumentObjectGroupPython] Ga_element002  label="Ga_element : 002"  # scripted group (container) (typed FeaturePython)
  n = 1
  ref = Ga_element
FEATURE [App::DocumentObjectGroupPython] G4_Ga  # scripted group (container) (typed FeaturePython)
  Dunit = g/cm3
  Dvalue = 5.904
  Group = -> [Ga_element002]
  conduct = 2
  density = 1
  expand = 3
  formula = Ga
  name = G4_Ga
  specific = 4
FEATURE [App::DocumentObjectGroupPython] Ge_element002  label="Ge_element : 1"  # scripted group (container) (typed FeaturePython)
  n = 1
  ref = Ge_element
FEATURE [App::DocumentObjectGroupPython] G4_Ge  # scripted group (container) (typed FeaturePython)
  Dunit = g/cm3
  Dvalue = 5.323
  Group = -> [Ge_element002]
  conduct = 2
  density = 1
  expand = 3
  formula = Ge
  name = G4_Ge
  specific = 4
FEATURE [App::DocumentObjectGroupPython] As_element003  label="As_element : 002"  # scripted group (container) (typed FeaturePython)
  n = 1
  ref = As_element
FEATURE [App::DocumentObjectGroupPython] G4_As  # scripted group (container) (typed FeaturePython)
  Dunit = g/cm3
  Dvalue = 5.73
  Group = -> [As_element003]
  conduct = 2
  density = 1
  expand = 3
  formula = As
  name = G4_As
  specific = 4
FEATURE [App::DocumentObjectGroupPython] Se_element001  label="Se_element : 1"  # scripted group (container) (typed FeaturePython)
  n = 1
  ref = Se_element
FEATURE [App::DocumentObjectGroupPython] G4_Se  # scripted group (container) (typed FeaturePython)
  Dunit = g/cm3
  Dvalue = 4.5
  Group = -> [Se_element001]
  conduct = 2
  density = 1
  expand = 3
  formula = Se
  name = G4_Se
  specific = 4
FEATURE [App::DocumentObjectGroupPython] Br_element007  label="Br_element : 004"  # scripted group (container) (typed FeaturePython)
  n = 1
  ref = Br_element
FEATURE [App::DocumentObjectGroupPython] G4_Br  # scripted group (container) (typed FeaturePython)
  Dunit = g/cm3
  Dvalue = 0.0070721
  Group = -> [Br_element007]
  conduct = 2
  density = 1
  expand = 3
  formula = Br
  name = G4_Br
  specific = 4
FEATURE [App::DocumentObjectGroupPython] Kr_element001  label="Kr_element : 1"  # scripted group (container) (typed FeaturePython)
  n = 1
  ref = Kr_element
FEATURE [App::DocumentObjectGroupPython] G4_Kr  # scripted group (container) (typed FeaturePython)
  Dunit = g/cm3
  Dvalue = 0.00347832
  Group = -> [Kr_element001]
  conduct = 2
  density = 1
  expand = 3
  formula = Kr
  name = G4_Kr
  specific = 4
FEATURE [App::DocumentObjectGroupPython] Rb_element001  label="Rb_element : 1"  # scripted group (container) (typed FeaturePython)
  n = 1
  ref = Rb_element
FEATURE [App::DocumentObjectGroupPython] G4_Rb  # scripted group (container) (typed FeaturePython)
  Dunit = g/cm3
  Dvalue = 1.532
  Group = -> [Rb_element001]
  conduct = 2
  density = 1
  expand = 3
  formula = Rb
  name = G4_Rb
  specific = 4
FEATURE [App::DocumentObjectGroupPython] Sr_element001  label="Sr_element : 1"  # scripted group (container) (typed FeaturePython)
  n = 1
  ref = Sr_element
FEATURE [App::DocumentObjectGroupPython] G4_Sr  # scripted group (container) (typed FeaturePython)
  Dunit = g/cm3
  Dvalue = 2.54
  Group = -> [Sr_element001]
  conduct = 2
  density = 1
  expand = 3
  formula = Sr
  name = G4_Sr
  specific = 4
FEATURE [App::DocumentObjectGroupPython] Y_element001  label="Y_element : 1"  # scripted group (container) (typed FeaturePython)
  n = 1
  ref = Y_element
FEATURE [App::DocumentObjectGroupPython] G4_Y  # scripted group (container) (typed FeaturePython)
  Dunit = g/cm3
  Dvalue = 4.469
  Group = -> [Y_element001]
  conduct = 2
  density = 1
  expand = 3
  formula = Y
  name = G4_Y
  specific = 4
FEATURE [App::DocumentObjectGroupPython] Zr_element001  label="Zr_element : 1"  # scripted group (container) (typed FeaturePython)
  n = 1
  ref = Zr_element
FEATURE [App::DocumentObjectGroupPython] G4_Zr  # scripted group (container) (typed FeaturePython)
  Dunit = g/cm3
  Dvalue = 6.506
  Group = -> [Zr_element001]
  conduct = 2
  density = 1
  expand = 3
  formula = Zr
  name = G4_Zr
  specific = 4
FEATURE [App::DocumentObjectGroupPython] Nb_element001  label="Nb_element : 1"  # scripted group (container) (typed FeaturePython)
  n = 1
  ref = Nb_element
FEATURE [App::DocumentObjectGroupPython] G4_Nb  # scripted group (container) (typed FeaturePython)
  Dunit = g/cm3
  Dvalue = 8.57
  Group = -> [Nb_element001]
  conduct = 2
  density = 1
  expand = 3
  formula = Nb
  name = G4_Nb
  specific = 4
FEATURE [App::DocumentObjectGroupPython] Mo_element001  label="Mo_element : 1"  # scripted group (container) (typed FeaturePython)
  n = 1
  ref = Mo_element
FEATURE [App::DocumentObjectGroupPython] G4_Mo  # scripted group (container) (typed FeaturePython)
  Dunit = g/cm3
  Dvalue = 10.22
  Group = -> [Mo_element001]
  conduct = 2
  density = 1
  expand = 3
  formula = Mo
  name = G4_Mo
  specific = 4
FEATURE [App::DocumentObjectGroupPython] Tc_element001  label="Tc_element : 1"  # scripted group (container) (typed FeaturePython)
  n = 1
  ref = Tc_element
FEATURE [App::DocumentObjectGroupPython] G4_Tc  # scripted group (container) (typed FeaturePython)
  Dunit = g/cm3
  Dvalue = 11.5
  Group = -> [Tc_element001]
  conduct = 2
  density = 1
  expand = 3
  formula = Tc
  name = G4_Tc
  specific = 4
FEATURE [App::DocumentObjectGroupPython] Ru_element001  label="Ru_element : 1"  # scripted group (container) (typed FeaturePython)
  n = 1
  ref = Ru_element
FEATURE [App::DocumentObjectGroupPython] G4_Ru  # scripted group (container) (typed FeaturePython)
  Dunit = g/cm3
  Dvalue = 12.41
  Group = -> [Ru_element001]
  conduct = 2
  density = 1
  expand = 3
  formula = Ru
  name = G4_Ru
  specific = 4
FEATURE [App::DocumentObjectGroupPython] Rh_element001  label="Rh_element : 1"  # scripted group (container) (typed FeaturePython)
  n = 1
  ref = Rh_element
FEATURE [App::DocumentObjectGroupPython] G4_Rh  # scripted group (container) (typed FeaturePython)
  Dunit = g/cm3
  Dvalue = 12.41
  Group = -> [Rh_element001]
  conduct = 2
  density = 1
  expand = 3
  formula = Rh
  name = G4_Rh
  specific = 4
FEATURE [App::DocumentObjectGroupPython] Pd_element001  label="Pd_element : 1"  # scripted group (container) (typed FeaturePython)
  n = 1
  ref = Pd_element
FEATURE [App::DocumentObjectGroupPython] G4_Pd  # scripted group (container) (typed FeaturePython)
  Dunit = g/cm3
  Dvalue = 12.02
  Group = -> [Pd_element001]
  conduct = 2
  density = 1
  expand = 3
  formula = Pd
  name = G4_Pd
  specific = 4
FEATURE [App::DocumentObjectGroupPython] Ag_element006  label="Ag_element : 004"  # scripted group (container) (typed FeaturePython)
  n = 1
  ref = Ag_element
FEATURE [App::DocumentObjectGroupPython] G4_Ag  # scripted group (container) (typed FeaturePython)
  Dunit = g/cm3
  Dvalue = 10.5
  Group = -> [Ag_element006]
  conduct = 2
  density = 1
  expand = 3
  formula = Ag
  name = G4_Ag
  specific = 4
FEATURE [App::DocumentObjectGroupPython] Cd_element003  label="Cd_element : 003"  # scripted group (container) (typed FeaturePython)
  n = 1
  ref = Cd_element
FEATURE [App::DocumentObjectGroupPython] G4_Cd  # scripted group (container) (typed FeaturePython)
  Dunit = g/cm3
  Dvalue = 8.65
  Group = -> [Cd_element003]
  conduct = 2
  density = 1
  expand = 3
  formula = Cd
  name = G4_Cd
  specific = 4
FEATURE [App::DocumentObjectGroupPython] In_element001  label="In_element : 1"  # scripted group (container) (typed FeaturePython)
  n = 1
  ref = In_element
FEATURE [App::DocumentObjectGroupPython] G4_In  # scripted group (container) (typed FeaturePython)
  Dunit = g/cm3
  Dvalue = 7.31
  Group = -> [In_element001]
  conduct = 2
  density = 1
  expand = 3
  formula = In
  name = G4_In
  specific = 4
FEATURE [App::DocumentObjectGroupPython] Sn_element001  label="Sn_element : 1"  # scripted group (container) (typed FeaturePython)
  n = 1
  ref = Sn_element
FEATURE [App::DocumentObjectGroupPython] G4_Sn  # scripted group (container) (typed FeaturePython)
  Dunit = g/cm3
  Dvalue = 7.31
  Group = -> [Sn_element001]
  conduct = 2
  density = 1
  expand = 3
  formula = Sn
  name = G4_Sn
  specific = 4
FEATURE [App::DocumentObjectGroupPython] Sb_element001  label="Sb_element : 1"  # scripted group (container) (typed FeaturePython)
  n = 1
  ref = Sb_element
FEATURE [App::DocumentObjectGroupPython] G4_Sb  # scripted group (container) (typed FeaturePython)
  Dunit = g/cm3
  Dvalue = 6.691
  Group = -> [Sb_element001]
  conduct = 2
  density = 1
  expand = 3
  formula = Sb
  name = G4_Sb
  specific = 4
FEATURE [App::DocumentObjectGroupPython] Te_element002  label="Te_element : 002"  # scripted group (container) (typed FeaturePython)
  n = 1
  ref = Te_element
FEATURE [App::DocumentObjectGroupPython] G4_Te  # scripted group (container) (typed FeaturePython)
  Dunit = g/cm3
  Dvalue = 6.24
  Group = -> [Te_element002]
  conduct = 2
  density = 1
  expand = 3
  formula = Te
  name = G4_Te
  specific = 4
FEATURE [App::DocumentObjectGroupPython] I_element010  label="I_element : 006"  # scripted group (container) (typed FeaturePython)
  n = 1
  ref = I_element
FEATURE [App::DocumentObjectGroupPython] G4_I  # scripted group (container) (typed FeaturePython)
  Dunit = g/cm3
  Dvalue = 4.93
  Group = -> [I_element010]
  conduct = 2
  density = 1
  expand = 3
  formula = I
  name = G4_I
  specific = 4
FEATURE [App::DocumentObjectGroupPython] Xe_element001  label="Xe_element : 1"  # scripted group (container) (typed FeaturePython)
  n = 1
  ref = Xe_element
FEATURE [App::DocumentObjectGroupPython] G4_Xe  # scripted group (container) (typed FeaturePython)
  Dunit = g/cm3
  Dvalue = 0.00548536
  Group = -> [Xe_element001]
  conduct = 2
  density = 1
  expand = 3
  formula = Xe
  name = G4_Xe
  specific = 4
FEATURE [App::DocumentObjectGroupPython] Cs_element003  label="Cs_element : 003"  # scripted group (container) (typed FeaturePython)
  n = 1
  ref = Cs_element
FEATURE [App::DocumentObjectGroupPython] G4_Cs  # scripted group (container) (typed FeaturePython)
  Dunit = g/cm3
  Dvalue = 1.873
  Group = -> [Cs_element003]
  conduct = 2
  density = 1
  expand = 3
  formula = Cs
  name = G4_Cs
  specific = 4
FEATURE [App::DocumentObjectGroupPython] Ba_element003  label="Ba_element : 003"  # scripted group (container) (typed FeaturePython)
  n = 1
  ref = Ba_element
FEATURE [App::DocumentObjectGroupPython] G4_Ba  # scripted group (container) (typed FeaturePython)
  Dunit = g/cm3
  Dvalue = 3.5
  Group = -> [Ba_element003]
  conduct = 2
  density = 1
  expand = 3
  formula = Ba
  name = G4_Ba
  specific = 4
FEATURE [App::DocumentObjectGroupPython] La_element003  label="La_element : 003"  # scripted group (container) (typed FeaturePython)
  n = 1
  ref = La_element
FEATURE [App::DocumentObjectGroupPython] G4_La  # scripted group (container) (typed FeaturePython)
  Dunit = g/cm3
  Dvalue = 6.154
  Group = -> [La_element003]
  conduct = 2
  density = 1
  expand = 3
  formula = La
  name = G4_La
  specific = 4
FEATURE [App::DocumentObjectGroupPython] Ce_element002  label="Ce_element : 1"  # scripted group (container) (typed FeaturePython)
  n = 1
  ref = Ce_element
FEATURE [App::DocumentObjectGroupPython] G4_Ce  # scripted group (container) (typed FeaturePython)
  Dunit = g/cm3
  Dvalue = 6.657
  Group = -> [Ce_element002]
  conduct = 2
  density = 1
  expand = 3
  formula = Ce
  name = G4_Ce
  specific = 4
FEATURE [App::DocumentObjectGroupPython] Pr_element001  label="Pr_element : 1"  # scripted group (container) (typed FeaturePython)
  n = 1
  ref = Pr_element
FEATURE [App::DocumentObjectGroupPython] G4_Pr  # scripted group (container) (typed FeaturePython)
  Dunit = g/cm3
  Dvalue = 6.71
  Group = -> [Pr_element001]
  conduct = 2
  density = 1
  expand = 3
  formula = Pr
  name = G4_Pr
  specific = 4
FEATURE [App::DocumentObjectGroupPython] Nd_element001  label="Nd_element : 1"  # scripted group (container) (typed FeaturePython)
  n = 1
  ref = Nd_element
FEATURE [App::DocumentObjectGroupPython] G4_Nd  # scripted group (container) (typed FeaturePython)
  Dunit = g/cm3
  Dvalue = 6.9
  Group = -> [Nd_element001]
  conduct = 2
  density = 1
  expand = 3
  formula = Nd
  name = G4_Nd
  specific = 4
FEATURE [App::DocumentObjectGroupPython] Pm_element001  label="Pm_element : 1"  # scripted group (container) (typed FeaturePython)
  n = 1
  ref = Pm_element
FEATURE [App::DocumentObjectGroupPython] G4_Pm  # scripted group (container) (typed FeaturePython)
  Dunit = g/cm3
  Dvalue = 7.22
  Group = -> [Pm_element001]
  conduct = 2
  density = 1
  expand = 3
  formula = Pm
  name = G4_Pm
  specific = 4
FEATURE [App::DocumentObjectGroupPython] Sm_element001  label="Sm_element : 1"  # scripted group (container) (typed FeaturePython)
  n = 1
  ref = Sm_element
FEATURE [App::DocumentObjectGroupPython] G4_Sm  # scripted group (container) (typed FeaturePython)
  Dunit = g/cm3
  Dvalue = 7.46
  Group = -> [Sm_element001]
  conduct = 2
  density = 1
  expand = 3
  formula = Sm
  name = G4_Sm
  specific = 4
FEATURE [App::DocumentObjectGroupPython] Eu_element001  label="Eu_element : 1"  # scripted group (container) (typed FeaturePython)
  n = 1
  ref = Eu_element
FEATURE [App::DocumentObjectGroupPython] G4_Eu  # scripted group (container) (typed FeaturePython)
  Dunit = g/cm3
  Dvalue = 5.243
  Group = -> [Eu_element001]
  conduct = 2
  density = 1
  expand = 3
  formula = Eu
  name = G4_Eu
  specific = 4
FEATURE [App::DocumentObjectGroupPython] Gd_element002  label="Gd_element : 1"  # scripted group (container) (typed FeaturePython)
  n = 1
  ref = Gd_element
FEATURE [App::DocumentObjectGroupPython] G4_Gd  # scripted group (container) (typed FeaturePython)
  Dunit = g/cm3
  Dvalue = 7.9004
  Group = -> [Gd_element002]
  conduct = 2
  density = 1
  expand = 3
  formula = Gd
  name = G4_Gd
  specific = 4
FEATURE [App::DocumentObjectGroupPython] Tb_element001  label="Tb_element : 1"  # scripted group (container) (typed FeaturePython)
  n = 1
  ref = Tb_element
FEATURE [App::DocumentObjectGroupPython] G4_Tb  # scripted group (container) (typed FeaturePython)
  Dunit = g/cm3
  Dvalue = 8.229
  Group = -> [Tb_element001]
  conduct = 2
  density = 1
  expand = 3
  formula = Tb
  name = G4_Tb
  specific = 4
FEATURE [App::DocumentObjectGroupPython] Dy_element001  label="Dy_element : 1"  # scripted group (container) (typed FeaturePython)
  n = 1
  ref = Dy_element
FEATURE [App::DocumentObjectGroupPython] G4_Dy  # scripted group (container) (typed FeaturePython)
  Dunit = g/cm3
  Dvalue = 8.55
  Group = -> [Dy_element001]
  conduct = 2
  density = 1
  expand = 3
  formula = Dy
  name = G4_Dy
  specific = 4
FEATURE [App::DocumentObjectGroupPython] Ho_element001  label="Ho_element : 1"  # scripted group (container) (typed FeaturePython)
  n = 1
  ref = Ho_element
FEATURE [App::DocumentObjectGroupPython] G4_Ho  # scripted group (container) (typed FeaturePython)
  Dunit = g/cm3
  Dvalue = 8.795
  Group = -> [Ho_element001]
  conduct = 2
  density = 1
  expand = 3
  formula = Ho
  name = G4_Ho
  specific = 4
FEATURE [App::DocumentObjectGroupPython] Er_element001  label="Er_element : 1"  # scripted group (container) (typed FeaturePython)
  n = 1
  ref = Er_element
FEATURE [App::DocumentObjectGroupPython] G4_Er  # scripted group (container) (typed FeaturePython)
  Dunit = g/cm3
  Dvalue = 9.066
  Group = -> [Er_element001]
  conduct = 2
  density = 1
  expand = 3
  formula = Er
  name = G4_Er
  specific = 4
FEATURE [App::DocumentObjectGroupPython] Tm_element001  label="Tm_element : 1"  # scripted group (container) (typed FeaturePython)
  n = 1
  ref = Tm_element
FEATURE [App::DocumentObjectGroupPython] G4_Tm  # scripted group (container) (typed FeaturePython)
  Dunit = g/cm3
  Dvalue = 9.321
  Group = -> [Tm_element001]
  conduct = 2
  density = 1
  expand = 3
  formula = Tm
  name = G4_Tm
  specific = 4
FEATURE [App::DocumentObjectGroupPython] Yb_element001  label="Yb_element : 1"  # scripted group (container) (typed FeaturePython)
  n = 1
  ref = Yb_element
FEATURE [App::DocumentObjectGroupPython] G4_Yb  # scripted group (container) (typed FeaturePython)
  Dunit = g/cm3
  Dvalue = 6.73
  Group = -> [Yb_element001]
  conduct = 2
  density = 1
  expand = 3
  formula = Yb
  name = G4_Yb
  specific = 4
FEATURE [App::DocumentObjectGroupPython] Lu_element001  label="Lu_element : 1"  # scripted group (container) (typed FeaturePython)
  n = 1
  ref = Lu_element
FEATURE [App::DocumentObjectGroupPython] G4_Lu  # scripted group (container) (typed FeaturePython)
  Dunit = g/cm3
  Dvalue = 9.84
  Group = -> [Lu_element001]
  conduct = 2
  density = 1
  expand = 3
  formula = Lu
  name = G4_Lu
  specific = 4
FEATURE [App::DocumentObjectGroupPython] Hf_element001  label="Hf_element : 1"  # scripted group (container) (typed FeaturePython)
  n = 1
  ref = Hf_element
FEATURE [App::DocumentObjectGroupPython] G4_Hf  # scripted group (container) (typed FeaturePython)
  Dunit = g/cm3
  Dvalue = 13.31
  Group = -> [Hf_element001]
  conduct = 2
  density = 1
  expand = 3
  formula = Hf
  name = G4_Hf
  specific = 4
FEATURE [App::DocumentObjectGroupPython] Ta_element001  label="Ta_element : 1"  # scripted group (container) (typed FeaturePython)
  n = 1
  ref = Ta_element
FEATURE [App::DocumentObjectGroupPython] G4_Ta  # scripted group (container) (typed FeaturePython)
  Dunit = g/cm3
  Dvalue = 16.654
  Group = -> [Ta_element001]
  conduct = 2
  density = 1
  expand = 3
  formula = Ta
  name = G4_Ta
  specific = 4
FEATURE [App::DocumentObjectGroupPython] W_element004  label="W_element : 004"  # scripted group (container) (typed FeaturePython)
  n = 1
  ref = W_element
FEATURE [App::DocumentObjectGroupPython] G4_W  # scripted group (container) (typed FeaturePython)
  Dunit = g/cm3
  Dvalue = 19.3
  Group = -> [W_element004]
  conduct = 2
  density = 1
  expand = 3
  formula = W
  name = G4_W
  specific = 4
FEATURE [App::DocumentObjectGroupPython] Re_element001  label="Re_element : 1"  # scripted group (container) (typed FeaturePython)
  n = 1
  ref = Re_element
FEATURE [App::DocumentObjectGroupPython] G4_Re  # scripted group (container) (typed FeaturePython)
  Dunit = g/cm3
  Dvalue = 21.02
  Group = -> [Re_element001]
  conduct = 2
  density = 1
  expand = 3
  formula = Re
  name = G4_Re
  specific = 4
FEATURE [App::DocumentObjectGroupPython] Os_element001  label="Os_element : 1"  # scripted group (container) (typed FeaturePython)
  n = 1
  ref = Os_element
FEATURE [App::DocumentObjectGroupPython] G4_Os  # scripted group (container) (typed FeaturePython)
  Dunit = g/cm3
  Dvalue = 22.57
  Group = -> [Os_element001]
  conduct = 2
  density = 1
  expand = 3
  formula = Os
  name = G4_Os
  specific = 4
FEATURE [App::DocumentObjectGroupPython] Ir_element001  label="Ir_element : 1"  # scripted group (container) (typed FeaturePython)
  n = 1
  ref = Ir_element
FEATURE [App::DocumentObjectGroupPython] G4_Ir  # scripted group (container) (typed FeaturePython)
  Dunit = g/cm3
  Dvalue = 22.42
  Group = -> [Ir_element001]
  conduct = 2
  density = 1
  expand = 3
  formula = Ir
  name = G4_Ir
  specific = 4
FEATURE [App::DocumentObjectGroupPython] Pt_element001  label="Pt_element : 1"  # scripted group (container) (typed FeaturePython)
  n = 1
  ref = Pt_element
FEATURE [App::DocumentObjectGroupPython] G4_Pt  # scripted group (container) (typed FeaturePython)
  Dunit = g/cm3
  Dvalue = 21.45
  Group = -> [Pt_element001]
  conduct = 2
  density = 1
  expand = 3
  formula = Pt
  name = G4_Pt
  specific = 4
FEATURE [App::DocumentObjectGroupPython] Au_element001  label="Au_element : 1"  # scripted group (container) (typed FeaturePython)
  n = 1
  ref = Au_element
FEATURE [App::DocumentObjectGroupPython] G4_Au  # scripted group (container) (typed FeaturePython)
  Dunit = g/cm3
  Dvalue = 19.32
  Group = -> [Au_element001]
  conduct = 2
  density = 1
  expand = 3
  formula = Au
  name = G4_Au
  specific = 4
FEATURE [App::DocumentObjectGroupPython] Hg_element002  label="Hg_element : 002"  # scripted group (container) (typed FeaturePython)
  n = 1
  ref = Hg_element
FEATURE [App::DocumentObjectGroupPython] G4_Hg  # scripted group (container) (typed FeaturePython)
  Dunit = g/cm3
  Dvalue = 13.546
  Group = -> [Hg_element002]
  conduct = 2
  density = 1
  expand = 3
  formula = Hg
  name = G4_Hg
  specific = 4
FEATURE [App::DocumentObjectGroupPython] Tl_element002  label="Tl_element : 002"  # scripted group (container) (typed FeaturePython)
  n = 1
  ref = Tl_element
FEATURE [App::DocumentObjectGroupPython] G4_Tl  # scripted group (container) (typed FeaturePython)
  Dunit = g/cm3
  Dvalue = 11.72
  Group = -> [Tl_element002]
  conduct = 2
  density = 1
  expand = 3
  formula = Tl
  name = G4_Tl
  specific = 4
FEATURE [App::DocumentObjectGroupPython] Pb_element003  label="Pb_element : 1"  # scripted group (container) (typed FeaturePython)
  n = 1
  ref = Pb_element
FEATURE [App::DocumentObjectGroupPython] G4_Pb  # scripted group (container) (typed FeaturePython)
  Dunit = g/cm3
  Dvalue = 11.35
  Group = -> [Pb_element003]
  conduct = 2
  density = 1
  expand = 3
  formula = Pb
  name = G4_Pb
  specific = 4
FEATURE [App::DocumentObjectGroupPython] Bi_element002  label="Bi_element : 1"  # scripted group (container) (typed FeaturePython)
  n = 1
  ref = Bi_element
FEATURE [App::DocumentObjectGroupPython] G4_Bi  # scripted group (container) (typed FeaturePython)
  Dunit = g/cm3
  Dvalue = 9.747
  Group = -> [Bi_element002]
  conduct = 2
  density = 1
  expand = 3
  formula = Bi
  name = G4_Bi
  specific = 4
FEATURE [App::DocumentObjectGroupPython] Po_element001  label="Po_element : 1"  # scripted group (container) (typed FeaturePython)
  n = 1
  ref = Po_element
FEATURE [App::DocumentObjectGroupPython] G4_Po  # scripted group (container) (typed FeaturePython)
  Dunit = g/cm3
  Dvalue = 9.32
  Group = -> [Po_element001]
  conduct = 2
  density = 1
  expand = 3
  formula = Po
  name = G4_Po
  specific = 4
FEATURE [App::DocumentObjectGroupPython] At_element001  label="At_element : 1"  # scripted group (container) (typed FeaturePython)
  n = 1
  ref = At_element
FEATURE [App::DocumentObjectGroupPython] G4_At  # scripted group (container) (typed FeaturePython)
  Dunit = g/cm3
  Dvalue = 9.32
  Group = -> [At_element001]
  conduct = 2
  density = 1
  expand = 3
  formula = At
  name = G4_At
  specific = 4
FEATURE [App::DocumentObjectGroupPython] Rn_element001  label="Rn_element : 1"  # scripted group (container) (typed FeaturePython)
  n = 1
  ref = Rn_element
FEATURE [App::DocumentObjectGroupPython] G4_Rn  # scripted group (container) (typed FeaturePython)
  Dunit = g/cm3
  Dvalue = 0.00900662
  Group = -> [Rn_element001]
  conduct = 2
  density = 1
  expand = 3
  formula = Rn
  name = G4_Rn
  specific = 4
FEATURE [App::DocumentObjectGroupPython] Fr_element001  label="Fr_element : 1"  # scripted group (container) (typed FeaturePython)
  n = 1
  ref = Fr_element
FEATURE [App::DocumentObjectGroupPython] G4_Fr  # scripted group (container) (typed FeaturePython)
  Dunit = g/cm3
  Dvalue = 1
  Group = -> [Fr_element001]
  conduct = 2
  density = 1
  expand = 3
  formula = Fr
  name = G4_Fr
  specific = 4
FEATURE [App::DocumentObjectGroupPython] Ra_element001  label="Ra_element : 1"  # scripted group (container) (typed FeaturePython)
  n = 1
  ref = Ra_element
FEATURE [App::DocumentObjectGroupPython] G4_Ra  # scripted group (container) (typed FeaturePython)
  Dunit = g/cm3
  Dvalue = 5
  Group = -> [Ra_element001]
  conduct = 2
  density = 1
  expand = 3
  formula = Ra
  name = G4_Ra
  specific = 4
FEATURE [App::DocumentObjectGroupPython] Ac_element001  label="Ac_element : 1"  # scripted group (container) (typed FeaturePython)
  n = 1
  ref = Ac_element
FEATURE [App::DocumentObjectGroupPython] G4_Ac  # scripted group (container) (typed FeaturePython)
  Dunit = g/cm3
  Dvalue = 10.07
  Group = -> [Ac_element001]
  conduct = 2
  density = 1
  expand = 3
  formula = Ac
  name = G4_Ac
  specific = 4
FEATURE [App::DocumentObjectGroupPython] Th_element001  label="Th_element : 1"  # scripted group (container) (typed FeaturePython)
  n = 1
  ref = Th_element
FEATURE [App::DocumentObjectGroupPython] G4_Th  # scripted group (container) (typed FeaturePython)
  Dunit = g/cm3
  Dvalue = 11.72
  Group = -> [Th_element001]
  conduct = 2
  density = 1
  expand = 3
  formula = Th
  name = G4_Th
  specific = 4
FEATURE [App::DocumentObjectGroupPython] Pa_element001  label="Pa_element : 1"  # scripted group (container) (typed FeaturePython)
  n = 1
  ref = Pa_element
FEATURE [App::DocumentObjectGroupPython] G4_Pa  # scripted group (container) (typed FeaturePython)
  Dunit = g/cm3
  Dvalue = 15.37
  Group = -> [Pa_element001]
  conduct = 2
  density = 1
  expand = 3
  formula = Pa
  name = G4_Pa
  specific = 4
FEATURE [App::DocumentObjectGroupPython] U_element004  label="U_element : 004"  # scripted group (container) (typed FeaturePython)
  n = 1
  ref = U_element
FEATURE [App::DocumentObjectGroupPython] G4_U  # scripted group (container) (typed FeaturePython)
  Dunit = g/cm3
  Dvalue = 18.95
  Group = -> [U_element004]
  conduct = 2
  density = 1
  expand = 3
  formula = U
  name = G4_U
  specific = 4
FEATURE [App::DocumentObjectGroupPython] Np_element001  label="Np_element : 1"  # scripted group (container) (typed FeaturePython)
  n = 1
  ref = Np_element
FEATURE [App::DocumentObjectGroupPython] G4_Np  # scripted group (container) (typed FeaturePython)
  Dunit = g/cm3
  Dvalue = 20.25
  Group = -> [Np_element001]
  conduct = 2
  density = 1
  expand = 3
  formula = Np
  name = G4_Np
  specific = 4
FEATURE [App::DocumentObjectGroupPython] Pu_element002  label="Pu_element : 002"  # scripted group (container) (typed FeaturePython)
  n = 1
  ref = Pu_element
FEATURE [App::DocumentObjectGroupPython] G4_Pu  # scripted group (container) (typed FeaturePython)
  Dunit = g/cm3
  Dvalue = 19.84
  Group = -> [Pu_element002]
  conduct = 2
  density = 1
  expand = 3
  formula = Pu
  name = G4_Pu
  specific = 4
FEATURE [App::DocumentObjectGroupPython] Am_element001  label="Am_element : 1"  # scripted group (container) (typed FeaturePython)
  n = 1
  ref = Am_element
FEATURE [App::DocumentObjectGroupPython] G4_Am  # scripted group (container) (typed FeaturePython)
  Dunit = g/cm3
  Dvalue = 13.67
  Group = -> [Am_element001]
  conduct = 2
  density = 1
  expand = 3
  formula = Am
  name = G4_Am
  specific = 4
FEATURE [App::DocumentObjectGroupPython] Cm_element001  label="Cm_element : 1"  # scripted group (container) (typed FeaturePython)
  n = 1
  ref = Cm_element
FEATURE [App::DocumentObjectGroupPython] G4_Cm  # scripted group (container) (typed FeaturePython)
  Dunit = g/cm3
  Dvalue = 13.51
  Group = -> [Cm_element001]
  conduct = 2
  density = 1
  expand = 3
  formula = Cm
  name = G4_Cm
  specific = 4
FEATURE [App::DocumentObjectGroupPython] Bk_element001  label="Bk_element : 1"  # scripted group (container) (typed FeaturePython)
  n = 1
  ref = Bk_element
FEATURE [App::DocumentObjectGroupPython] G4_Bk  # scripted group (container) (typed FeaturePython)
  Dunit = g/cm3
  Dvalue = 14
  Group = -> [Bk_element001]
  conduct = 2
  density = 1
  expand = 3
  formula = Bk
  name = G4_Bk
  specific = 4
FEATURE [App::DocumentObjectGroupPython] Cf_element001  label="Cf_element : 1"  # scripted group (container) (typed FeaturePython)
  n = 1
  ref = Cf_element
FEATURE [App::DocumentObjectGroupPython] G4_Cf  # scripted group (container) (typed FeaturePython)
  Dunit = g/cm3
  Dvalue = 10
  Group = -> [Cf_element001]
  conduct = 2
  density = 1
  expand = 3
  formula = Cf
  name = G4_Cf
  specific = 4
FEATURE [App::DocumentObjectGroupPython] Element  # scripted group (container) (typed FeaturePython)
  Group = -> [G4_H,G4_He,G4_Li,G4_Be,G4_B,G4_C,G4_N,G4_O,G4_F,G4_Ne,G4_Na,G4_Mg,G4_Al,G4_Si,G4_P,G4_S,G4_Cl,G4_Ar,G4_K,G4_Ca,G4_Sc,G4_Ti,G4_V,G4_Cr,G4_Mn,G4_Fe,G4_Co,G4_Ni,G4_Cu,G4_Zn,G4_Ga,G4_Ge,G4_As,G4_Se,G4_Br,G4_Kr,G4_Rb,G4_Sr,G4_Y,G4_Zr,G4_Nb,G4_Mo,G4_Tc,G4_Ru,G4_Rh,G4_Pd,G4_Ag,G4_Cd,G4_In,G4_Sn,G4_Sb,G4_Te,G4_I,G4_Xe,G4_Cs,G4_Ba,G4_La,G4_Ce,G4_Pr,G4_Nd,G4_Pm,G4_Sm,G4_Eu,G4_Gd,G4_Tb,G4_Dy,G4_Ho,G4_Er,+30 more]
FEATURE [App::DocumentObjectGroupPython] H_element114  label="H_element : 063"  # scripted group (container) (typed FeaturePython)
  n = 2
  ref = H_element
FEATURE [App::DocumentObjectGroupPython] G4_lH2  # scripted group (container) (typed FeaturePython)
  Dunit = g/cm3
  Dvalue = 0.0708
  Group = -> [H_element114]
  conduct = 2
  density = 1
  expand = 3
  formula = G4_lH2
  name = G4_lH2
  specific = 4
FEATURE [App::DocumentObjectGroupPython] N_element049  label="N_element : 022"  # scripted group (container) (typed FeaturePython)
  n = 2
  ref = N_element
FEATURE [App::DocumentObjectGroupPython] G4_lN2  # scripted group (container) (typed FeaturePython)
  Dunit = g/cm3
  Dvalue = 0.807
  Group = -> [N_element049]
  conduct = 2
  density = 1
  expand = 3
  formula = G4_lN2
  name = G4_lN2
  specific = 4
FEATURE [App::DocumentObjectGroupPython] O_element106  label="O_element : 060"  # scripted group (container) (typed FeaturePython)
  n = 2
  ref = O_element
FEATURE [App::DocumentObjectGroupPython] G4_lO2  # scripted group (container) (typed FeaturePython)
  Dunit = g/cm3
  Dvalue = 1.141
  Group = -> [O_element106]
  conduct = 2
  density = 1
  expand = 3
  formula = G4_lO2
  name = G4_lO2
  specific = 4
FEATURE [App::DocumentObjectGroupPython] Ar_element003  label="Ar_element : 002"  # scripted group (container) (typed FeaturePython)
  n = 1
  ref = Ar_element
FEATURE [App::DocumentObjectGroupPython] G4_lAr  # scripted group (container) (typed FeaturePython)
  Dunit = g/cm3
  Dvalue = 1.396
  Group = -> [Ar_element003]
  conduct = 2
  density = 1
  expand = 3
  formula = G4_lAr
  name = G4_lAr
  specific = 4
FEATURE [App::DocumentObjectGroupPython] Br_element008  label="Br_element : 005"  # scripted group (container) (typed FeaturePython)
  n = 1
  ref = Br_element
FEATURE [App::DocumentObjectGroupPython] G4_lBr  # scripted group (container) (typed FeaturePython)
  Dunit = g/cm3
  Dvalue = 3.1028
  Group = -> [Br_element008]
  conduct = 2
  density = 1
  expand = 3
  formula = G4_lBr
  name = G4_lBr
  specific = 4
FEATURE [App::DocumentObjectGroupPython] Kr_element002  label="Kr_element : 002"  # scripted group (container) (typed FeaturePython)
  n = 1
  ref = Kr_element
FEATURE [App::DocumentObjectGroupPython] G4_lKr  # scripted group (container) (typed FeaturePython)
  Dunit = g/cm3
  Dvalue = 2.418
  Group = -> [Kr_element002]
  conduct = 2
  density = 1
  expand = 3
  formula = G4_lKr
  name = G4_lKr
  specific = 4
FEATURE [App::DocumentObjectGroupPython] Xe_element002  label="Xe_element : 002"  # scripted group (container) (typed FeaturePython)
  n = 1
  ref = Xe_element
FEATURE [App::DocumentObjectGroupPython] G4_lXe  # scripted group (container) (typed FeaturePython)
  Dunit = g/cm3
  Dvalue = 2.953
  Group = -> [Xe_element002]
  conduct = 2
  density = 1
  expand = 3
  formula = G4_lXe
  name = G4_lXe
  specific = 4
FEATURE [App::DocumentObjectGroupPython] O_element107  label="O_element : 061"  # scripted group (container) (typed FeaturePython)
  n = 4
  ref = O_element
FEATURE [App::DocumentObjectGroupPython] Pb_element004  label="Pb_element : 002"  # scripted group (container) (typed FeaturePython)
  n = 1
  ref = Pb_element
FEATURE [App::DocumentObjectGroupPython] W_element005  label="W_element : 005"  # scripted group (container) (typed FeaturePython)
  n = 1
  ref = W_element
FEATURE [App::DocumentObjectGroupPython] G4_PbWO4  # scripted group (container) (typed FeaturePython)
  Dunit = g/cm3
  Dvalue = 8.28
  Group = -> [O_element107,Pb_element004,W_element005]
  conduct = 2
  density = 1
  expand = 3
  formula = G4_PbWO4
  name = G4_PbWO4
  specific = 4
FEATURE [App::DocumentObjectGroupPython] H_element115  label="H_element : 064"  # scripted group (container) (typed FeaturePython)
  n = 1
  ref = H_element
FEATURE [App::DocumentObjectGroupPython] G4_Galactic  # scripted group (container) (typed FeaturePython)
  Dunit = g/cm3
  Dvalue = 0
  Group = -> [H_element115]
  conduct = 2
  density = 1
  expand = 3
  formula = G4_Galactic
  name = G4_Galactic
  specific = 4
FEATURE [App::DocumentObjectGroupPython] C_element125  label="C_element : 071"  # scripted group (container) (typed FeaturePython)
  n = 1
  ref = C_element
FEATURE [App::DocumentObjectGroupPython] G4_GRAPHITE_POROUS  # scripted group (container) (typed FeaturePython)
  Dunit = g/cm3
  Dvalue = 1.7
  Group = -> [C_element125]
  conduct = 2
  density = 1
  expand = 3
  formula = G4_GRAPHITE_POROUS
  name = G4_GRAPHITE_POROUS
  specific = 4
FEATURE [App::DocumentObjectGroupPython] H_element116  label="H_element : 0.150"  # scripted group (container) (typed FeaturePython)
  n = 0.080538
FEATURE [App::DocumentObjectGroupPython] C_element126  label="C_element : 0.600"  # scripted group (container) (typed FeaturePython)
  n = 0.599848
FEATURE [App::DocumentObjectGroupPython] O_element108  label="O_element : 0.320"  # scripted group (container) (typed FeaturePython)
  n = 0.319614
FEATURE [App::DocumentObjectGroupPython] G4_LUCITE  # scripted group (container) (typed FeaturePython)
  Dunit = g/cm3
  Dvalue = 1.19
  Group = -> [H_element116,C_element126,O_element108]
  conduct = 2
  density = 1
  expand = 3
  formula = G4_LUCITE
  name = G4_LUCITE
  specific = 4
FEATURE [App::DocumentObjectGroupPython] Cu_element002  label="Cu_element : 62"  # scripted group (container) (typed FeaturePython)
  n = 62
  ref = Cu_element
FEATURE [App::DocumentObjectGroupPython] Zn_element002  label="Zn_element : 35"  # scripted group (container) (typed FeaturePython)
  n = 35
  ref = Zn_element
FEATURE [App::DocumentObjectGroupPython] Pb_element005  label="Pb_element : 3"  # scripted group (container) (typed FeaturePython)
  n = 3
  ref = Pb_element
FEATURE [App::DocumentObjectGroupPython] G4_BRASS  # scripted group (container) (typed FeaturePython)
  Dunit = g/cm3
  Dvalue = 8.52
  Group = -> [Cu_element002,Zn_element002,Pb_element005]
  conduct = 2
  density = 1
  expand = 3
  formula = G4_BRASS
  name = G4_BRASS
  specific = 4
FEATURE [App::DocumentObjectGroupPython] Cu_element003  label="Cu_element : 89"  # scripted group (container) (typed FeaturePython)
  n = 89
  ref = Cu_element
FEATURE [App::DocumentObjectGroupPython] Zn_element003  label="Zn_element : 9"  # scripted group (container) (typed FeaturePython)
  n = 9
  ref = Zn_element
FEATURE [App::DocumentObjectGroupPython] Pb_element006  label="Pb_element : 2"  # scripted group (container) (typed FeaturePython)
  n = 2
  ref = Pb_element
FEATURE [App::DocumentObjectGroupPython] G4_BRONZE  # scripted group (container) (typed FeaturePython)
  Dunit = g/cm3
  Dvalue = 8.82
  Group = -> [Cu_element003,Zn_element003,Pb_element006]
  conduct = 2
  density = 1
  expand = 3
  formula = G4_BRONZE
  name = G4_BRONZE
  specific = 4
FEATURE [App::DocumentObjectGroupPython] Fe_element008  label="Fe_element : 74"  # scripted group (container) (typed FeaturePython)
  n = 74
  ref = Fe_element
FEATURE [App::DocumentObjectGroupPython] Cr_element002  label="Cr_element : 18"  # scripted group (container) (typed FeaturePython)
  n = 18
  ref = Cr_element
FEATURE [App::DocumentObjectGroupPython] Ni_element002  label="Ni_element : 8"  # scripted group (container) (typed FeaturePython)
  n = 8
  ref = Ni_element
FEATURE [App::DocumentObjectGroupPython] G4_STAINLESS_STEEL  label="G4_STAINLESS-STEEL"  # scripted group (container) (typed FeaturePython)
  Dunit = g/cm3
  Dvalue = 8
  Group = -> [Fe_element008,Cr_element002,Ni_element002]
  conduct = 2
  density = 1
  expand = 3
  formula = G4_STAINLESS-STEEL
  name = G4_STAINLESS-STEEL
  specific = 4
FEATURE [App::DocumentObjectGroupPython] H_element117  label="H_element : 065"  # scripted group (container) (typed FeaturePython)
  n = 18
  ref = H_element
FEATURE [App::DocumentObjectGroupPython] C_element127  label="C_element : 072"  # scripted group (container) (typed FeaturePython)
  n = 12
  ref = C_element
FEATURE [App::DocumentObjectGroupPython] O_element109  label="O_element : 062"  # scripted group (container) (typed FeaturePython)
  n = 7
  ref = O_element
FEATURE [App::DocumentObjectGroupPython] G4_CR39  # scripted group (container) (typed FeaturePython)
  Dunit = g/cm3
  Dvalue = 1.32
  Group = -> [H_element117,C_element127,O_element109]
  conduct = 2
  density = 1
  expand = 3
  formula = G4_CR39
  name = G4_CR39
  specific = 4
FEATURE [App::DocumentObjectGroupPython] H_element118  label="H_element : 38"  # scripted group (container) (typed FeaturePython)
  n = 38
  ref = H_element
FEATURE [App::DocumentObjectGroupPython] C_element128  label="C_element : 073"  # scripted group (container) (typed FeaturePython)
  n = 18
  ref = C_element
FEATURE [App::DocumentObjectGroupPython] O_element110  label="O_element : 063"  # scripted group (container) (typed FeaturePython)
  n = 1
  ref = O_element
FEATURE [App::DocumentObjectGroupPython] G4_OCTADECANOL  # scripted group (container) (typed FeaturePython)
  Dunit = g/cm3
  Dvalue = 0.812
  Group = -> [H_element118,C_element128,O_element110]
  conduct = 2
  density = 1
  expand = 3
  formula = G4_OCTADECANOL
  name = G4_OCTADECANOL
  specific = 4
FEATURE [App::DocumentObjectGroupPython] HEP  # scripted group (container) (typed FeaturePython)
  Group = -> [G4_lH2,G4_lN2,G4_lO2,G4_lAr,G4_lBr,G4_lKr,G4_lXe,G4_PbWO4,G4_Galactic,G4_GRAPHITE_POROUS,G4_LUCITE,G4_BRASS,G4_BRONZE,G4_STAINLESS_STEEL,G4_CR39,G4_OCTADECANOL]
FEATURE [App::DocumentObjectGroupPython] C_element129  label="C_element : 074"  # scripted group (container) (typed FeaturePython)
  n = 14
  ref = C_element
FEATURE [App::DocumentObjectGroupPython] H_element119  label="H_element : 066"  # scripted group (container) (typed FeaturePython)
  n = 10
  ref = H_element
FEATURE [App::DocumentObjectGroupPython] O_element111  label="O_element : 064"  # scripted group (container) (typed FeaturePython)
  n = 2
  ref = O_element
FEATURE [App::DocumentObjectGroupPython] N_element050  label="N_element : 023"  # scripted group (container) (typed FeaturePython)
  n = 2
  ref = N_element
FEATURE [App::DocumentObjectGroupPython] G4_KEVLAR  # scripted group (container) (typed FeaturePython)
  Dunit = g/cm3
  Dvalue = 1.44
  Group = -> [C_element129,H_element119,O_element111,N_element050]
  conduct = 2
  density = 1
  expand = 3
  formula = G4_KEVLAR
  name = G4_KEVLAR
  specific = 4
FEATURE [App::DocumentObjectGroupPython] C_element130  label="C_element : 075"  # scripted group (container) (typed FeaturePython)
  n = 10
  ref = C_element
FEATURE [App::DocumentObjectGroupPython] H_element120  label="H_element : 067"  # scripted group (container) (typed FeaturePython)
  n = 8
  ref = H_element
FEATURE [App::DocumentObjectGroupPython] O_element112  label="O_element : 065"  # scripted group (container) (typed FeaturePython)
  n = 4
  ref = O_element
FEATURE [App::DocumentObjectGroupPython] G4_DACRON  # scripted group (container) (typed FeaturePython)
  Dunit = g/cm3
  Dvalue = 1.4
  Group = -> [C_element130,H_element120,O_element112]
  conduct = 2
  density = 1
  expand = 3
  formula = G4_DACRON
  name = G4_DACRON
  specific = 4
FEATURE [App::DocumentObjectGroupPython] C_element131  label="C_element : 076"  # scripted group (container) (typed FeaturePython)
  n = 4
  ref = C_element
FEATURE [App::DocumentObjectGroupPython] H_element121  label="H_element : 068"  # scripted group (container) (typed FeaturePython)
  n = 5
  ref = H_element
FEATURE [App::DocumentObjectGroupPython] Cl_element030  label="Cl_element : 016"  # scripted group (container) (typed FeaturePython)
  n = 1
  ref = Cl_element
FEATURE [App::DocumentObjectGroupPython] G4_NEOPRENE  # scripted group (container) (typed FeaturePython)
  Dunit = g/cm3
  Dvalue = 1.23
  Group = -> [C_element131,H_element121,Cl_element030]
  conduct = 2
  density = 1
  expand = 3
  formula = G4_NEOPRENE
  name = G4_NEOPRENE
  specific = 4
FEATURE [App::DocumentObjectGroupPython] Space  # scripted group (container) (typed FeaturePython)
  Group = -> [G4_KEVLAR,G4_DACRON,G4_NEOPRENE]
FEATURE [App::DocumentObjectGroupPython] H_element122  label="H_element : 069"  # scripted group (container) (typed FeaturePython)
  n = 5
  ref = H_element
FEATURE [App::DocumentObjectGroupPython] C_element132  label="C_element : 077"  # scripted group (container) (typed FeaturePython)
  n = 4
  ref = C_element
FEATURE [App::DocumentObjectGroupPython] N_element051  label="N_element : 3"  # scripted group (container) (typed FeaturePython)
  n = 3
  ref = N_element
FEATURE [App::DocumentObjectGroupPython] O_element113  label="O_element : 066"  # scripted group (container) (typed FeaturePython)
  n = 1
  ref = O_element
FEATURE [App::DocumentObjectGroupPython] G4_CYTOSINE  # scripted group (container) (typed FeaturePython)
  Dunit = g/cm3
  Dvalue = 1.55
  Group = -> [H_element122,C_element132,N_element051,O_element113]
  conduct = 2
  density = 1
  expand = 3
  formula = G4_CYTOSINE
  name = G4_CYTOSINE
  specific = 4
FEATURE [App::DocumentObjectGroupPython] H_element123  label="H_element : 070"  # scripted group (container) (typed FeaturePython)
  n = 6
  ref = H_element
FEATURE [App::DocumentObjectGroupPython] C_element133  label="C_element : 078"  # scripted group (container) (typed FeaturePython)
  n = 5
  ref = C_element
FEATURE [App::DocumentObjectGroupPython] N_element052  label="N_element : 024"  # scripted group (container) (typed FeaturePython)
  n = 2
  ref = N_element
FEATURE [App::DocumentObjectGroupPython] O_element114  label="O_element : 067"  # scripted group (container) (typed FeaturePython)
  n = 2
  ref = O_element
FEATURE [App::DocumentObjectGroupPython] G4_THYMINE  # scripted group (container) (typed FeaturePython)
  Dunit = g/cm3
  Dvalue = 1.23
  Group = -> [H_element123,C_element133,N_element052,O_element114]
  conduct = 2
  density = 1
  expand = 3
  formula = G4_THYMINE
  name = G4_THYMINE
  specific = 4
FEATURE [App::DocumentObjectGroupPython] H_element124  label="H_element : 071"  # scripted group (container) (typed FeaturePython)
  n = 4
  ref = H_element
FEATURE [App::DocumentObjectGroupPython] C_element134  label="C_element : 079"  # scripted group (container) (typed FeaturePython)
  n = 4
  ref = C_element
FEATURE [App::DocumentObjectGroupPython] N_element053  label="N_element : 025"  # scripted group (container) (typed FeaturePython)
  n = 2
  ref = N_element
FEATURE [App::DocumentObjectGroupPython] O_element115  label="O_element : 068"  # scripted group (container) (typed FeaturePython)
  n = 2
  ref = O_element
FEATURE [App::DocumentObjectGroupPython] G4_URACIL  # scripted group (container) (typed FeaturePython)
  Dunit = g/cm3
  Dvalue = 1.32
  Group = -> [H_element124,C_element134,N_element053,O_element115]
  conduct = 2
  density = 1
  expand = 3
  formula = G4_URACIL
  name = G4_URACIL
  specific = 4
FEATURE [App::DocumentObjectGroupPython] H_element125  label="H_element : 072"  # scripted group (container) (typed FeaturePython)
  n = 4
  ref = H_element
FEATURE [App::DocumentObjectGroupPython] C_element135  label="C_element : 080"  # scripted group (container) (typed FeaturePython)
  n = 5
  ref = C_element
FEATURE [App::DocumentObjectGroupPython] N_element054  label="N_element : 026"  # scripted group (container) (typed FeaturePython)
  n = 5
  ref = N_element
FEATURE [App::DocumentObjectGroupPython] G4_DNA_ADENINE  # scripted group (container) (typed FeaturePython)
  Dunit = g/cm3
  Dvalue = 1
  Group = -> [H_element125,C_element135,N_element054]
  conduct = 2
  density = 1
  expand = 3
  formula = G4_DNA_ADENINE
  name = G4_DNA_ADENINE
  specific = 4
FEATURE [App::DocumentObjectGroupPython] H_element126  label="H_element : 073"  # scripted group (container) (typed FeaturePython)
  n = 4
  ref = H_element
FEATURE [App::DocumentObjectGroupPython] C_element136  label="C_element : 081"  # scripted group (container) (typed FeaturePython)
  n = 5
  ref = C_element
FEATURE [App::DocumentObjectGroupPython] N_element055  label="N_element : 027"  # scripted group (container) (typed FeaturePython)
  n = 5
  ref = N_element
FEATURE [App::DocumentObjectGroupPython] O_element116  label="O_element : 069"  # scripted group (container) (typed FeaturePython)
  n = 1
  ref = O_element
FEATURE [App::DocumentObjectGroupPython] G4_DNA_GUANINE  # scripted group (container) (typed FeaturePython)
  Dunit = g/cm3
  Dvalue = 1
  Group = -> [H_element126,C_element136,N_element055,O_element116]
  conduct = 2
  density = 1
  expand = 3
  formula = G4_DNA_GUANINE
  name = G4_DNA_GUANINE
  specific = 4
FEATURE [App::DocumentObjectGroupPython] H_element127  label="H_element : 074"  # scripted group (container) (typed FeaturePython)
  n = 4
  ref = H_element
FEATURE [App::DocumentObjectGroupPython] C_element137  label="C_element : 082"  # scripted group (container) (typed FeaturePython)
  n = 4
  ref = C_element
FEATURE [App::DocumentObjectGroupPython] N_element056  label="N_element : 028"  # scripted group (container) (typed FeaturePython)
  n = 3
  ref = N_element
FEATURE [App::DocumentObjectGroupPython] O_element117  label="O_element : 070"  # scripted group (container) (typed FeaturePython)
  n = 1
  ref = O_element
FEATURE [App::DocumentObjectGroupPython] G4_DNA_CYTOSINE  # scripted group (container) (typed FeaturePython)
  Dunit = g/cm3
  Dvalue = 1
  Group = -> [H_element127,C_element137,N_element056,O_element117]
  conduct = 2
  density = 1
  expand = 3
  formula = G4_DNA_CYTOSINE
  name = G4_DNA_CYTOSINE
  specific = 4
FEATURE [App::DocumentObjectGroupPython] H_element128  label="H_element : 075"  # scripted group (container) (typed FeaturePython)
  n = 5
  ref = H_element
FEATURE [App::DocumentObjectGroupPython] C_element138  label="C_element : 083"  # scripted group (container) (typed FeaturePython)
  n = 5
  ref = C_element
FEATURE [App::DocumentObjectGroupPython] N_element057  label="N_element : 029"  # scripted group (container) (typed FeaturePython)
  n = 2
  ref = N_element
FEATURE [App::DocumentObjectGroupPython] O_element118  label="O_element : 071"  # scripted group (container) (typed FeaturePython)
  n = 2
  ref = O_element
FEATURE [App::DocumentObjectGroupPython] G4_DNA_THYMINE  # scripted group (container) (typed FeaturePython)
  Dunit = g/cm3
  Dvalue = 1
  Group = -> [H_element128,C_element138,N_element057,O_element118]
  conduct = 2
  density = 1
  expand = 3
  formula = G4_DNA_THYMINE
  name = G4_DNA_THYMINE
  specific = 4
FEATURE [App::DocumentObjectGroupPython] H_element129  label="H_element : 076"  # scripted group (container) (typed FeaturePython)
  n = 3
  ref = H_element
FEATURE [App::DocumentObjectGroupPython] C_element139  label="C_element : 084"  # scripted group (container) (typed FeaturePython)
  n = 4
  ref = C_element
FEATURE [App::DocumentObjectGroupPython] N_element058  label="N_element : 030"  # scripted group (container) (typed FeaturePython)
  n = 2
  ref = N_element
FEATURE [App::DocumentObjectGroupPython] O_element119  label="O_element : 072"  # scripted group (container) (typed FeaturePython)
  n = 2
  ref = O_element
FEATURE [App::DocumentObjectGroupPython] G4_DNA_URACIL  # scripted group (container) (typed FeaturePython)
  Dunit = g/cm3
  Dvalue = 1
  Group = -> [H_element129,C_element139,N_element058,O_element119]
  conduct = 2
  density = 1
  expand = 3
  formula = G4_DNA_URACIL
  name = G4_DNA_URACIL
  specific = 4
FEATURE [App::DocumentObjectGroupPython] H_element130  label="H_element : 077"  # scripted group (container) (typed FeaturePython)
  n = 10
  ref = H_element
FEATURE [App::DocumentObjectGroupPython] C_element140  label="C_element : 085"  # scripted group (container) (typed FeaturePython)
  n = 10
  ref = C_element
FEATURE [App::DocumentObjectGroupPython] N_element059  label="N_element : 031"  # scripted group (container) (typed FeaturePython)
  n = 5
  ref = N_element
FEATURE [App::DocumentObjectGroupPython] O_element120  label="O_element : 073"  # scripted group (container) (typed FeaturePython)
  n = 4
  ref = O_element
FEATURE [App::DocumentObjectGroupPython] G4_DNA_ADENOSINE  # scripted group (container) (typed FeaturePython)
  Dunit = g/cm3
  Dvalue = 1
  Group = -> [H_element130,C_element140,N_element059,O_element120]
  conduct = 2
  density = 1
  expand = 3
  formula = G4_DNA_ADENOSINE
  name = G4_DNA_ADENOSINE
  specific = 4
FEATURE [App::DocumentObjectGroupPython] H_element131  label="H_element : 078"  # scripted group (container) (typed FeaturePython)
  n = 10
  ref = H_element
FEATURE [App::DocumentObjectGroupPython] C_element141  label="C_element : 086"  # scripted group (container) (typed FeaturePython)
  n = 10
  ref = C_element
FEATURE [App::DocumentObjectGroupPython] N_element060  label="N_element : 032"  # scripted group (container) (typed FeaturePython)
  n = 5
  ref = N_element
FEATURE [App::DocumentObjectGroupPython] O_element121  label="O_element : 074"  # scripted group (container) (typed FeaturePython)
  n = 5
  ref = O_element
FEATURE [App::DocumentObjectGroupPython] G4_DNA_GUANOSINE  # scripted group (container) (typed FeaturePython)
  Dunit = g/cm3
  Dvalue = 1
  Group = -> [H_element131,C_element141,N_element060,O_element121]
  conduct = 2
  density = 1
  expand = 3
  formula = G4_DNA_GUANOSINE
  name = G4_DNA_GUANOSINE
  specific = 4
FEATURE [App::DocumentObjectGroupPython] H_element132  label="H_element : 079"  # scripted group (container) (typed FeaturePython)
  n = 10
  ref = H_element
FEATURE [App::DocumentObjectGroupPython] C_element142  label="C_element : 087"  # scripted group (container) (typed FeaturePython)
  n = 9
  ref = C_element
FEATURE [App::DocumentObjectGroupPython] N_element061  label="N_element : 033"  # scripted group (container) (typed FeaturePython)
  n = 3
  ref = N_element
FEATURE [App::DocumentObjectGroupPython] O_element122  label="O_element : 075"  # scripted group (container) (typed FeaturePython)
  n = 5
  ref = O_element
FEATURE [App::DocumentObjectGroupPython] G4_DNA_CYTIDINE  # scripted group (container) (typed FeaturePython)
  Dunit = g/cm3
  Dvalue = 1
  Group = -> [H_element132,C_element142,N_element061,O_element122]
  conduct = 2
  density = 1
  expand = 3
  formula = G4_DNA_CYTIDINE
  name = G4_DNA_CYTIDINE
  specific = 4
FEATURE [App::DocumentObjectGroupPython] H_element133  label="H_element : 080"  # scripted group (container) (typed FeaturePython)
  n = 9
  ref = H_element
FEATURE [App::DocumentObjectGroupPython] C_element143  label="C_element : 088"  # scripted group (container) (typed FeaturePython)
  n = 9
  ref = C_element
FEATURE [App::DocumentObjectGroupPython] N_element062  label="N_element : 034"  # scripted group (container) (typed FeaturePython)
  n = 2
  ref = N_element
FEATURE [App::DocumentObjectGroupPython] O_element123  label="O_element : 076"  # scripted group (container) (typed FeaturePython)
  n = 6
  ref = O_element
FEATURE [App::DocumentObjectGroupPython] G4_DNA_URIDINE  # scripted group (container) (typed FeaturePython)
  Dunit = g/cm3
  Dvalue = 1
  Group = -> [H_element133,C_element143,N_element062,O_element123]
  conduct = 2
  density = 1
  expand = 3
  formula = G4_DNA_URIDINE
  name = G4_DNA_URIDINE
  specific = 4
FEATURE [App::DocumentObjectGroupPython] H_element134  label="H_element : 081"  # scripted group (container) (typed FeaturePython)
  n = 11
  ref = H_element
FEATURE [App::DocumentObjectGroupPython] C_element144  label="C_element : 089"  # scripted group (container) (typed FeaturePython)
  n = 10
  ref = C_element
FEATURE [App::DocumentObjectGroupPython] N_element063  label="N_element : 035"  # scripted group (container) (typed FeaturePython)
  n = 2
  ref = N_element
FEATURE [App::DocumentObjectGroupPython] O_element124  label="O_element : 077"  # scripted group (container) (typed FeaturePython)
  n = 6
  ref = O_element
FEATURE [App::DocumentObjectGroupPython] G4_DNA_METHYLURIDINE  # scripted group (container) (typed FeaturePython)
  Dunit = g/cm3
  Dvalue = 1
  Group = -> [H_element134,C_element144,N_element063,O_element124]
  conduct = 2
  density = 1
  expand = 3
  formula = G4_DNA_METHYLURIDINE
  name = G4_DNA_METHYLURIDINE
  specific = 4
FEATURE [App::DocumentObjectGroupPython] P_element014  label="P_element : 003"  # scripted group (container) (typed FeaturePython)
  n = 1
  ref = P_element
FEATURE [App::DocumentObjectGroupPython] O_element125  label="O_element : 078"  # scripted group (container) (typed FeaturePython)
  n = 3
  ref = O_element
FEATURE [App::DocumentObjectGroupPython] G4_DNA_MONOPHOSPHATE  # scripted group (container) (typed FeaturePython)
  Dunit = g/cm3
  Dvalue = 1
  Group = -> [P_element014,O_element125]
  conduct = 2
  density = 1
  expand = 3
  formula = G4_DNA_MONOPHOSPHATE
  name = G4_DNA_MONOPHOSPHATE
  specific = 4
FEATURE [App::DocumentObjectGroupPython] H_element135  label="H_element : 082"  # scripted group (container) (typed FeaturePython)
  n = 10
  ref = H_element
FEATURE [App::DocumentObjectGroupPython] C_element145  label="C_element : 090"  # scripted group (container) (typed FeaturePython)
  n = 10
  ref = C_element
FEATURE [App::DocumentObjectGroupPython] N_element064  label="N_element : 036"  # scripted group (container) (typed FeaturePython)
  n = 5
  ref = N_element
FEATURE [App::DocumentObjectGroupPython] O_element126  label="O_element : 079"  # scripted group (container) (typed FeaturePython)
  n = 7
  ref = O_element
FEATURE [App::DocumentObjectGroupPython] P_element015  label="P_element : 004"  # scripted group (container) (typed FeaturePython)
  n = 1
  ref = P_element
FEATURE [App::DocumentObjectGroupPython] G4_DNA_A  # scripted group (container) (typed FeaturePython)
  Dunit = g/cm3
  Dvalue = 1
  Group = -> [H_element135,C_element145,N_element064,O_element126,P_element015]
  conduct = 2
  density = 1
  expand = 3
  formula = G4_DNA_A
  name = G4_DNA_A
  specific = 4
FEATURE [App::DocumentObjectGroupPython] H_element136  label="H_element : 083"  # scripted group (container) (typed FeaturePython)
  n = 10
  ref = H_element
FEATURE [App::DocumentObjectGroupPython] C_element146  label="C_element : 091"  # scripted group (container) (typed FeaturePython)
  n = 10
  ref = C_element
FEATURE [App::DocumentObjectGroupPython] N_element065  label="N_element : 037"  # scripted group (container) (typed FeaturePython)
  n = 5
  ref = N_element
FEATURE [App::DocumentObjectGroupPython] O_element127  label="O_element : 8"  # scripted group (container) (typed FeaturePython)
  n = 8
  ref = O_element
FEATURE [App::DocumentObjectGroupPython] P_element016  label="P_element : 005"  # scripted group (container) (typed FeaturePython)
  n = 1
  ref = P_element
FEATURE [App::DocumentObjectGroupPython] G4_DNA_G  # scripted group (container) (typed FeaturePython)
  Dunit = g/cm3
  Dvalue = 1
  Group = -> [H_element136,C_element146,N_element065,O_element127,P_element016]
  conduct = 2
  density = 1
  expand = 3
  formula = G4_DNA_G
  name = G4_DNA_G
  specific = 4
FEATURE [App::DocumentObjectGroupPython] H_element137  label="H_element : 084"  # scripted group (container) (typed FeaturePython)
  n = 10
  ref = H_element
FEATURE [App::DocumentObjectGroupPython] C_element147  label="C_element : 092"  # scripted group (container) (typed FeaturePython)
  n = 9
  ref = C_element
FEATURE [App::DocumentObjectGroupPython] N_element066  label="N_element : 038"  # scripted group (container) (typed FeaturePython)
  n = 3
  ref = N_element
FEATURE [App::DocumentObjectGroupPython] O_element128  label="O_element : 080"  # scripted group (container) (typed FeaturePython)
  n = 8
  ref = O_element
FEATURE [App::DocumentObjectGroupPython] P_element017  label="P_element : 006"  # scripted group (container) (typed FeaturePython)
  n = 1
  ref = P_element
FEATURE [App::DocumentObjectGroupPython] G4_DNA_C  # scripted group (container) (typed FeaturePython)
  Dunit = g/cm3
  Dvalue = 1
  Group = -> [H_element137,C_element147,N_element066,O_element128,P_element017]
  conduct = 2
  density = 1
  expand = 3
  formula = G4_DNA_C
  name = G4_DNA_C
  specific = 4
FEATURE [App::DocumentObjectGroupPython] H_element138  label="H_element : 085"  # scripted group (container) (typed FeaturePython)
  n = 9
  ref = H_element
FEATURE [App::DocumentObjectGroupPython] C_element148  label="C_element : 093"  # scripted group (container) (typed FeaturePython)
  n = 9
  ref = C_element
FEATURE [App::DocumentObjectGroupPython] N_element067  label="N_element : 039"  # scripted group (container) (typed FeaturePython)
  n = 2
  ref = N_element
FEATURE [App::DocumentObjectGroupPython] O_element129  label="O_element : 9"  # scripted group (container) (typed FeaturePython)
  n = 9
  ref = O_element
FEATURE [App::DocumentObjectGroupPython] P_element018  label="P_element : 007"  # scripted group (container) (typed FeaturePython)
  n = 1
  ref = P_element
FEATURE [App::DocumentObjectGroupPython] G4_DNA_U  # scripted group (container) (typed FeaturePython)
  Dunit = g/cm3
  Dvalue = 1
  Group = -> [H_element138,C_element148,N_element067,O_element129,P_element018]
  conduct = 2
  density = 1
  expand = 3
  formula = G4_DNA_U
  name = G4_DNA_U
  specific = 4
FEATURE [App::DocumentObjectGroupPython] H_element139  label="H_element : 086"  # scripted group (container) (typed FeaturePython)
  n = 11
  ref = H_element
FEATURE [App::DocumentObjectGroupPython] C_element149  label="C_element : 094"  # scripted group (container) (typed FeaturePython)
  n = 10
  ref = C_element
FEATURE [App::DocumentObjectGroupPython] N_element068  label="N_element : 040"  # scripted group (container) (typed FeaturePython)
  n = 2
  ref = N_element
FEATURE [App::DocumentObjectGroupPython] O_element130  label="O_element : 081"  # scripted group (container) (typed FeaturePython)
  n = 9
  ref = O_element
FEATURE [App::DocumentObjectGroupPython] P_element019  label="P_element : 008"  # scripted group (container) (typed FeaturePython)
  n = 1
  ref = P_element
FEATURE [App::DocumentObjectGroupPython] G4_DNA_MU  # scripted group (container) (typed FeaturePython)
  Dunit = g/cm3
  Dvalue = 1
  Group = -> [H_element139,C_element149,N_element068,O_element130,P_element019]
  conduct = 2
  density = 1
  expand = 3
  formula = G4_DNA_MU
  name = G4_DNA_MU
  specific = 4
FEATURE [App::DocumentObjectGroupPython] BioChemical  # scripted group (container) (typed FeaturePython)
  Group = -> [G4_CYTOSINE,G4_THYMINE,G4_URACIL,G4_DNA_ADENINE,G4_DNA_GUANINE,G4_DNA_CYTOSINE,G4_DNA_THYMINE,G4_DNA_URACIL,G4_DNA_ADENOSINE,G4_DNA_GUANOSINE,G4_DNA_CYTIDINE,G4_DNA_URIDINE,G4_DNA_METHYLURIDINE,G4_DNA_MONOPHOSPHATE,G4_DNA_A,G4_DNA_G,G4_DNA_C,G4_DNA_U,G4_DNA_MU]
FEATURE [App::DocumentObjectGroupPython] G4Materials  # scripted group (container) (typed FeaturePython)
  Group = -> [NIST,Element,HEP,Space,BioChemical]
  version = 1
FEATURE [App::DocumentObjectGroupPython] Geant4  # scripted group (container) (typed FeaturePython)
  Group = -> [G4Isotopes,G4Elements,G4Materials]
FEATURE [App::DocumentObjectGroupPython] Materials  # scripted group (container) (typed FeaturePython)
  Group = -> [Geant4]
FEATURE [Part::FeaturePython] GDMLBox_WorldBox  # WARN: FeaturePython — macro-defined, semantics opaque (R4)
  lunit = 2
  material = 7
  x = 100
  y = 100
  z = 100
FEATURE [Part::Box] Box  label="Cube"
  AttacherType = Attacher::AttachEngine3D
  Height = 10
  Length = 10
  Width = 10
FEATURE [Part::Cylinder] Cylinder
  Angle = 360
  AttacherType = Attacher::AttachEngine3D
  FirstAngle = 0
  Height = 12
  Placement = pos=(8,5,-1) rot=(0,0,1;0rad)
  Radius = 2
  SecondAngle = 0
FEATURE [Part::Cut] Cut
  Base = -> Box
  Tool = -> Cylinder
FEATURE [Part::FeaturePython] Array  # Draft array (typed FeaturePython)
  AlwaysSyncPlacement = false
  Angle = 360
  ArrayType = 0
  Axis = (0,0,1)
  Base = -> Cut
  Center = (0,0,0)
  Count = 4
  ExpandArray = false
  Fuse = true
  IntervalAxis = (0,0,0)
  IntervalX = (20,0,0)
  IntervalY = (0,20,0)
  IntervalZ = (0,0,100)
  NumberCircles = 3
  NumberPolar = 5
  NumberX = 2
  NumberY = 2
  NumberZ = 1
  PlacementList = 4 placements: [(0,0,0),(0,20,0),(20,0,0),(20,20,0)]
  RadialDistance = 50
  ScaleList = (4) [(1,1,1),(1,1,1),(1,1,1),(1,1,1)]
  Symmetry = 1
  TangentialDistance = 25
FEATURE [App::Part] Part
  Group = -> [Cylinder,Box,Array,Cut]
  Origin = -> Origin001
  Placement = pos=(6,0,0) rot=(0,0,1;0rad)
FEATURE [App::Part] worldVOL
  Group = -> [GDMLBox_WorldBox,Part]
  Origin = -> Origin
